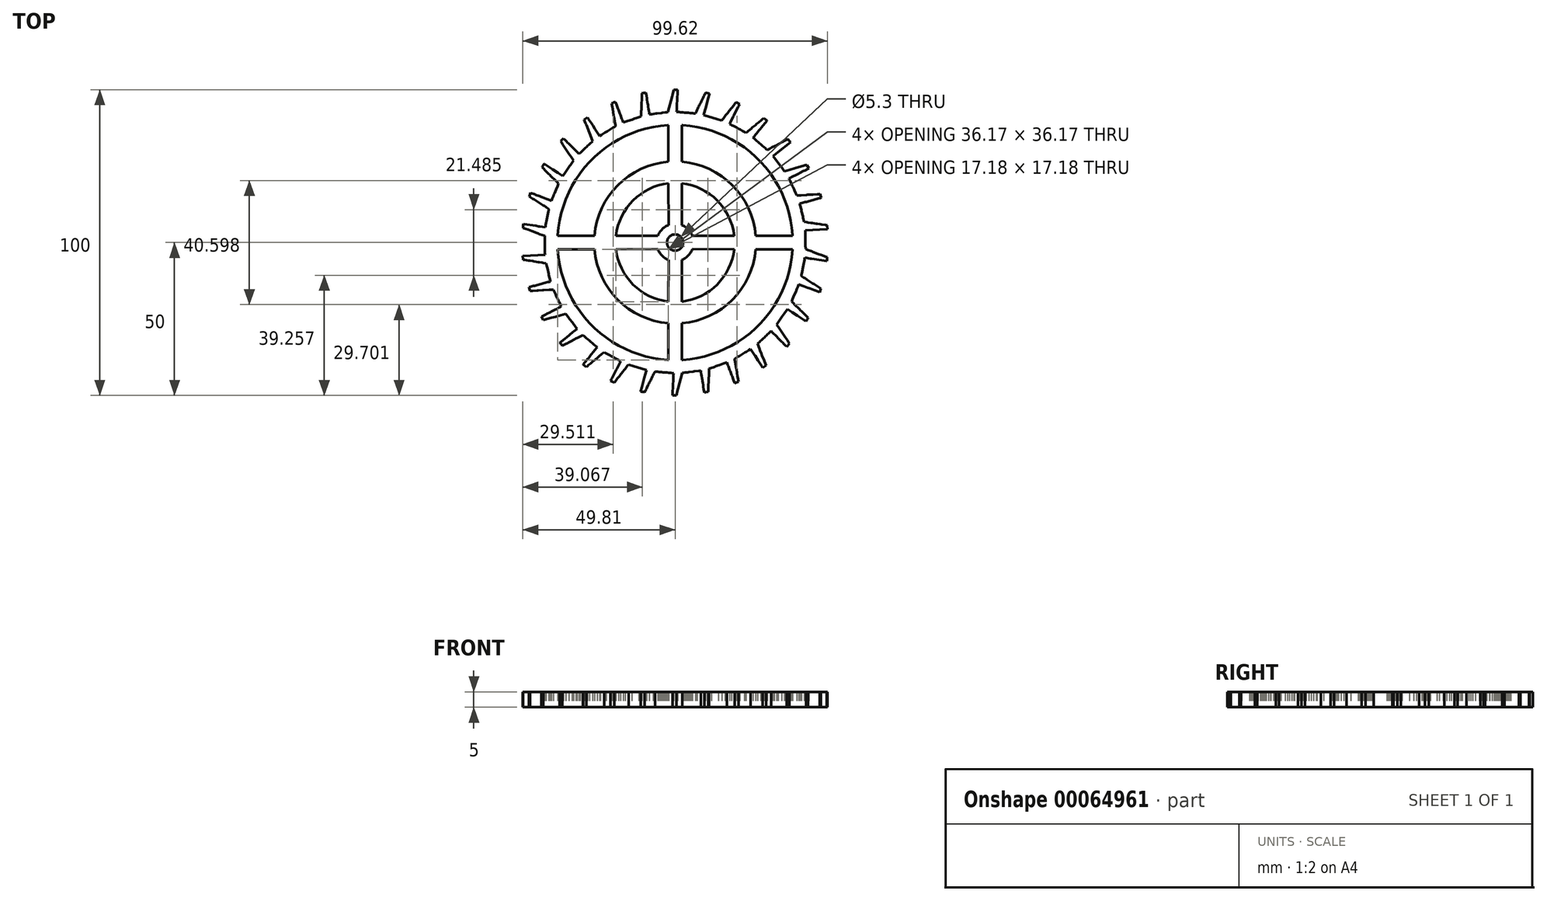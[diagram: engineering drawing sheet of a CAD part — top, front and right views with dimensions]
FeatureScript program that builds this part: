
annotation { "Feature Type Name" : "Feature", "Feature Type Description" : "" }
export const myFeature = defineFeature(function(context is Context, id is Id, definition is map)
    precondition{}
    {
        {
            var Q0;
            Q0=qCreatedBy(makeId("Top.planeOp"),FACE);
            var sketch = newSketch(context, id + "F0", { "sketchPlane" : qUnion([Q0])});
            skLineSegment(sketch, "E0", {"start": v(-36.57, 34.1) * mm, "end": v(-36.87, 33.77) * mm});
            skLineSegment(sketch, "E1", {"start": v(-36.87, 33.77) * mm, "end": v(-37.17, 33.44) * mm});
            skLineSegment(sketch, "E2", {"start": v(-37.17, 33.44) * mm, "end": v(-37.45, 33.13) * mm});
            skLineSegment(sketch, "E3", {"start": v(-37.45, 33.13) * mm, "end": v(-37.2, 32.76) * mm});
            skLineSegment(sketch, "E4", {"start": v(-37.2, 32.76) * mm, "end": v(-36.95, 32.39) * mm});
            skLineSegment(sketch, "E5", {"start": v(-36.95, 32.39) * mm, "end": v(-36.7, 32.02) * mm});
            skLineSegment(sketch, "E6", {"start": v(-36.7, 32.02) * mm, "end": v(-36.46, 31.65) * mm});
            skLineSegment(sketch, "E7", {"start": v(-36.46, 31.65) * mm, "end": v(-36.21, 31.28) * mm});
            skLineSegment(sketch, "E8", {"start": v(-36.21, 31.28) * mm, "end": v(-35.97, 30.9) * mm});
            skLineSegment(sketch, "E9", {"start": v(-35.97, 30.9) * mm, "end": v(-35.72, 30.53) * mm});
            skLineSegment(sketch, "E10", {"start": v(-35.72, 30.53) * mm, "end": v(-35.47, 30.16) * mm});
            skLineSegment(sketch, "E11", {"start": v(-35.47, 30.16) * mm, "end": v(-35.23, 29.8) * mm});
            skLineSegment(sketch, "E12", {"start": v(-35.23, 29.8) * mm, "end": v(-34.98, 29.42) * mm});
            skLineSegment(sketch, "E13", {"start": v(-34.98, 29.42) * mm, "end": v(-34.74, 29.05) * mm});
            skLineSegment(sketch, "E14", {"start": v(-34.74, 29.05) * mm, "end": v(-34.49, 28.68) * mm});
            skLineSegment(sketch, "E15", {"start": v(-34.49, 28.68) * mm, "end": v(-34.24, 28.3) * mm});
            skLineSegment(sketch, "E16", {"start": v(-34.24, 28.3) * mm, "end": v(-34, 27.93) * mm});
            skLineSegment(sketch, "E17", {"start": v(-34, 27.93) * mm, "end": v(-33.75, 27.56) * mm});
            skLineSegment(sketch, "E18", {"start": v(-33.75, 27.56) * mm, "end": v(-33.5, 27.2) * mm});
            skLineSegment(sketch, "E19", {"start": v(-33.5, 27.2) * mm, "end": v(-33.26, 26.83) * mm});
            skLineSegment(sketch, "E20", {"start": v(-33.26, 26.83) * mm, "end": v(-33.51, 26.46) * mm});
            skLineSegment(sketch, "E21", {"start": v(-33.51, 26.46) * mm, "end": v(-33.77, 26.1) * mm});
            skLineSegment(sketch, "E22", {"start": v(-33.77, 26.1) * mm, "end": v(-34.02, 25.73) * mm});
            skLineSegment(sketch, "E23", {"start": v(-34.02, 25.73) * mm, "end": v(-34.28, 25.37) * mm});
            skLineSegment(sketch, "E24", {"start": v(-34.28, 25.37) * mm, "end": v(-34.53, 25) * mm});
            skLineSegment(sketch, "E25", {"start": v(-34.53, 25) * mm, "end": v(-34.79, 24.63) * mm});
            skLineSegment(sketch, "E26", {"start": v(-34.79, 24.63) * mm, "end": v(-35.04, 24.27) * mm});
            skLineSegment(sketch, "E27", {"start": v(-35.04, 24.27) * mm, "end": v(-35.3, 23.9) * mm});
            skLineSegment(sketch, "E28", {"start": v(-35.3, 23.9) * mm, "end": v(-35.55, 23.53) * mm});
            skLineSegment(sketch, "E29", {"start": v(-35.55, 23.53) * mm, "end": v(-35.8, 23.17) * mm});
            skLineSegment(sketch, "E30", {"start": v(-35.8, 23.17) * mm, "end": v(-36.06, 22.8) * mm});
            skLineSegment(sketch, "E31", {"start": v(-36.06, 22.8) * mm, "end": v(-36.31, 22.44) * mm});
            skLineSegment(sketch, "E32", {"start": v(-36.31, 22.44) * mm, "end": v(-36.56, 22.07) * mm});
            skLineSegment(sketch, "E33", {"start": v(-36.56, 22.07) * mm, "end": v(-36.76, 21.8) * mm});
            skLineSegment(sketch, "E34", {"start": v(-36.76, 21.8) * mm, "end": v(-37.13, 22.03) * mm});
            skLineSegment(sketch, "E35", {"start": v(-37.13, 22.03) * mm, "end": v(-37.5, 22.28) * mm});
            skLineSegment(sketch, "E36", {"start": v(-37.5, 22.28) * mm, "end": v(-37.88, 22.52) * mm});
            skLineSegment(sketch, "E37", {"start": v(-37.88, 22.52) * mm, "end": v(-38.25, 22.76) * mm});
            skLineSegment(sketch, "E38", {"start": v(-38.25, 22.76) * mm, "end": v(-38.63, 23) * mm});
            skLineSegment(sketch, "E39", {"start": v(-38.63, 23) * mm, "end": v(-39, 23.25) * mm});
            skLineSegment(sketch, "E40", {"start": v(-39, 23.25) * mm, "end": v(-39.38, 23.49) * mm});
            skLineSegment(sketch, "E41", {"start": v(-39.38, 23.49) * mm, "end": v(-39.75, 23.73) * mm});
            skLineSegment(sketch, "E42", {"start": v(-39.75, 23.73) * mm, "end": v(-40.12, 23.98) * mm});
            skLineSegment(sketch, "E43", {"start": v(-40.12, 23.98) * mm, "end": v(-40.5, 24.22) * mm});
            skLineSegment(sketch, "E44", {"start": v(-40.5, 24.22) * mm, "end": v(-40.87, 24.46) * mm});
            skLineSegment(sketch, "E45", {"start": v(-40.87, 24.46) * mm, "end": v(-41.24, 24.7) * mm});
            skLineSegment(sketch, "E46", {"start": v(-41.24, 24.7) * mm, "end": v(-41.62, 24.95) * mm});
            skLineSegment(sketch, "E47", {"start": v(-41.62, 24.95) * mm, "end": v(-42, 25.19) * mm});
            skLineSegment(sketch, "E48", {"start": v(-42, 25.19) * mm, "end": v(-42.37, 25.43) * mm});
            skLineSegment(sketch, "E49", {"start": v(-42.37, 25.43) * mm, "end": v(-42.74, 25.67) * mm});
            skLineSegment(sketch, "E50", {"start": v(-42.74, 25.67) * mm, "end": v(-42.86, 25.75) * mm});
            skLineSegment(sketch, "E51", {"start": v(-42.86, 25.75) * mm, "end": v(-43.08, 25.37) * mm});
            skLineSegment(sketch, "E52", {"start": v(-43.08, 25.37) * mm, "end": v(-43.3, 24.98) * mm});
            skLineSegment(sketch, "E53", {"start": v(-43.3, 24.98) * mm, "end": v(-43.52, 24.62) * mm});
            skLineSegment(sketch, "E54", {"start": v(-43.52, 24.62) * mm, "end": v(-43.2, 24.3) * mm});
            skLineSegment(sketch, "E55", {"start": v(-43.2, 24.3) * mm, "end": v(-42.88, 24) * mm});
            skLineSegment(sketch, "E56", {"start": v(-42.88, 24) * mm, "end": v(-42.56, 23.69) * mm});
            skLineSegment(sketch, "E57", {"start": v(-42.56, 23.69) * mm, "end": v(-42.24, 23.37) * mm});
            skLineSegment(sketch, "E58", {"start": v(-42.24, 23.37) * mm, "end": v(-41.93, 23.06) * mm});
            skLineSegment(sketch, "E59", {"start": v(-41.93, 23.06) * mm, "end": v(-41.6, 22.75) * mm});
            skLineSegment(sketch, "E60", {"start": v(-41.6, 22.75) * mm, "end": v(-41.29, 22.44) * mm});
            skLineSegment(sketch, "E61", {"start": v(-41.29, 22.44) * mm, "end": v(-40.97, 22.13) * mm});
            skLineSegment(sketch, "E62", {"start": v(-40.97, 22.13) * mm, "end": v(-40.65, 21.82) * mm});
            skLineSegment(sketch, "E63", {"start": v(-40.65, 21.82) * mm, "end": v(-40.33, 21.5) * mm});
            skLineSegment(sketch, "E64", {"start": v(-40.33, 21.5) * mm, "end": v(-40.02, 21.2) * mm});
            skLineSegment(sketch, "E65", {"start": v(-40.02, 21.2) * mm, "end": v(-39.7, 20.88) * mm});
            skLineSegment(sketch, "E66", {"start": v(-39.7, 20.88) * mm, "end": v(-39.38, 20.57) * mm});
            skLineSegment(sketch, "E67", {"start": v(-39.38, 20.57) * mm, "end": v(-39.06, 20.26) * mm});
            skLineSegment(sketch, "E68", {"start": v(-39.06, 20.26) * mm, "end": v(-38.74, 19.94) * mm});
            skLineSegment(sketch, "E69", {"start": v(-38.74, 19.94) * mm, "end": v(-38.42, 19.63) * mm});
            skLineSegment(sketch, "E70", {"start": v(-38.42, 19.63) * mm, "end": v(-38.11, 19.33) * mm});
            skLineSegment(sketch, "E71", {"start": v(-38.11, 19.33) * mm, "end": v(-38.28, 18.92) * mm});
            skLineSegment(sketch, "E72", {"start": v(-38.28, 18.92) * mm, "end": v(-38.46, 18.5) * mm});
            skLineSegment(sketch, "E73", {"start": v(-38.46, 18.5) * mm, "end": v(-38.63, 18.1) * mm});
            skLineSegment(sketch, "E74", {"start": v(-38.63, 18.1) * mm, "end": v(-38.8, 17.68) * mm});
            skLineSegment(sketch, "E75", {"start": v(-38.8, 17.68) * mm, "end": v(-38.97, 17.27) * mm});
            skLineSegment(sketch, "E76", {"start": v(-38.97, 17.27) * mm, "end": v(-39.15, 16.86) * mm});
            skLineSegment(sketch, "E77", {"start": v(-39.15, 16.86) * mm, "end": v(-39.32, 16.45) * mm});
            skLineSegment(sketch, "E78", {"start": v(-39.32, 16.45) * mm, "end": v(-39.5, 16.04) * mm});
            skLineSegment(sketch, "E79", {"start": v(-39.5, 16.04) * mm, "end": v(-39.66, 15.63) * mm});
            skLineSegment(sketch, "E80", {"start": v(-39.66, 15.63) * mm, "end": v(-39.84, 15.22) * mm});
            skLineSegment(sketch, "E81", {"start": v(-39.84, 15.22) * mm, "end": v(-40, 14.8) * mm});
            skLineSegment(sketch, "E82", {"start": v(-40, 14.8) * mm, "end": v(-40.18, 14.4) * mm});
            skLineSegment(sketch, "E83", {"start": v(-40.18, 14.4) * mm, "end": v(-40.35, 13.99) * mm});
            skLineSegment(sketch, "E84", {"start": v(-40.35, 13.99) * mm, "end": v(-40.49, 13.67) * mm});
            skLineSegment(sketch, "E85", {"start": v(-40.49, 13.67) * mm, "end": v(-40.9, 13.83) * mm});
            skLineSegment(sketch, "E86", {"start": v(-40.9, 13.83) * mm, "end": v(-41.32, 14) * mm});
            skLineSegment(sketch, "E87", {"start": v(-41.32, 14) * mm, "end": v(-41.73, 14.15) * mm});
            skLineSegment(sketch, "E88", {"start": v(-41.73, 14.15) * mm, "end": v(-42.15, 14.31) * mm});
            skLineSegment(sketch, "E89", {"start": v(-42.15, 14.31) * mm, "end": v(-42.57, 14.47) * mm});
            skLineSegment(sketch, "E90", {"start": v(-42.57, 14.47) * mm, "end": v(-42.98, 14.63) * mm});
            skLineSegment(sketch, "E91", {"start": v(-42.98, 14.63) * mm, "end": v(-43.4, 14.8) * mm});
            skLineSegment(sketch, "E92", {"start": v(-43.4, 14.8) * mm, "end": v(-43.81, 14.95) * mm});
            skLineSegment(sketch, "E93", {"start": v(-43.81, 14.95) * mm, "end": v(-44.23, 15.1) * mm});
            skLineSegment(sketch, "E94", {"start": v(-44.23, 15.1) * mm, "end": v(-44.65, 15.27) * mm});
            skLineSegment(sketch, "E95", {"start": v(-44.65, 15.27) * mm, "end": v(-45.06, 15.43) * mm});
            skLineSegment(sketch, "E96", {"start": v(-45.06, 15.43) * mm, "end": v(-45.48, 15.59) * mm});
            skLineSegment(sketch, "E97", {"start": v(-45.48, 15.59) * mm, "end": v(-45.9, 15.75) * mm});
            skLineSegment(sketch, "E98", {"start": v(-45.9, 15.75) * mm, "end": v(-46.31, 15.9) * mm});
            skLineSegment(sketch, "E99", {"start": v(-46.31, 15.9) * mm, "end": v(-46.73, 16.07) * mm});
            skLineSegment(sketch, "E100", {"start": v(-46.73, 16.07) * mm, "end": v(-47.14, 16.23) * mm});
            skLineSegment(sketch, "E101", {"start": v(-47.14, 16.23) * mm, "end": v(-47.28, 16.28) * mm});
            skLineSegment(sketch, "E102", {"start": v(-47.28, 16.28) * mm, "end": v(-47.42, 15.86) * mm});
            skLineSegment(sketch, "E103", {"start": v(-47.42, 15.86) * mm, "end": v(-47.56, 15.43) * mm});
            skLineSegment(sketch, "E104", {"start": v(-47.56, 15.43) * mm, "end": v(-47.69, 15.04) * mm});
            skLineSegment(sketch, "E105", {"start": v(-47.69, 15.04) * mm, "end": v(-47.3, 14.8) * mm});
            skLineSegment(sketch, "E106", {"start": v(-47.3, 14.8) * mm, "end": v(-46.93, 14.56) * mm});
            skLineSegment(sketch, "E107", {"start": v(-46.93, 14.56) * mm, "end": v(-46.56, 14.32) * mm});
            skLineSegment(sketch, "E108", {"start": v(-46.56, 14.32) * mm, "end": v(-46.18, 14.08) * mm});
            skLineSegment(sketch, "E109", {"start": v(-46.18, 14.08) * mm, "end": v(-45.8, 13.84) * mm});
            skLineSegment(sketch, "E110", {"start": v(-45.8, 13.84) * mm, "end": v(-45.43, 13.6) * mm});
            skLineSegment(sketch, "E111", {"start": v(-45.43, 13.6) * mm, "end": v(-45.05, 13.36) * mm});
            skLineSegment(sketch, "E112", {"start": v(-45.05, 13.36) * mm, "end": v(-44.68, 13.13) * mm});
            skLineSegment(sketch, "E113", {"start": v(-44.68, 13.13) * mm, "end": v(-44.3, 12.89) * mm});
            skLineSegment(sketch, "E114", {"start": v(-44.3, 12.89) * mm, "end": v(-43.92, 12.65) * mm});
            skLineSegment(sketch, "E115", {"start": v(-43.92, 12.65) * mm, "end": v(-43.55, 12.4) * mm});
            skLineSegment(sketch, "E116", {"start": v(-43.55, 12.4) * mm, "end": v(-43.17, 12.17) * mm});
            skLineSegment(sketch, "E117", {"start": v(-43.17, 12.17) * mm, "end": v(-42.8, 11.93) * mm});
            skLineSegment(sketch, "E118", {"start": v(-42.8, 11.93) * mm, "end": v(-42.42, 11.7) * mm});
            skLineSegment(sketch, "E119", {"start": v(-42.42, 11.7) * mm, "end": v(-42.04, 11.45) * mm});
            skLineSegment(sketch, "E120", {"start": v(-42.04, 11.45) * mm, "end": v(-41.67, 11.22) * mm});
            skLineSegment(sketch, "E121", {"start": v(-41.67, 11.22) * mm, "end": v(-41.3, 10.98) * mm});
            skLineSegment(sketch, "E122", {"start": v(-41.3, 10.98) * mm, "end": v(-41.38, 10.54) * mm});
            skLineSegment(sketch, "E123", {"start": v(-41.38, 10.54) * mm, "end": v(-41.46, 10.1) * mm});
            skLineSegment(sketch, "E124", {"start": v(-41.46, 10.1) * mm, "end": v(-41.55, 9.67) * mm});
            skLineSegment(sketch, "E125", {"start": v(-41.55, 9.67) * mm, "end": v(-41.63, 9.23) * mm});
            skLineSegment(sketch, "E126", {"start": v(-41.63, 9.23) * mm, "end": v(-41.71, 8.8) * mm});
            skLineSegment(sketch, "E127", {"start": v(-41.71, 8.8) * mm, "end": v(-41.8, 8.35) * mm});
            skLineSegment(sketch, "E128", {"start": v(-41.8, 8.35) * mm, "end": v(-41.88, 7.92) * mm});
            skLineSegment(sketch, "E129", {"start": v(-41.88, 7.92) * mm, "end": v(-41.96, 7.48) * mm});
            skLineSegment(sketch, "E130", {"start": v(-41.96, 7.48) * mm, "end": v(-42.05, 7.04) * mm});
            skLineSegment(sketch, "E131", {"start": v(-42.05, 7.04) * mm, "end": v(-42.13, 6.6) * mm});
            skLineSegment(sketch, "E132", {"start": v(-42.13, 6.6) * mm, "end": v(-42.21, 6.17) * mm});
            skLineSegment(sketch, "E133", {"start": v(-42.21, 6.17) * mm, "end": v(-42.3, 5.73) * mm});
            skLineSegment(sketch, "E134", {"start": v(-42.3, 5.73) * mm, "end": v(-42.38, 5.3) * mm});
            skLineSegment(sketch, "E135", {"start": v(-42.38, 5.3) * mm, "end": v(-42.44, 4.96) * mm});
            skLineSegment(sketch, "E136", {"start": v(-42.44, 4.96) * mm, "end": v(-42.88, 5.03) * mm});
            skLineSegment(sketch, "E137", {"start": v(-42.88, 5.03) * mm, "end": v(-43.32, 5.1) * mm});
            skLineSegment(sketch, "E138", {"start": v(-43.32, 5.1) * mm, "end": v(-43.76, 5.16) * mm});
            skLineSegment(sketch, "E139", {"start": v(-43.76, 5.16) * mm, "end": v(-44.2, 5.23) * mm});
            skLineSegment(sketch, "E140", {"start": v(-44.2, 5.23) * mm, "end": v(-44.65, 5.3) * mm});
            skLineSegment(sketch, "E141", {"start": v(-44.65, 5.3) * mm, "end": v(-45.09, 5.37) * mm});
            skLineSegment(sketch, "E142", {"start": v(-45.09, 5.37) * mm, "end": v(-45.53, 5.44) * mm});
            skLineSegment(sketch, "E143", {"start": v(-45.53, 5.44) * mm, "end": v(-45.97, 5.51) * mm});
            skLineSegment(sketch, "E144", {"start": v(-45.97, 5.51) * mm, "end": v(-46.4, 5.58) * mm});
            skLineSegment(sketch, "E145", {"start": v(-46.4, 5.58) * mm, "end": v(-46.85, 5.65) * mm});
            skLineSegment(sketch, "E146", {"start": v(-46.85, 5.65) * mm, "end": v(-47.29, 5.72) * mm});
            skLineSegment(sketch, "E147", {"start": v(-47.29, 5.72) * mm, "end": v(-47.73, 5.8) * mm});
            skLineSegment(sketch, "E148", {"start": v(-47.73, 5.8) * mm, "end": v(-48.17, 5.86) * mm});
            skLineSegment(sketch, "E149", {"start": v(-48.17, 5.86) * mm, "end": v(-48.6, 5.93) * mm});
            skLineSegment(sketch, "E150", {"start": v(-48.6, 5.93) * mm, "end": v(-49.05, 6) * mm});
            skLineSegment(sketch, "E151", {"start": v(-49.05, 6) * mm, "end": v(-49.49, 6.07) * mm});
            skLineSegment(sketch, "E152", {"start": v(-49.49, 6.07) * mm, "end": v(-49.63, 6.1) * mm});
            skLineSegment(sketch, "E153", {"start": v(-49.63, 6.1) * mm, "end": v(-49.68, 5.65) * mm});
            skLineSegment(sketch, "E154", {"start": v(-49.68, 5.65) * mm, "end": v(-49.72, 5.2) * mm});
            skLineSegment(sketch, "E155", {"start": v(-49.72, 5.2) * mm, "end": v(-49.77, 4.8) * mm});
            skLineSegment(sketch, "E156", {"start": v(-49.77, 4.8) * mm, "end": v(-49.35, 4.64) * mm});
            skLineSegment(sketch, "E157", {"start": v(-49.35, 4.64) * mm, "end": v(-48.93, 4.48) * mm});
            skLineSegment(sketch, "E158", {"start": v(-48.93, 4.48) * mm, "end": v(-48.52, 4.33) * mm});
            skLineSegment(sketch, "E159", {"start": v(-48.52, 4.33) * mm, "end": v(-48.1, 4.17) * mm});
            skLineSegment(sketch, "E160", {"start": v(-48.1, 4.17) * mm, "end": v(-47.68, 4.02) * mm});
            skLineSegment(sketch, "E161", {"start": v(-47.68, 4.02) * mm, "end": v(-47.26, 3.86) * mm});
            skLineSegment(sketch, "E162", {"start": v(-47.26, 3.86) * mm, "end": v(-46.85, 3.7) * mm});
            skLineSegment(sketch, "E163", {"start": v(-46.85, 3.7) * mm, "end": v(-46.43, 3.55) * mm});
            skLineSegment(sketch, "E164", {"start": v(-46.43, 3.55) * mm, "end": v(-46.01, 3.4) * mm});
            skLineSegment(sketch, "E165", {"start": v(-46.01, 3.4) * mm, "end": v(-45.6, 3.24) * mm});
            skLineSegment(sketch, "E166", {"start": v(-45.6, 3.24) * mm, "end": v(-45.18, 3.08) * mm});
            skLineSegment(sketch, "E167", {"start": v(-45.18, 3.08) * mm, "end": v(-44.76, 2.93) * mm});
            skLineSegment(sketch, "E168", {"start": v(-44.76, 2.93) * mm, "end": v(-44.34, 2.77) * mm});
            skLineSegment(sketch, "E169", {"start": v(-44.34, 2.77) * mm, "end": v(-43.92, 2.62) * mm});
            skLineSegment(sketch, "E170", {"start": v(-43.92, 2.62) * mm, "end": v(-43.5, 2.46) * mm});
            skLineSegment(sketch, "E171", {"start": v(-43.5, 2.46) * mm, "end": v(-43.09, 2.3) * mm});
            skLineSegment(sketch, "E172", {"start": v(-43.09, 2.3) * mm, "end": v(-42.68, 2.16) * mm});
            skLineSegment(sketch, "E173", {"start": v(-42.68, 2.16) * mm, "end": v(-42.67, 1.7) * mm});
            skLineSegment(sketch, "E174", {"start": v(-42.67, 1.7) * mm, "end": v(-42.66, 1.26) * mm});
            skLineSegment(sketch, "E175", {"start": v(-42.66, 1.26) * mm, "end": v(-42.65, 0.82) * mm});
            skLineSegment(sketch, "E176", {"start": v(-42.65, 0.82) * mm, "end": v(-42.64, 0.37) * mm});
            skLineSegment(sketch, "E177", {"start": v(-42.64, 0.37) * mm, "end": v(-42.63, -0.07) * mm});
            skLineSegment(sketch, "E178", {"start": v(-42.63, -0.07) * mm, "end": v(-42.62, -0.52) * mm});
            skLineSegment(sketch, "E179", {"start": v(-42.62, -0.52) * mm, "end": v(-42.61, -0.96) * mm});
            skLineSegment(sketch, "E180", {"start": v(-42.61, -0.96) * mm, "end": v(-42.6, -1.4) * mm});
            skLineSegment(sketch, "E181", {"start": v(-42.6, -1.4) * mm, "end": v(-42.6, -1.85) * mm});
            skLineSegment(sketch, "E182", {"start": v(-42.6, -1.85) * mm, "end": v(-42.58, -2.3) * mm});
            skLineSegment(sketch, "E183", {"start": v(-42.58, -2.3) * mm, "end": v(-42.57, -2.75) * mm});
            skLineSegment(sketch, "E184", {"start": v(-42.57, -2.75) * mm, "end": v(-42.56, -3.2) * mm});
            skLineSegment(sketch, "E185", {"start": v(-42.56, -3.2) * mm, "end": v(-42.55, -3.64) * mm});
            skLineSegment(sketch, "E186", {"start": v(-42.55, -3.64) * mm, "end": v(-42.55, -3.98) * mm});
            skLineSegment(sketch, "E187", {"start": v(-42.55, -3.98) * mm, "end": v(-43, -4) * mm});
            skLineSegment(sketch, "E188", {"start": v(-43, -4) * mm, "end": v(-43.44, -4.02) * mm});
            skLineSegment(sketch, "E189", {"start": v(-43.44, -4.02) * mm, "end": v(-43.88, -4.05) * mm});
            skLineSegment(sketch, "E190", {"start": v(-43.88, -4.05) * mm, "end": v(-44.33, -4.07) * mm});
            skLineSegment(sketch, "E191", {"start": v(-44.33, -4.07) * mm, "end": v(-44.77, -4.1) * mm});
            skLineSegment(sketch, "E192", {"start": v(-44.77, -4.1) * mm, "end": v(-45.22, -4.12) * mm});
            skLineSegment(sketch, "E193", {"start": v(-45.22, -4.12) * mm, "end": v(-45.66, -4.14) * mm});
            skLineSegment(sketch, "E194", {"start": v(-45.66, -4.14) * mm, "end": v(-46.1, -4.16) * mm});
            skLineSegment(sketch, "E195", {"start": v(-46.1, -4.16) * mm, "end": v(-46.55, -4.19) * mm});
            skLineSegment(sketch, "E196", {"start": v(-46.55, -4.19) * mm, "end": v(-47, -4.21) * mm});
            skLineSegment(sketch, "E197", {"start": v(-47, -4.21) * mm, "end": v(-47.44, -4.23) * mm});
            skLineSegment(sketch, "E198", {"start": v(-47.44, -4.23) * mm, "end": v(-47.89, -4.26) * mm});
            skLineSegment(sketch, "E199", {"start": v(-47.89, -4.26) * mm, "end": v(-48.33, -4.28) * mm});
            skLineSegment(sketch, "E200", {"start": v(-48.33, -4.28) * mm, "end": v(-48.78, -4.3) * mm});
            skLineSegment(sketch, "E201", {"start": v(-48.78, -4.3) * mm, "end": v(-49.22, -4.33) * mm});
            skLineSegment(sketch, "E202", {"start": v(-49.22, -4.33) * mm, "end": v(-49.67, -4.35) * mm});
            skLineSegment(sketch, "E203", {"start": v(-49.67, -4.35) * mm, "end": v(-49.8, -4.36) * mm});
            skLineSegment(sketch, "E204", {"start": v(-49.8, -4.36) * mm, "end": v(-49.77, -4.8) * mm});
            skLineSegment(sketch, "E205", {"start": v(-49.77, -4.8) * mm, "end": v(-49.72, -5.24) * mm});
            skLineSegment(sketch, "E206", {"start": v(-49.72, -5.24) * mm, "end": v(-49.68, -5.66) * mm});
            skLineSegment(sketch, "E207", {"start": v(-49.68, -5.66) * mm, "end": v(-49.24, -5.73) * mm});
            skLineSegment(sketch, "E208", {"start": v(-49.24, -5.73) * mm, "end": v(-48.8, -5.8) * mm});
            skLineSegment(sketch, "E209", {"start": v(-48.8, -5.8) * mm, "end": v(-48.36, -5.86) * mm});
            skLineSegment(sketch, "E210", {"start": v(-48.36, -5.86) * mm, "end": v(-47.92, -5.92) * mm});
            skLineSegment(sketch, "E211", {"start": v(-47.92, -5.92) * mm, "end": v(-47.47, -5.99) * mm});
            skLineSegment(sketch, "E212", {"start": v(-47.47, -5.99) * mm, "end": v(-47.03, -6.05) * mm});
            skLineSegment(sketch, "E213", {"start": v(-47.03, -6.05) * mm, "end": v(-46.6, -6.12) * mm});
            skLineSegment(sketch, "E214", {"start": v(-46.6, -6.12) * mm, "end": v(-46.15, -6.18) * mm});
            skLineSegment(sketch, "E215", {"start": v(-46.15, -6.18) * mm, "end": v(-45.71, -6.25) * mm});
            skLineSegment(sketch, "E216", {"start": v(-45.71, -6.25) * mm, "end": v(-45.27, -6.31) * mm});
            skLineSegment(sketch, "E217", {"start": v(-45.27, -6.31) * mm, "end": v(-44.83, -6.38) * mm});
            skLineSegment(sketch, "E218", {"start": v(-44.83, -6.38) * mm, "end": v(-44.39, -6.44) * mm});
            skLineSegment(sketch, "E219", {"start": v(-44.39, -6.44) * mm, "end": v(-43.95, -6.5) * mm});
            skLineSegment(sketch, "E220", {"start": v(-43.95, -6.5) * mm, "end": v(-43.5, -6.57) * mm});
            skLineSegment(sketch, "E221", {"start": v(-43.5, -6.57) * mm, "end": v(-43.07, -6.64) * mm});
            skLineSegment(sketch, "E222", {"start": v(-43.07, -6.64) * mm, "end": v(-42.63, -6.7) * mm});
            skLineSegment(sketch, "E223", {"start": v(-42.63, -6.7) * mm, "end": v(-42.2, -6.77) * mm});
            skLineSegment(sketch, "E224", {"start": v(-42.2, -6.77) * mm, "end": v(-42.1, -7.2) * mm});
            skLineSegment(sketch, "E225", {"start": v(-42.1, -7.2) * mm, "end": v(-41.99, -7.63) * mm});
            skLineSegment(sketch, "E226", {"start": v(-41.99, -7.63) * mm, "end": v(-41.89, -8.07) * mm});
            skLineSegment(sketch, "E227", {"start": v(-41.89, -8.07) * mm, "end": v(-41.79, -8.5) * mm});
            skLineSegment(sketch, "E228", {"start": v(-41.79, -8.5) * mm, "end": v(-41.68, -8.93) * mm});
            skLineSegment(sketch, "E229", {"start": v(-41.68, -8.93) * mm, "end": v(-41.58, -9.37) * mm});
            skLineSegment(sketch, "E230", {"start": v(-41.58, -9.37) * mm, "end": v(-41.48, -9.8) * mm});
            skLineSegment(sketch, "E231", {"start": v(-41.48, -9.8) * mm, "end": v(-41.38, -10.24) * mm});
            skLineSegment(sketch, "E232", {"start": v(-41.38, -10.24) * mm, "end": v(-41.28, -10.67) * mm});
            skLineSegment(sketch, "E233", {"start": v(-41.28, -10.67) * mm, "end": v(-41.17, -11.1) * mm});
            skLineSegment(sketch, "E234", {"start": v(-41.17, -11.1) * mm, "end": v(-41.07, -11.54) * mm});
            skLineSegment(sketch, "E235", {"start": v(-41.07, -11.54) * mm, "end": v(-40.97, -11.97) * mm});
            skLineSegment(sketch, "E236", {"start": v(-40.97, -11.97) * mm, "end": v(-40.87, -12.4) * mm});
            skLineSegment(sketch, "E237", {"start": v(-40.87, -12.4) * mm, "end": v(-40.8, -12.74) * mm});
            skLineSegment(sketch, "E238", {"start": v(-40.8, -12.74) * mm, "end": v(-41.22, -12.85) * mm});
            skLineSegment(sketch, "E239", {"start": v(-41.22, -12.85) * mm, "end": v(-41.65, -12.97) * mm});
            skLineSegment(sketch, "E240", {"start": v(-41.65, -12.97) * mm, "end": v(-42.08, -13.08) * mm});
            skLineSegment(sketch, "E241", {"start": v(-42.08, -13.08) * mm, "end": v(-42.51, -13.2) * mm});
            skLineSegment(sketch, "E242", {"start": v(-42.51, -13.2) * mm, "end": v(-42.94, -13.31) * mm});
            skLineSegment(sketch, "E243", {"start": v(-42.94, -13.31) * mm, "end": v(-43.37, -13.43) * mm});
            skLineSegment(sketch, "E244", {"start": v(-43.37, -13.43) * mm, "end": v(-43.8, -13.54) * mm});
            skLineSegment(sketch, "E245", {"start": v(-43.8, -13.54) * mm, "end": v(-44.23, -13.66) * mm});
            skLineSegment(sketch, "E246", {"start": v(-44.23, -13.66) * mm, "end": v(-44.66, -13.77) * mm});
            skLineSegment(sketch, "E247", {"start": v(-44.66, -13.77) * mm, "end": v(-45.1, -13.89) * mm});
            skLineSegment(sketch, "E248", {"start": v(-45.1, -13.89) * mm, "end": v(-45.53, -14) * mm});
            skLineSegment(sketch, "E249", {"start": v(-45.53, -14) * mm, "end": v(-45.96, -14.12) * mm});
            skLineSegment(sketch, "E250", {"start": v(-45.96, -14.12) * mm, "end": v(-46.39, -14.24) * mm});
            skLineSegment(sketch, "E251", {"start": v(-46.39, -14.24) * mm, "end": v(-46.82, -14.35) * mm});
            skLineSegment(sketch, "E252", {"start": v(-46.82, -14.35) * mm, "end": v(-47.25, -14.47) * mm});
            skLineSegment(sketch, "E253", {"start": v(-47.25, -14.47) * mm, "end": v(-47.68, -14.58) * mm});
            skLineSegment(sketch, "E254", {"start": v(-47.68, -14.58) * mm, "end": v(-47.82, -14.62) * mm});
            skLineSegment(sketch, "E255", {"start": v(-47.82, -14.62) * mm, "end": v(-47.68, -15.04) * mm});
            skLineSegment(sketch, "E256", {"start": v(-47.68, -15.04) * mm, "end": v(-47.54, -15.47) * mm});
            skLineSegment(sketch, "E257", {"start": v(-47.54, -15.47) * mm, "end": v(-47.42, -15.87) * mm});
            skLineSegment(sketch, "E258", {"start": v(-47.42, -15.87) * mm, "end": v(-46.97, -15.84) * mm});
            skLineSegment(sketch, "E259", {"start": v(-46.97, -15.84) * mm, "end": v(-46.53, -15.8) * mm});
            skLineSegment(sketch, "E260", {"start": v(-46.53, -15.8) * mm, "end": v(-46.08, -15.78) * mm});
            skLineSegment(sketch, "E261", {"start": v(-46.08, -15.78) * mm, "end": v(-45.64, -15.75) * mm});
            skLineSegment(sketch, "E262", {"start": v(-45.64, -15.75) * mm, "end": v(-45.2, -15.73) * mm});
            skLineSegment(sketch, "E263", {"start": v(-45.2, -15.73) * mm, "end": v(-44.75, -15.7) * mm});
            skLineSegment(sketch, "E264", {"start": v(-44.75, -15.7) * mm, "end": v(-44.3, -15.67) * mm});
            skLineSegment(sketch, "E265", {"start": v(-44.3, -15.67) * mm, "end": v(-43.86, -15.64) * mm});
            skLineSegment(sketch, "E266", {"start": v(-43.86, -15.64) * mm, "end": v(-43.41, -15.61) * mm});
            skLineSegment(sketch, "E267", {"start": v(-43.41, -15.61) * mm, "end": v(-42.97, -15.59) * mm});
            skLineSegment(sketch, "E268", {"start": v(-42.97, -15.59) * mm, "end": v(-42.52, -15.56) * mm});
            skLineSegment(sketch, "E269", {"start": v(-42.52, -15.56) * mm, "end": v(-42.08, -15.53) * mm});
            skLineSegment(sketch, "E270", {"start": v(-42.08, -15.53) * mm, "end": v(-41.63, -15.5) * mm});
            skLineSegment(sketch, "E271", {"start": v(-41.63, -15.5) * mm, "end": v(-41.19, -15.47) * mm});
            skLineSegment(sketch, "E272", {"start": v(-41.19, -15.47) * mm, "end": v(-40.75, -15.45) * mm});
            skLineSegment(sketch, "E273", {"start": v(-40.75, -15.45) * mm, "end": v(-40.3, -15.42) * mm});
            skLineSegment(sketch, "E274", {"start": v(-40.3, -15.42) * mm, "end": v(-39.87, -15.39) * mm});
            skLineSegment(sketch, "E275", {"start": v(-39.87, -15.39) * mm, "end": v(-39.68, -15.8) * mm});
            skLineSegment(sketch, "E276", {"start": v(-39.68, -15.8) * mm, "end": v(-39.49, -16.2) * mm});
            skLineSegment(sketch, "E277", {"start": v(-39.49, -16.2) * mm, "end": v(-39.3, -16.6) * mm});
            skLineSegment(sketch, "E278", {"start": v(-39.3, -16.6) * mm, "end": v(-39.1, -17) * mm});
            skLineSegment(sketch, "E279", {"start": v(-39.1, -17) * mm, "end": v(-38.92, -17.4) * mm});
            skLineSegment(sketch, "E280", {"start": v(-38.92, -17.4) * mm, "end": v(-38.73, -17.8) * mm});
            skLineSegment(sketch, "E281", {"start": v(-38.73, -17.8) * mm, "end": v(-38.54, -18.21) * mm});
            skLineSegment(sketch, "E282", {"start": v(-38.54, -18.21) * mm, "end": v(-38.35, -18.61) * mm});
            skLineSegment(sketch, "E283", {"start": v(-38.35, -18.61) * mm, "end": v(-38.16, -19.02) * mm});
            skLineSegment(sketch, "E284", {"start": v(-38.16, -19.02) * mm, "end": v(-37.97, -19.42) * mm});
            skLineSegment(sketch, "E285", {"start": v(-37.97, -19.42) * mm, "end": v(-37.78, -19.82) * mm});
            skLineSegment(sketch, "E286", {"start": v(-37.78, -19.82) * mm, "end": v(-37.59, -20.23) * mm});
            skLineSegment(sketch, "E287", {"start": v(-37.59, -20.23) * mm, "end": v(-37.4, -20.63) * mm});
            skLineSegment(sketch, "E288", {"start": v(-37.4, -20.63) * mm, "end": v(-37.25, -20.94) * mm});
            skLineSegment(sketch, "E289", {"start": v(-37.25, -20.94) * mm, "end": v(-37.65, -21.14) * mm});
            skLineSegment(sketch, "E290", {"start": v(-37.65, -21.14) * mm, "end": v(-38.05, -21.34) * mm});
            skLineSegment(sketch, "E291", {"start": v(-38.05, -21.34) * mm, "end": v(-38.44, -21.55) * mm});
            skLineSegment(sketch, "E292", {"start": v(-38.44, -21.55) * mm, "end": v(-38.84, -21.75) * mm});
            skLineSegment(sketch, "E293", {"start": v(-38.84, -21.75) * mm, "end": v(-39.24, -21.95) * mm});
            skLineSegment(sketch, "E294", {"start": v(-39.24, -21.95) * mm, "end": v(-39.63, -22.15) * mm});
            skLineSegment(sketch, "E295", {"start": v(-39.63, -22.15) * mm, "end": v(-40.03, -22.35) * mm});
            skLineSegment(sketch, "E296", {"start": v(-40.03, -22.35) * mm, "end": v(-40.43, -22.56) * mm});
            skLineSegment(sketch, "E297", {"start": v(-40.43, -22.56) * mm, "end": v(-40.82, -22.76) * mm});
            skLineSegment(sketch, "E298", {"start": v(-40.82, -22.76) * mm, "end": v(-41.22, -22.96) * mm});
            skLineSegment(sketch, "E299", {"start": v(-41.22, -22.96) * mm, "end": v(-41.62, -23.16) * mm});
            skLineSegment(sketch, "E300", {"start": v(-41.62, -23.16) * mm, "end": v(-42.02, -23.37) * mm});
            skLineSegment(sketch, "E301", {"start": v(-42.02, -23.37) * mm, "end": v(-42.41, -23.57) * mm});
            skLineSegment(sketch, "E302", {"start": v(-42.41, -23.57) * mm, "end": v(-42.8, -23.77) * mm});
            skLineSegment(sketch, "E303", {"start": v(-42.8, -23.77) * mm, "end": v(-43.2, -23.97) * mm});
            skLineSegment(sketch, "E304", {"start": v(-43.2, -23.97) * mm, "end": v(-43.6, -24.18) * mm});
            skLineSegment(sketch, "E305", {"start": v(-43.6, -24.18) * mm, "end": v(-43.73, -24.24) * mm});
            skLineSegment(sketch, "E306", {"start": v(-43.73, -24.24) * mm, "end": v(-43.5, -24.63) * mm});
            skLineSegment(sketch, "E307", {"start": v(-43.5, -24.63) * mm, "end": v(-43.29, -25.01) * mm});
            skLineSegment(sketch, "E308", {"start": v(-43.29, -25.01) * mm, "end": v(-43.08, -25.38) * mm});
            skLineSegment(sketch, "E309", {"start": v(-43.08, -25.38) * mm, "end": v(-42.65, -25.26) * mm});
            skLineSegment(sketch, "E310", {"start": v(-42.65, -25.26) * mm, "end": v(-42.22, -25.14) * mm});
            skLineSegment(sketch, "E311", {"start": v(-42.22, -25.14) * mm, "end": v(-41.8, -25.02) * mm});
            skLineSegment(sketch, "E312", {"start": v(-41.8, -25.02) * mm, "end": v(-41.36, -24.9) * mm});
            skLineSegment(sketch, "E313", {"start": v(-41.36, -24.9) * mm, "end": v(-40.94, -24.78) * mm});
            skLineSegment(sketch, "E314", {"start": v(-40.94, -24.78) * mm, "end": v(-40.5, -24.66) * mm});
            skLineSegment(sketch, "E315", {"start": v(-40.5, -24.66) * mm, "end": v(-40.08, -24.54) * mm});
            skLineSegment(sketch, "E316", {"start": v(-40.08, -24.54) * mm, "end": v(-39.65, -24.42) * mm});
            skLineSegment(sketch, "E317", {"start": v(-39.65, -24.42) * mm, "end": v(-39.22, -24.3) * mm});
            skLineSegment(sketch, "E318", {"start": v(-39.22, -24.3) * mm, "end": v(-38.79, -24.18) * mm});
            skLineSegment(sketch, "E319", {"start": v(-38.79, -24.18) * mm, "end": v(-38.36, -24.06) * mm});
            skLineSegment(sketch, "E320", {"start": v(-38.36, -24.06) * mm, "end": v(-37.93, -23.94) * mm});
            skLineSegment(sketch, "E321", {"start": v(-37.93, -23.94) * mm, "end": v(-37.5, -23.82) * mm});
            skLineSegment(sketch, "E322", {"start": v(-37.5, -23.82) * mm, "end": v(-37.07, -23.7) * mm});
            skLineSegment(sketch, "E323", {"start": v(-37.07, -23.7) * mm, "end": v(-36.64, -23.58) * mm});
            skLineSegment(sketch, "E324", {"start": v(-36.64, -23.58) * mm, "end": v(-36.21, -23.46) * mm});
            skLineSegment(sketch, "E325", {"start": v(-36.21, -23.46) * mm, "end": v(-35.8, -23.34) * mm});
            skLineSegment(sketch, "E326", {"start": v(-35.8, -23.34) * mm, "end": v(-35.52, -23.7) * mm});
            skLineSegment(sketch, "E327", {"start": v(-35.52, -23.7) * mm, "end": v(-35.26, -24.05) * mm});
            skLineSegment(sketch, "E328", {"start": v(-35.26, -24.05) * mm, "end": v(-34.99, -24.4) * mm});
            skLineSegment(sketch, "E329", {"start": v(-34.99, -24.4) * mm, "end": v(-34.72, -24.76) * mm});
            skLineSegment(sketch, "E330", {"start": v(-34.72, -24.76) * mm, "end": v(-34.45, -25.12) * mm});
            skLineSegment(sketch, "E331", {"start": v(-34.45, -25.12) * mm, "end": v(-34.18, -25.47) * mm});
            skLineSegment(sketch, "E332", {"start": v(-34.18, -25.47) * mm, "end": v(-33.9, -25.83) * mm});
            skLineSegment(sketch, "E333", {"start": v(-33.9, -25.83) * mm, "end": v(-33.64, -26.18) * mm});
            skLineSegment(sketch, "E334", {"start": v(-33.64, -26.18) * mm, "end": v(-33.37, -26.54) * mm});
            skLineSegment(sketch, "E335", {"start": v(-33.37, -26.54) * mm, "end": v(-33.1, -26.9) * mm});
            skLineSegment(sketch, "E336", {"start": v(-33.1, -26.9) * mm, "end": v(-32.83, -27.25) * mm});
            skLineSegment(sketch, "E337", {"start": v(-32.83, -27.25) * mm, "end": v(-32.56, -27.6) * mm});
            skLineSegment(sketch, "E338", {"start": v(-32.56, -27.6) * mm, "end": v(-32.29, -27.95) * mm});
            skLineSegment(sketch, "E339", {"start": v(-32.29, -27.95) * mm, "end": v(-32.08, -28.23) * mm});
            skLineSegment(sketch, "E340", {"start": v(-32.08, -28.23) * mm, "end": v(-32.43, -28.5) * mm});
            skLineSegment(sketch, "E341", {"start": v(-32.43, -28.5) * mm, "end": v(-32.78, -28.79) * mm});
            skLineSegment(sketch, "E342", {"start": v(-32.78, -28.79) * mm, "end": v(-33.12, -29.07) * mm});
            skLineSegment(sketch, "E343", {"start": v(-33.12, -29.07) * mm, "end": v(-33.47, -29.35) * mm});
            skLineSegment(sketch, "E344", {"start": v(-33.47, -29.35) * mm, "end": v(-33.82, -29.63) * mm});
            skLineSegment(sketch, "E345", {"start": v(-33.82, -29.63) * mm, "end": v(-34.16, -29.9) * mm});
            skLineSegment(sketch, "E346", {"start": v(-34.16, -29.9) * mm, "end": v(-34.5, -30.19) * mm});
            skLineSegment(sketch, "E347", {"start": v(-34.5, -30.19) * mm, "end": v(-34.85, -30.47) * mm});
            skLineSegment(sketch, "E348", {"start": v(-34.85, -30.47) * mm, "end": v(-35.2, -30.75) * mm});
            skLineSegment(sketch, "E349", {"start": v(-35.2, -30.75) * mm, "end": v(-35.55, -31.03) * mm});
            skLineSegment(sketch, "E350", {"start": v(-35.55, -31.03) * mm, "end": v(-35.9, -31.31) * mm});
            skLineSegment(sketch, "E351", {"start": v(-35.9, -31.31) * mm, "end": v(-36.24, -31.6) * mm});
            skLineSegment(sketch, "E352", {"start": v(-36.24, -31.6) * mm, "end": v(-36.59, -31.87) * mm});
            skLineSegment(sketch, "E353", {"start": v(-36.59, -31.87) * mm, "end": v(-36.93, -32.15) * mm});
            skLineSegment(sketch, "E354", {"start": v(-36.93, -32.15) * mm, "end": v(-37.28, -32.43) * mm});
            skLineSegment(sketch, "E355", {"start": v(-37.28, -32.43) * mm, "end": v(-37.62, -32.71) * mm});
            skLineSegment(sketch, "E356", {"start": v(-37.62, -32.71) * mm, "end": v(-37.74, -32.8) * mm});
            skLineSegment(sketch, "E357", {"start": v(-37.74, -32.8) * mm, "end": v(-37.44, -33.14) * mm});
            skLineSegment(sketch, "E358", {"start": v(-37.44, -33.14) * mm, "end": v(-37.14, -33.47) * mm});
            skLineSegment(sketch, "E359", {"start": v(-37.14, -33.47) * mm, "end": v(-36.86, -33.78) * mm});
            skLineSegment(sketch, "E360", {"start": v(-36.86, -33.78) * mm, "end": v(-36.47, -33.57) * mm});
            skLineSegment(sketch, "E361", {"start": v(-36.47, -33.57) * mm, "end": v(-36.07, -33.37) * mm});
            skLineSegment(sketch, "E362", {"start": v(-36.07, -33.37) * mm, "end": v(-35.68, -33.16) * mm});
            skLineSegment(sketch, "E363", {"start": v(-35.68, -33.16) * mm, "end": v(-35.28, -32.95) * mm});
            skLineSegment(sketch, "E364", {"start": v(-35.28, -32.95) * mm, "end": v(-34.89, -32.75) * mm});
            skLineSegment(sketch, "E365", {"start": v(-34.89, -32.75) * mm, "end": v(-34.5, -32.54) * mm});
            skLineSegment(sketch, "E366", {"start": v(-34.5, -32.54) * mm, "end": v(-34.1, -32.33) * mm});
            skLineSegment(sketch, "E367", {"start": v(-34.1, -32.33) * mm, "end": v(-33.7, -32.13) * mm});
            skLineSegment(sketch, "E368", {"start": v(-33.7, -32.13) * mm, "end": v(-33.3, -31.92) * mm});
            skLineSegment(sketch, "E369", {"start": v(-33.3, -31.92) * mm, "end": v(-32.91, -31.71) * mm});
            skLineSegment(sketch, "E370", {"start": v(-32.91, -31.71) * mm, "end": v(-32.52, -31.5) * mm});
            skLineSegment(sketch, "E371", {"start": v(-32.52, -31.5) * mm, "end": v(-32.12, -31.3) * mm});
            skLineSegment(sketch, "E372", {"start": v(-32.12, -31.3) * mm, "end": v(-31.73, -31.1) * mm});
            skLineSegment(sketch, "E373", {"start": v(-31.73, -31.1) * mm, "end": v(-31.34, -30.89) * mm});
            skLineSegment(sketch, "E374", {"start": v(-31.34, -30.89) * mm, "end": v(-30.94, -30.68) * mm});
            skLineSegment(sketch, "E375", {"start": v(-30.94, -30.68) * mm, "end": v(-30.55, -30.48) * mm});
            skLineSegment(sketch, "E376", {"start": v(-30.55, -30.48) * mm, "end": v(-30.16, -30.27) * mm});
            skLineSegment(sketch, "E377", {"start": v(-30.16, -30.27) * mm, "end": v(-29.82, -30.57) * mm});
            skLineSegment(sketch, "E378", {"start": v(-29.82, -30.57) * mm, "end": v(-29.48, -30.86) * mm});
            skLineSegment(sketch, "E379", {"start": v(-29.48, -30.86) * mm, "end": v(-29.15, -31.15) * mm});
            skLineSegment(sketch, "E380", {"start": v(-29.15, -31.15) * mm, "end": v(-28.8, -31.44) * mm});
            skLineSegment(sketch, "E381", {"start": v(-28.8, -31.44) * mm, "end": v(-28.47, -31.73) * mm});
            skLineSegment(sketch, "E382", {"start": v(-28.47, -31.73) * mm, "end": v(-28.13, -32.02) * mm});
            skLineSegment(sketch, "E383", {"start": v(-28.13, -32.02) * mm, "end": v(-27.8, -32.31) * mm});
            skLineSegment(sketch, "E384", {"start": v(-27.8, -32.31) * mm, "end": v(-27.46, -32.6) * mm});
            skLineSegment(sketch, "E385", {"start": v(-27.46, -32.6) * mm, "end": v(-27.12, -32.9) * mm});
            skLineSegment(sketch, "E386", {"start": v(-27.12, -32.9) * mm, "end": v(-26.78, -33.18) * mm});
            skLineSegment(sketch, "E387", {"start": v(-26.78, -33.18) * mm, "end": v(-26.45, -33.48) * mm});
            skLineSegment(sketch, "E388", {"start": v(-26.45, -33.48) * mm, "end": v(-26.1, -33.77) * mm});
            skLineSegment(sketch, "E389", {"start": v(-26.1, -33.77) * mm, "end": v(-25.77, -34.06) * mm});
            skLineSegment(sketch, "E390", {"start": v(-25.77, -34.06) * mm, "end": v(-25.51, -34.28) * mm});
            skLineSegment(sketch, "E391", {"start": v(-25.51, -34.28) * mm, "end": v(-25.8, -34.63) * mm});
            skLineSegment(sketch, "E392", {"start": v(-25.8, -34.63) * mm, "end": v(-26.07, -34.97) * mm});
            skLineSegment(sketch, "E393", {"start": v(-26.07, -34.97) * mm, "end": v(-26.36, -35.32) * mm});
            skLineSegment(sketch, "E394", {"start": v(-26.36, -35.32) * mm, "end": v(-26.64, -35.67) * mm});
            skLineSegment(sketch, "E395", {"start": v(-26.64, -35.67) * mm, "end": v(-26.92, -36.01) * mm});
            skLineSegment(sketch, "E396", {"start": v(-26.92, -36.01) * mm, "end": v(-27.2, -36.36) * mm});
            skLineSegment(sketch, "E397", {"start": v(-27.2, -36.36) * mm, "end": v(-27.48, -36.7) * mm});
            skLineSegment(sketch, "E398", {"start": v(-27.48, -36.7) * mm, "end": v(-27.76, -37.05) * mm});
            skLineSegment(sketch, "E399", {"start": v(-27.76, -37.05) * mm, "end": v(-28.04, -37.4) * mm});
            skLineSegment(sketch, "E400", {"start": v(-28.04, -37.4) * mm, "end": v(-28.32, -37.74) * mm});
            skLineSegment(sketch, "E401", {"start": v(-28.32, -37.74) * mm, "end": v(-28.6, -38.09) * mm});
            skLineSegment(sketch, "E402", {"start": v(-28.6, -38.09) * mm, "end": v(-28.88, -38.44) * mm});
            skLineSegment(sketch, "E403", {"start": v(-28.88, -38.44) * mm, "end": v(-29.16, -38.78) * mm});
            skLineSegment(sketch, "E404", {"start": v(-29.16, -38.78) * mm, "end": v(-29.44, -39.13) * mm});
            skLineSegment(sketch, "E405", {"start": v(-29.44, -39.13) * mm, "end": v(-29.72, -39.47) * mm});
            skLineSegment(sketch, "E406", {"start": v(-29.72, -39.47) * mm, "end": v(-30, -39.82) * mm});
            skLineSegment(sketch, "E407", {"start": v(-30, -39.82) * mm, "end": v(-30.1, -39.93) * mm});
            skLineSegment(sketch, "E408", {"start": v(-30.1, -39.93) * mm, "end": v(-29.73, -40.2) * mm});
            skLineSegment(sketch, "E409", {"start": v(-29.73, -40.2) * mm, "end": v(-29.37, -40.46) * mm});
            skLineSegment(sketch, "E410", {"start": v(-29.37, -40.46) * mm, "end": v(-29.04, -40.7) * mm});
            skLineSegment(sketch, "E411", {"start": v(-29.04, -40.7) * mm, "end": v(-28.7, -40.42) * mm});
            skLineSegment(sketch, "E412", {"start": v(-28.7, -40.42) * mm, "end": v(-28.35, -40.14) * mm});
            skLineSegment(sketch, "E413", {"start": v(-28.35, -40.14) * mm, "end": v(-28, -39.85) * mm});
            skLineSegment(sketch, "E414", {"start": v(-28, -39.85) * mm, "end": v(-27.66, -39.57) * mm});
            skLineSegment(sketch, "E415", {"start": v(-27.66, -39.57) * mm, "end": v(-27.32, -39.29) * mm});
            skLineSegment(sketch, "E416", {"start": v(-27.32, -39.29) * mm, "end": v(-26.98, -39) * mm});
            skLineSegment(sketch, "E417", {"start": v(-26.98, -39) * mm, "end": v(-26.63, -38.72) * mm});
            skLineSegment(sketch, "E418", {"start": v(-26.63, -38.72) * mm, "end": v(-26.29, -38.43) * mm});
            skLineSegment(sketch, "E419", {"start": v(-26.29, -38.43) * mm, "end": v(-25.94, -38.15) * mm});
            skLineSegment(sketch, "E420", {"start": v(-25.94, -38.15) * mm, "end": v(-25.6, -37.87) * mm});
            skLineSegment(sketch, "E421", {"start": v(-25.6, -37.87) * mm, "end": v(-25.26, -37.58) * mm});
            skLineSegment(sketch, "E422", {"start": v(-25.26, -37.58) * mm, "end": v(-24.91, -37.3) * mm});
            skLineSegment(sketch, "E423", {"start": v(-24.91, -37.3) * mm, "end": v(-24.57, -37.01) * mm});
            skLineSegment(sketch, "E424", {"start": v(-24.57, -37.01) * mm, "end": v(-24.23, -36.73) * mm});
            skLineSegment(sketch, "E425", {"start": v(-24.23, -36.73) * mm, "end": v(-23.88, -36.44) * mm});
            skLineSegment(sketch, "E426", {"start": v(-23.88, -36.44) * mm, "end": v(-23.54, -36.16) * mm});
            skLineSegment(sketch, "E427", {"start": v(-23.54, -36.16) * mm, "end": v(-23.2, -35.88) * mm});
            skLineSegment(sketch, "E428", {"start": v(-23.2, -35.88) * mm, "end": v(-22.82, -36.1) * mm});
            skLineSegment(sketch, "E429", {"start": v(-22.82, -36.1) * mm, "end": v(-22.42, -36.31) * mm});
            skLineSegment(sketch, "E430", {"start": v(-22.42, -36.31) * mm, "end": v(-22.03, -36.53) * mm});
            skLineSegment(sketch, "E431", {"start": v(-22.03, -36.53) * mm, "end": v(-21.64, -36.74) * mm});
            skLineSegment(sketch, "E432", {"start": v(-21.64, -36.74) * mm, "end": v(-21.25, -36.96) * mm});
            skLineSegment(sketch, "E433", {"start": v(-21.25, -36.96) * mm, "end": v(-20.86, -37.17) * mm});
            skLineSegment(sketch, "E434", {"start": v(-20.86, -37.17) * mm, "end": v(-20.47, -37.38) * mm});
            skLineSegment(sketch, "E435", {"start": v(-20.47, -37.38) * mm, "end": v(-20.08, -37.6) * mm});
            skLineSegment(sketch, "E436", {"start": v(-20.08, -37.6) * mm, "end": v(-19.7, -37.81) * mm});
            skLineSegment(sketch, "E437", {"start": v(-19.7, -37.81) * mm, "end": v(-19.3, -38.03) * mm});
            skLineSegment(sketch, "E438", {"start": v(-19.3, -38.03) * mm, "end": v(-18.9, -38.24) * mm});
            skLineSegment(sketch, "E439", {"start": v(-18.9, -38.24) * mm, "end": v(-18.52, -38.46) * mm});
            skLineSegment(sketch, "E440", {"start": v(-18.52, -38.46) * mm, "end": v(-18.13, -38.67) * mm});
            skLineSegment(sketch, "E441", {"start": v(-18.13, -38.67) * mm, "end": v(-17.83, -38.84) * mm});
            skLineSegment(sketch, "E442", {"start": v(-17.83, -38.84) * mm, "end": v(-18.03, -39.23) * mm});
            skLineSegment(sketch, "E443", {"start": v(-18.03, -39.23) * mm, "end": v(-18.23, -39.63) * mm});
            skLineSegment(sketch, "E444", {"start": v(-18.23, -39.63) * mm, "end": v(-18.44, -40.03) * mm});
            skLineSegment(sketch, "E445", {"start": v(-18.44, -40.03) * mm, "end": v(-18.64, -40.42) * mm});
            skLineSegment(sketch, "E446", {"start": v(-18.64, -40.42) * mm, "end": v(-18.84, -40.82) * mm});
            skLineSegment(sketch, "E447", {"start": v(-18.84, -40.82) * mm, "end": v(-19.04, -41.22) * mm});
            skLineSegment(sketch, "E448", {"start": v(-19.04, -41.22) * mm, "end": v(-19.25, -41.61) * mm});
            skLineSegment(sketch, "E449", {"start": v(-19.25, -41.61) * mm, "end": v(-19.45, -42.01) * mm});
            skLineSegment(sketch, "E450", {"start": v(-19.45, -42.01) * mm, "end": v(-19.65, -42.4) * mm});
            skLineSegment(sketch, "E451", {"start": v(-19.65, -42.4) * mm, "end": v(-19.85, -42.8) * mm});
            skLineSegment(sketch, "E452", {"start": v(-19.85, -42.8) * mm, "end": v(-20.05, -43.2) * mm});
            skLineSegment(sketch, "E453", {"start": v(-20.05, -43.2) * mm, "end": v(-20.26, -43.6) * mm});
            skLineSegment(sketch, "E454", {"start": v(-20.26, -43.6) * mm, "end": v(-20.46, -44) * mm});
            skLineSegment(sketch, "E455", {"start": v(-20.46, -44) * mm, "end": v(-20.66, -44.4) * mm});
            skLineSegment(sketch, "E456", {"start": v(-20.66, -44.4) * mm, "end": v(-20.86, -44.8) * mm});
            skLineSegment(sketch, "E457", {"start": v(-20.86, -44.8) * mm, "end": v(-21.07, -45.19) * mm});
            skLineSegment(sketch, "E458", {"start": v(-21.07, -45.19) * mm, "end": v(-21.13, -45.32) * mm});
            skLineSegment(sketch, "E459", {"start": v(-21.13, -45.32) * mm, "end": v(-20.72, -45.5) * mm});
            skLineSegment(sketch, "E460", {"start": v(-20.72, -45.5) * mm, "end": v(-20.32, -45.68) * mm});
            skLineSegment(sketch, "E461", {"start": v(-20.32, -45.68) * mm, "end": v(-19.94, -45.85) * mm});
            skLineSegment(sketch, "E462", {"start": v(-19.94, -45.85) * mm, "end": v(-19.66, -45.5) * mm});
            skLineSegment(sketch, "E463", {"start": v(-19.66, -45.5) * mm, "end": v(-19.38, -45.15) * mm});
            skLineSegment(sketch, "E464", {"start": v(-19.38, -45.15) * mm, "end": v(-19.1, -44.8) * mm});
            skLineSegment(sketch, "E465", {"start": v(-19.1, -44.8) * mm, "end": v(-18.83, -44.46) * mm});
            skLineSegment(sketch, "E466", {"start": v(-18.83, -44.46) * mm, "end": v(-18.55, -44.1) * mm});
            skLineSegment(sketch, "E467", {"start": v(-18.55, -44.1) * mm, "end": v(-18.28, -43.76) * mm});
            skLineSegment(sketch, "E468", {"start": v(-18.28, -43.76) * mm, "end": v(-18, -43.4) * mm});
            skLineSegment(sketch, "E469", {"start": v(-18, -43.4) * mm, "end": v(-17.72, -43.06) * mm});
            skLineSegment(sketch, "E470", {"start": v(-17.72, -43.06) * mm, "end": v(-17.45, -42.7) * mm});
            skLineSegment(sketch, "E471", {"start": v(-17.45, -42.7) * mm, "end": v(-17.17, -42.36) * mm});
            skLineSegment(sketch, "E472", {"start": v(-17.17, -42.36) * mm, "end": v(-16.9, -42.01) * mm});
            skLineSegment(sketch, "E473", {"start": v(-16.9, -42.01) * mm, "end": v(-16.62, -41.66) * mm});
            skLineSegment(sketch, "E474", {"start": v(-16.62, -41.66) * mm, "end": v(-16.34, -41.31) * mm});
            skLineSegment(sketch, "E475", {"start": v(-16.34, -41.31) * mm, "end": v(-16.06, -40.96) * mm});
            skLineSegment(sketch, "E476", {"start": v(-16.06, -40.96) * mm, "end": v(-15.79, -40.61) * mm});
            skLineSegment(sketch, "E477", {"start": v(-15.79, -40.61) * mm, "end": v(-15.5, -40.27) * mm});
            skLineSegment(sketch, "E478", {"start": v(-15.5, -40.27) * mm, "end": v(-15.24, -39.92) * mm});
            skLineSegment(sketch, "E479", {"start": v(-15.24, -39.92) * mm, "end": v(-14.81, -40.05) * mm});
            skLineSegment(sketch, "E480", {"start": v(-14.81, -40.05) * mm, "end": v(-14.38, -40.18) * mm});
            skLineSegment(sketch, "E481", {"start": v(-14.38, -40.18) * mm, "end": v(-13.96, -40.3) * mm});
            skLineSegment(sketch, "E482", {"start": v(-13.96, -40.3) * mm, "end": v(-13.53, -40.44) * mm});
            skLineSegment(sketch, "E483", {"start": v(-13.53, -40.44) * mm, "end": v(-13.1, -40.57) * mm});
            skLineSegment(sketch, "E484", {"start": v(-13.1, -40.57) * mm, "end": v(-12.68, -40.7) * mm});
            skLineSegment(sketch, "E485", {"start": v(-12.68, -40.7) * mm, "end": v(-12.25, -40.82) * mm});
            skLineSegment(sketch, "E486", {"start": v(-12.25, -40.82) * mm, "end": v(-11.82, -40.95) * mm});
            skLineSegment(sketch, "E487", {"start": v(-11.82, -40.95) * mm, "end": v(-11.4, -41.08) * mm});
            skLineSegment(sketch, "E488", {"start": v(-11.4, -41.08) * mm, "end": v(-10.97, -41.2) * mm});
            skLineSegment(sketch, "E489", {"start": v(-10.97, -41.2) * mm, "end": v(-10.54, -41.34) * mm});
            skLineSegment(sketch, "E490", {"start": v(-10.54, -41.34) * mm, "end": v(-10.12, -41.47) * mm});
            skLineSegment(sketch, "E491", {"start": v(-10.12, -41.47) * mm, "end": v(-9.7, -41.6) * mm});
            skLineSegment(sketch, "E492", {"start": v(-9.7, -41.6) * mm, "end": v(-9.37, -41.7) * mm});
            skLineSegment(sketch, "E493", {"start": v(-9.37, -41.7) * mm, "end": v(-9.48, -42.12) * mm});
            skLineSegment(sketch, "E494", {"start": v(-9.48, -42.12) * mm, "end": v(-9.6, -42.55) * mm});
            skLineSegment(sketch, "E495", {"start": v(-9.6, -42.55) * mm, "end": v(-9.71, -42.99) * mm});
            skLineSegment(sketch, "E496", {"start": v(-9.71, -42.99) * mm, "end": v(-9.83, -43.42) * mm});
            skLineSegment(sketch, "E497", {"start": v(-9.83, -43.42) * mm, "end": v(-9.94, -43.85) * mm});
            skLineSegment(sketch, "E498", {"start": v(-9.94, -43.85) * mm, "end": v(-10.06, -44.28) * mm});
            skLineSegment(sketch, "E499", {"start": v(-10.06, -44.28) * mm, "end": v(-10.17, -44.7) * mm});
            skLineSegment(sketch, "E500", {"start": v(-10.17, -44.7) * mm, "end": v(-10.29, -45.14) * mm});
            skLineSegment(sketch, "E501", {"start": v(-10.29, -45.14) * mm, "end": v(-10.4, -45.57) * mm});
            skLineSegment(sketch, "E502", {"start": v(-10.4, -45.57) * mm, "end": v(-10.52, -46) * mm});
            skLineSegment(sketch, "E503", {"start": v(-10.52, -46) * mm, "end": v(-10.63, -46.43) * mm});
            skLineSegment(sketch, "E504", {"start": v(-10.63, -46.43) * mm, "end": v(-10.75, -46.86) * mm});
            skLineSegment(sketch, "E505", {"start": v(-10.75, -46.86) * mm, "end": v(-10.86, -47.29) * mm});
            skLineSegment(sketch, "E506", {"start": v(-10.86, -47.29) * mm, "end": v(-10.98, -47.72) * mm});
            skLineSegment(sketch, "E507", {"start": v(-10.98, -47.72) * mm, "end": v(-11.1, -48.15) * mm});
            skLineSegment(sketch, "E508", {"start": v(-11.1, -48.15) * mm, "end": v(-11.21, -48.58) * mm});
            skLineSegment(sketch, "E509", {"start": v(-11.21, -48.58) * mm, "end": v(-11.25, -48.72) * mm});
            skLineSegment(sketch, "E510", {"start": v(-11.25, -48.72) * mm, "end": v(-10.81, -48.81) * mm});
            skLineSegment(sketch, "E511", {"start": v(-10.81, -48.81) * mm, "end": v(-10.38, -48.9) * mm});
            skLineSegment(sketch, "E512", {"start": v(-10.38, -48.9) * mm, "end": v(-9.97, -49) * mm});
            skLineSegment(sketch, "E513", {"start": v(-9.97, -49) * mm, "end": v(-9.77, -48.6) * mm});
            skLineSegment(sketch, "E514", {"start": v(-9.77, -48.6) * mm, "end": v(-9.57, -48.2) * mm});
            skLineSegment(sketch, "E515", {"start": v(-9.57, -48.2) * mm, "end": v(-9.37, -47.8) * mm});
            skLineSegment(sketch, "E516", {"start": v(-9.37, -47.8) * mm, "end": v(-9.18, -47.4) * mm});
            skLineSegment(sketch, "E517", {"start": v(-9.18, -47.4) * mm, "end": v(-8.98, -47) * mm});
            skLineSegment(sketch, "E518", {"start": v(-8.98, -47) * mm, "end": v(-8.78, -46.6) * mm});
            skLineSegment(sketch, "E519", {"start": v(-8.78, -46.6) * mm, "end": v(-8.58, -46.2) * mm});
            skLineSegment(sketch, "E520", {"start": v(-8.58, -46.2) * mm, "end": v(-8.38, -45.8) * mm});
            skLineSegment(sketch, "E521", {"start": v(-8.38, -45.8) * mm, "end": v(-8.19, -45.4) * mm});
            skLineSegment(sketch, "E522", {"start": v(-8.19, -45.4) * mm, "end": v(-7.99, -45) * mm});
            skLineSegment(sketch, "E523", {"start": v(-7.99, -45) * mm, "end": v(-7.79, -44.6) * mm});
            skLineSegment(sketch, "E524", {"start": v(-7.79, -44.6) * mm, "end": v(-7.6, -44.2) * mm});
            skLineSegment(sketch, "E525", {"start": v(-7.6, -44.2) * mm, "end": v(-7.4, -43.8) * mm});
            skLineSegment(sketch, "E526", {"start": v(-7.4, -43.8) * mm, "end": v(-7.2, -43.4) * mm});
            skLineSegment(sketch, "E527", {"start": v(-7.2, -43.4) * mm, "end": v(-7, -43) * mm});
            skLineSegment(sketch, "E528", {"start": v(-7, -43) * mm, "end": v(-6.8, -42.6) * mm});
            skLineSegment(sketch, "E529", {"start": v(-6.8, -42.6) * mm, "end": v(-6.6, -42.22) * mm});
            skLineSegment(sketch, "E530", {"start": v(-6.6, -42.22) * mm, "end": v(-6.16, -42.26) * mm});
            skLineSegment(sketch, "E531", {"start": v(-6.16, -42.26) * mm, "end": v(-5.72, -42.3) * mm});
            skLineSegment(sketch, "E532", {"start": v(-5.72, -42.3) * mm, "end": v(-5.27, -42.33) * mm});
            skLineSegment(sketch, "E533", {"start": v(-5.27, -42.33) * mm, "end": v(-4.83, -42.37) * mm});
            skLineSegment(sketch, "E534", {"start": v(-4.83, -42.37) * mm, "end": v(-4.38, -42.4) * mm});
            skLineSegment(sketch, "E535", {"start": v(-4.38, -42.4) * mm, "end": v(-3.94, -42.44) * mm});
            skLineSegment(sketch, "E536", {"start": v(-3.94, -42.44) * mm, "end": v(-3.5, -42.48) * mm});
            skLineSegment(sketch, "E537", {"start": v(-3.5, -42.48) * mm, "end": v(-3.05, -42.52) * mm});
            skLineSegment(sketch, "E538", {"start": v(-3.05, -42.52) * mm, "end": v(-2.6, -42.55) * mm});
            skLineSegment(sketch, "E539", {"start": v(-2.6, -42.55) * mm, "end": v(-2.16, -42.6) * mm});
            skLineSegment(sketch, "E540", {"start": v(-2.16, -42.6) * mm, "end": v(-1.72, -42.63) * mm});
            skLineSegment(sketch, "E541", {"start": v(-1.72, -42.63) * mm, "end": v(-1.28, -42.66) * mm});
            skLineSegment(sketch, "E542", {"start": v(-1.28, -42.66) * mm, "end": v(-0.83, -42.7) * mm});
            skLineSegment(sketch, "E543", {"start": v(-0.83, -42.7) * mm, "end": v(-0.5, -42.73) * mm});
            skLineSegment(sketch, "E544", {"start": v(-0.5, -42.73) * mm, "end": v(-0.52, -43.17) * mm});
            skLineSegment(sketch, "E545", {"start": v(-0.52, -43.17) * mm, "end": v(-0.54, -43.62) * mm});
            skLineSegment(sketch, "E546", {"start": v(-0.54, -43.62) * mm, "end": v(-0.56, -44.06) * mm});
            skLineSegment(sketch, "E547", {"start": v(-0.56, -44.06) * mm, "end": v(-0.59, -44.5) * mm});
            skLineSegment(sketch, "E548", {"start": v(-0.59, -44.5) * mm, "end": v(-0.6, -44.95) * mm});
            skLineSegment(sketch, "E549", {"start": v(-0.6, -44.95) * mm, "end": v(-0.63, -45.4) * mm});
            skLineSegment(sketch, "E550", {"start": v(-0.63, -45.4) * mm, "end": v(-0.66, -45.84) * mm});
            skLineSegment(sketch, "E551", {"start": v(-0.66, -45.84) * mm, "end": v(-0.68, -46.29) * mm});
            skLineSegment(sketch, "E552", {"start": v(-0.68, -46.29) * mm, "end": v(-0.7, -46.73) * mm});
            skLineSegment(sketch, "E553", {"start": v(-0.7, -46.73) * mm, "end": v(-0.73, -47.18) * mm});
            skLineSegment(sketch, "E554", {"start": v(-0.73, -47.18) * mm, "end": v(-0.75, -47.62) * mm});
            skLineSegment(sketch, "E555", {"start": v(-0.75, -47.62) * mm, "end": v(-0.77, -48.07) * mm});
            skLineSegment(sketch, "E556", {"start": v(-0.77, -48.07) * mm, "end": v(-0.8, -48.52) * mm});
            skLineSegment(sketch, "E557", {"start": v(-0.8, -48.52) * mm, "end": v(-0.82, -48.96) * mm});
            skLineSegment(sketch, "E558", {"start": v(-0.82, -48.96) * mm, "end": v(-0.84, -49.4) * mm});
            skLineSegment(sketch, "E559", {"start": v(-0.84, -49.4) * mm, "end": v(-0.87, -49.85) * mm});
            skLineSegment(sketch, "E560", {"start": v(-0.87, -49.85) * mm, "end": v(-0.87, -50) * mm});
            skLineSegment(sketch, "E561", {"start": v(-0.87, -50) * mm, "end": v(-0.43, -50) * mm});
            skLineSegment(sketch, "E562", {"start": v(-0.43, -50) * mm, "end": v(0.02, -50) * mm});
            skLineSegment(sketch, "E563", {"start": v(0.02, -50) * mm, "end": v(0.44, -50) * mm});
            skLineSegment(sketch, "E564", {"start": v(0.44, -50) * mm, "end": v(0.55, -49.57) * mm});
            skLineSegment(sketch, "E565", {"start": v(0.55, -49.57) * mm, "end": v(0.66, -49.13) * mm});
            skLineSegment(sketch, "E566", {"start": v(0.66, -49.13) * mm, "end": v(0.77, -48.7) * mm});
            skLineSegment(sketch, "E567", {"start": v(0.77, -48.7) * mm, "end": v(0.88, -48.27) * mm});
            skLineSegment(sketch, "E568", {"start": v(0.88, -48.27) * mm, "end": v(1, -47.84) * mm});
            skLineSegment(sketch, "E569", {"start": v(1, -47.84) * mm, "end": v(1.1, -47.4) * mm});
            skLineSegment(sketch, "E570", {"start": v(1.1, -47.4) * mm, "end": v(1.21, -46.98) * mm});
            skLineSegment(sketch, "E571", {"start": v(1.21, -46.98) * mm, "end": v(1.32, -46.55) * mm});
            skLineSegment(sketch, "E572", {"start": v(1.32, -46.55) * mm, "end": v(1.43, -46.11) * mm});
            skLineSegment(sketch, "E573", {"start": v(1.43, -46.11) * mm, "end": v(1.54, -45.68) * mm});
            skLineSegment(sketch, "E574", {"start": v(1.54, -45.68) * mm, "end": v(1.66, -45.25) * mm});
            skLineSegment(sketch, "E575", {"start": v(1.66, -45.25) * mm, "end": v(1.77, -44.82) * mm});
            skLineSegment(sketch, "E576", {"start": v(1.77, -44.82) * mm, "end": v(1.88, -44.39) * mm});
            skLineSegment(sketch, "E577", {"start": v(1.88, -44.39) * mm, "end": v(1.99, -43.96) * mm});
            skLineSegment(sketch, "E578", {"start": v(1.99, -43.96) * mm, "end": v(2.1, -43.52) * mm});
            skLineSegment(sketch, "E579", {"start": v(2.1, -43.52) * mm, "end": v(2.2, -43.1) * mm});
            skLineSegment(sketch, "E580", {"start": v(2.2, -43.1) * mm, "end": v(2.32, -42.67) * mm});
            skLineSegment(sketch, "E581", {"start": v(2.32, -42.67) * mm, "end": v(2.76, -42.61) * mm});
            skLineSegment(sketch, "E582", {"start": v(2.76, -42.61) * mm, "end": v(3.2, -42.56) * mm});
            skLineSegment(sketch, "E583", {"start": v(3.2, -42.56) * mm, "end": v(3.64, -42.5) * mm});
            skLineSegment(sketch, "E584", {"start": v(3.64, -42.5) * mm, "end": v(4.09, -42.45) * mm});
            skLineSegment(sketch, "E585", {"start": v(4.09, -42.45) * mm, "end": v(4.53, -42.39) * mm});
            skLineSegment(sketch, "E586", {"start": v(4.53, -42.39) * mm, "end": v(4.97, -42.33) * mm});
            skLineSegment(sketch, "E587", {"start": v(4.97, -42.33) * mm, "end": v(5.41, -42.28) * mm});
            skLineSegment(sketch, "E588", {"start": v(5.41, -42.28) * mm, "end": v(5.85, -42.22) * mm});
            skLineSegment(sketch, "E589", {"start": v(5.85, -42.22) * mm, "end": v(6.3, -42.17) * mm});
            skLineSegment(sketch, "E590", {"start": v(6.3, -42.17) * mm, "end": v(6.74, -42.1) * mm});
            skLineSegment(sketch, "E591", {"start": v(6.74, -42.1) * mm, "end": v(7.18, -42.05) * mm});
            skLineSegment(sketch, "E592", {"start": v(7.18, -42.05) * mm, "end": v(7.62, -42) * mm});
            skLineSegment(sketch, "E593", {"start": v(7.62, -42) * mm, "end": v(8.06, -41.94) * mm});
            skLineSegment(sketch, "E594", {"start": v(8.06, -41.94) * mm, "end": v(8.4, -41.9) * mm});
            skLineSegment(sketch, "E595", {"start": v(8.4, -41.9) * mm, "end": v(8.47, -42.34) * mm});
            skLineSegment(sketch, "E596", {"start": v(8.47, -42.34) * mm, "end": v(8.54, -42.78) * mm});
            skLineSegment(sketch, "E597", {"start": v(8.54, -42.78) * mm, "end": v(8.61, -43.22) * mm});
            skLineSegment(sketch, "E598", {"start": v(8.61, -43.22) * mm, "end": v(8.68, -43.66) * mm});
            skLineSegment(sketch, "E599", {"start": v(8.68, -43.66) * mm, "end": v(8.75, -44.1) * mm});
            skLineSegment(sketch, "E600", {"start": v(8.75, -44.1) * mm, "end": v(8.82, -44.54) * mm});
            skLineSegment(sketch, "E601", {"start": v(8.82, -44.54) * mm, "end": v(8.9, -44.98) * mm});
            skLineSegment(sketch, "E602", {"start": v(8.9, -44.98) * mm, "end": v(8.96, -45.42) * mm});
            skLineSegment(sketch, "E603", {"start": v(8.96, -45.42) * mm, "end": v(9.03, -45.86) * mm});
            skLineSegment(sketch, "E604", {"start": v(9.03, -45.86) * mm, "end": v(9.1, -46.3) * mm});
            skLineSegment(sketch, "E605", {"start": v(9.1, -46.3) * mm, "end": v(9.17, -46.74) * mm});
            skLineSegment(sketch, "E606", {"start": v(9.17, -46.74) * mm, "end": v(9.24, -47.18) * mm});
            skLineSegment(sketch, "E607", {"start": v(9.24, -47.18) * mm, "end": v(9.3, -47.62) * mm});
            skLineSegment(sketch, "E608", {"start": v(9.3, -47.62) * mm, "end": v(9.38, -48.06) * mm});
            skLineSegment(sketch, "E609", {"start": v(9.38, -48.06) * mm, "end": v(9.45, -48.5) * mm});
            skLineSegment(sketch, "E610", {"start": v(9.45, -48.5) * mm, "end": v(9.52, -48.94) * mm});
            skLineSegment(sketch, "E611", {"start": v(9.52, -48.94) * mm, "end": v(9.54, -49.08) * mm});
            skLineSegment(sketch, "E612", {"start": v(9.54, -49.08) * mm, "end": v(9.98, -49) * mm});
            skLineSegment(sketch, "E613", {"start": v(9.98, -49) * mm, "end": v(10.41, -48.9) * mm});
            skLineSegment(sketch, "E614", {"start": v(10.41, -48.9) * mm, "end": v(10.82, -48.81) * mm});
            skLineSegment(sketch, "E615", {"start": v(10.82, -48.81) * mm, "end": v(10.84, -48.37) * mm});
            skLineSegment(sketch, "E616", {"start": v(10.84, -48.37) * mm, "end": v(10.86, -47.92) * mm});
            skLineSegment(sketch, "E617", {"start": v(10.86, -47.92) * mm, "end": v(10.88, -47.48) * mm});
            skLineSegment(sketch, "E618", {"start": v(10.88, -47.48) * mm, "end": v(10.9, -47.03) * mm});
            skLineSegment(sketch, "E619", {"start": v(10.9, -47.03) * mm, "end": v(10.92, -46.59) * mm});
            skLineSegment(sketch, "E620", {"start": v(10.92, -46.59) * mm, "end": v(10.93, -46.14) * mm});
            skLineSegment(sketch, "E621", {"start": v(10.93, -46.14) * mm, "end": v(10.95, -45.7) * mm});
            skLineSegment(sketch, "E622", {"start": v(10.95, -45.7) * mm, "end": v(10.97, -45.25) * mm});
            skLineSegment(sketch, "E623", {"start": v(10.97, -45.25) * mm, "end": v(10.99, -44.8) * mm});
            skLineSegment(sketch, "E624", {"start": v(10.99, -44.8) * mm, "end": v(11, -44.36) * mm});
            skLineSegment(sketch, "E625", {"start": v(11, -44.36) * mm, "end": v(11.03, -43.92) * mm});
            skLineSegment(sketch, "E626", {"start": v(11.03, -43.92) * mm, "end": v(11.05, -43.47) * mm});
            skLineSegment(sketch, "E627", {"start": v(11.05, -43.47) * mm, "end": v(11.06, -43.03) * mm});
            skLineSegment(sketch, "E628", {"start": v(11.06, -43.03) * mm, "end": v(11.08, -42.58) * mm});
            skLineSegment(sketch, "E629", {"start": v(11.08, -42.58) * mm, "end": v(11.1, -42.14) * mm});
            skLineSegment(sketch, "E630", {"start": v(11.1, -42.14) * mm, "end": v(11.12, -41.7) * mm});
            skLineSegment(sketch, "E631", {"start": v(11.12, -41.7) * mm, "end": v(11.14, -41.26) * mm});
            skLineSegment(sketch, "E632", {"start": v(11.14, -41.26) * mm, "end": v(11.56, -41.1) * mm});
            skLineSegment(sketch, "E633", {"start": v(11.56, -41.1) * mm, "end": v(11.98, -40.96) * mm});
            skLineSegment(sketch, "E634", {"start": v(11.98, -40.96) * mm, "end": v(12.4, -40.82) * mm});
            skLineSegment(sketch, "E635", {"start": v(12.4, -40.82) * mm, "end": v(12.82, -40.67) * mm});
            skLineSegment(sketch, "E636", {"start": v(12.82, -40.67) * mm, "end": v(13.24, -40.52) * mm});
            skLineSegment(sketch, "E637", {"start": v(13.24, -40.52) * mm, "end": v(13.66, -40.38) * mm});
            skLineSegment(sketch, "E638", {"start": v(13.66, -40.38) * mm, "end": v(14.08, -40.23) * mm});
            skLineSegment(sketch, "E639", {"start": v(14.08, -40.23) * mm, "end": v(14.5, -40.08) * mm});
            skLineSegment(sketch, "E640", {"start": v(14.5, -40.08) * mm, "end": v(14.93, -39.93) * mm});
            skLineSegment(sketch, "E641", {"start": v(14.93, -39.93) * mm, "end": v(15.35, -39.79) * mm});
            skLineSegment(sketch, "E642", {"start": v(15.35, -39.79) * mm, "end": v(15.77, -39.64) * mm});
            skLineSegment(sketch, "E643", {"start": v(15.77, -39.64) * mm, "end": v(16.19, -39.5) * mm});
            skLineSegment(sketch, "E644", {"start": v(16.19, -39.5) * mm, "end": v(16.6, -39.35) * mm});
            skLineSegment(sketch, "E645", {"start": v(16.6, -39.35) * mm, "end": v(16.93, -39.24) * mm});
            skLineSegment(sketch, "E646", {"start": v(16.93, -39.24) * mm, "end": v(17.09, -39.65) * mm});
            skLineSegment(sketch, "E647", {"start": v(17.09, -39.65) * mm, "end": v(17.25, -40.07) * mm});
            skLineSegment(sketch, "E648", {"start": v(17.25, -40.07) * mm, "end": v(17.4, -40.48) * mm});
            skLineSegment(sketch, "E649", {"start": v(17.4, -40.48) * mm, "end": v(17.57, -40.9) * mm});
            skLineSegment(sketch, "E650", {"start": v(17.57, -40.9) * mm, "end": v(17.73, -41.32) * mm});
            skLineSegment(sketch, "E651", {"start": v(17.73, -41.32) * mm, "end": v(17.89, -41.73) * mm});
            skLineSegment(sketch, "E652", {"start": v(17.89, -41.73) * mm, "end": v(18.05, -42.15) * mm});
            skLineSegment(sketch, "E653", {"start": v(18.05, -42.15) * mm, "end": v(18.2, -42.56) * mm});
            skLineSegment(sketch, "E654", {"start": v(18.2, -42.56) * mm, "end": v(18.37, -42.98) * mm});
            skLineSegment(sketch, "E655", {"start": v(18.37, -42.98) * mm, "end": v(18.53, -43.4) * mm});
            skLineSegment(sketch, "E656", {"start": v(18.53, -43.4) * mm, "end": v(18.69, -43.81) * mm});
            skLineSegment(sketch, "E657", {"start": v(18.69, -43.81) * mm, "end": v(18.85, -44.23) * mm});
            skLineSegment(sketch, "E658", {"start": v(18.85, -44.23) * mm, "end": v(19, -44.64) * mm});
            skLineSegment(sketch, "E659", {"start": v(19, -44.64) * mm, "end": v(19.17, -45.06) * mm});
            skLineSegment(sketch, "E660", {"start": v(19.17, -45.06) * mm, "end": v(19.33, -45.48) * mm});
            skLineSegment(sketch, "E661", {"start": v(19.33, -45.48) * mm, "end": v(19.49, -45.9) * mm});
            skLineSegment(sketch, "E662", {"start": v(19.49, -45.9) * mm, "end": v(19.54, -46.03) * mm});
            skLineSegment(sketch, "E663", {"start": v(19.54, -46.03) * mm, "end": v(19.94, -45.85) * mm});
            skLineSegment(sketch, "E664", {"start": v(19.94, -45.85) * mm, "end": v(20.35, -45.67) * mm});
            skLineSegment(sketch, "E665", {"start": v(20.35, -45.67) * mm, "end": v(20.73, -45.5) * mm});
            skLineSegment(sketch, "E666", {"start": v(20.73, -45.5) * mm, "end": v(20.66, -45.06) * mm});
            skLineSegment(sketch, "E667", {"start": v(20.66, -45.06) * mm, "end": v(20.59, -44.62) * mm});
            skLineSegment(sketch, "E668", {"start": v(20.59, -44.62) * mm, "end": v(20.51, -44.18) * mm});
            skLineSegment(sketch, "E669", {"start": v(20.51, -44.18) * mm, "end": v(20.44, -43.74) * mm});
            skLineSegment(sketch, "E670", {"start": v(20.44, -43.74) * mm, "end": v(20.36, -43.3) * mm});
            skLineSegment(sketch, "E671", {"start": v(20.36, -43.3) * mm, "end": v(20.29, -42.86) * mm});
            skLineSegment(sketch, "E672", {"start": v(20.29, -42.86) * mm, "end": v(20.21, -42.42) * mm});
            skLineSegment(sketch, "E673", {"start": v(20.21, -42.42) * mm, "end": v(20.14, -41.98) * mm});
            skLineSegment(sketch, "E674", {"start": v(20.14, -41.98) * mm, "end": v(20.07, -41.54) * mm});
            skLineSegment(sketch, "E675", {"start": v(20.07, -41.54) * mm, "end": v(20, -41.1) * mm});
            skLineSegment(sketch, "E676", {"start": v(20, -41.1) * mm, "end": v(19.92, -40.66) * mm});
            skLineSegment(sketch, "E677", {"start": v(19.92, -40.66) * mm, "end": v(19.84, -40.23) * mm});
            skLineSegment(sketch, "E678", {"start": v(19.84, -40.23) * mm, "end": v(19.77, -39.79) * mm});
            skLineSegment(sketch, "E679", {"start": v(19.77, -39.79) * mm, "end": v(19.7, -39.35) * mm});
            skLineSegment(sketch, "E680", {"start": v(19.7, -39.35) * mm, "end": v(19.62, -38.9) * mm});
            skLineSegment(sketch, "E681", {"start": v(19.62, -38.9) * mm, "end": v(19.55, -38.47) * mm});
            skLineSegment(sketch, "E682", {"start": v(19.55, -38.47) * mm, "end": v(19.47, -38.04) * mm});
            skLineSegment(sketch, "E683", {"start": v(19.47, -38.04) * mm, "end": v(19.85, -37.8) * mm});
            skLineSegment(sketch, "E684", {"start": v(19.85, -37.8) * mm, "end": v(20.23, -37.58) * mm});
            skLineSegment(sketch, "E685", {"start": v(20.23, -37.58) * mm, "end": v(20.62, -37.35) * mm});
            skLineSegment(sketch, "E686", {"start": v(20.62, -37.35) * mm, "end": v(21, -37.11) * mm});
            skLineSegment(sketch, "E687", {"start": v(21, -37.11) * mm, "end": v(21.38, -36.88) * mm});
            skLineSegment(sketch, "E688", {"start": v(21.38, -36.88) * mm, "end": v(21.76, -36.65) * mm});
            skLineSegment(sketch, "E689", {"start": v(21.76, -36.65) * mm, "end": v(22.14, -36.42) * mm});
            skLineSegment(sketch, "E690", {"start": v(22.14, -36.42) * mm, "end": v(22.52, -36.2) * mm});
            skLineSegment(sketch, "E691", {"start": v(22.52, -36.2) * mm, "end": v(22.9, -35.96) * mm});
            skLineSegment(sketch, "E692", {"start": v(22.9, -35.96) * mm, "end": v(23.28, -35.73) * mm});
            skLineSegment(sketch, "E693", {"start": v(23.28, -35.73) * mm, "end": v(23.66, -35.5) * mm});
            skLineSegment(sketch, "E694", {"start": v(23.66, -35.5) * mm, "end": v(24.05, -35.27) * mm});
            skLineSegment(sketch, "E695", {"start": v(24.05, -35.27) * mm, "end": v(24.43, -35.03) * mm});
            skLineSegment(sketch, "E696", {"start": v(24.43, -35.03) * mm, "end": v(24.72, -34.86) * mm});
            skLineSegment(sketch, "E697", {"start": v(24.72, -34.86) * mm, "end": v(24.96, -35.23) * mm});
            skLineSegment(sketch, "E698", {"start": v(24.96, -35.23) * mm, "end": v(25.2, -35.6) * mm});
            skLineSegment(sketch, "E699", {"start": v(25.2, -35.6) * mm, "end": v(25.45, -35.98) * mm});
            skLineSegment(sketch, "E700", {"start": v(25.45, -35.98) * mm, "end": v(25.69, -36.35) * mm});
            skLineSegment(sketch, "E701", {"start": v(25.69, -36.35) * mm, "end": v(25.93, -36.73) * mm});
            skLineSegment(sketch, "E702", {"start": v(25.93, -36.73) * mm, "end": v(26.17, -37.1) * mm});
            skLineSegment(sketch, "E703", {"start": v(26.17, -37.1) * mm, "end": v(26.42, -37.47) * mm});
            skLineSegment(sketch, "E704", {"start": v(26.42, -37.47) * mm, "end": v(26.66, -37.85) * mm});
            skLineSegment(sketch, "E705", {"start": v(26.66, -37.85) * mm, "end": v(26.9, -38.22) * mm});
            skLineSegment(sketch, "E706", {"start": v(26.9, -38.22) * mm, "end": v(27.14, -38.6) * mm});
            skLineSegment(sketch, "E707", {"start": v(27.14, -38.6) * mm, "end": v(27.39, -38.97) * mm});
            skLineSegment(sketch, "E708", {"start": v(27.39, -38.97) * mm, "end": v(27.63, -39.34) * mm});
            skLineSegment(sketch, "E709", {"start": v(27.63, -39.34) * mm, "end": v(27.87, -39.72) * mm});
            skLineSegment(sketch, "E710", {"start": v(27.87, -39.72) * mm, "end": v(28.12, -40.1) * mm});
            skLineSegment(sketch, "E711", {"start": v(28.12, -40.1) * mm, "end": v(28.36, -40.46) * mm});
            skLineSegment(sketch, "E712", {"start": v(28.36, -40.46) * mm, "end": v(28.6, -40.84) * mm});
            skLineSegment(sketch, "E713", {"start": v(28.6, -40.84) * mm, "end": v(28.68, -40.96) * mm});
            skLineSegment(sketch, "E714", {"start": v(28.68, -40.96) * mm, "end": v(29.04, -40.7) * mm});
            skLineSegment(sketch, "E715", {"start": v(29.04, -40.7) * mm, "end": v(29.4, -40.44) * mm});
            skLineSegment(sketch, "E716", {"start": v(29.4, -40.44) * mm, "end": v(29.74, -40.2) * mm});
            skLineSegment(sketch, "E717", {"start": v(29.74, -40.2) * mm, "end": v(29.58, -39.78) * mm});
            skLineSegment(sketch, "E718", {"start": v(29.58, -39.78) * mm, "end": v(29.41, -39.36) * mm});
            skLineSegment(sketch, "E719", {"start": v(29.41, -39.36) * mm, "end": v(29.25, -38.95) * mm});
            skLineSegment(sketch, "E720", {"start": v(29.25, -38.95) * mm, "end": v(29.08, -38.54) * mm});
            skLineSegment(sketch, "E721", {"start": v(29.08, -38.54) * mm, "end": v(28.92, -38.12) * mm});
            skLineSegment(sketch, "E722", {"start": v(28.92, -38.12) * mm, "end": v(28.76, -37.7) * mm});
            skLineSegment(sketch, "E723", {"start": v(28.76, -37.7) * mm, "end": v(28.6, -37.3) * mm});
            skLineSegment(sketch, "E724", {"start": v(28.6, -37.3) * mm, "end": v(28.43, -36.88) * mm});
            skLineSegment(sketch, "E725", {"start": v(28.43, -36.88) * mm, "end": v(28.26, -36.46) * mm});
            skLineSegment(sketch, "E726", {"start": v(28.26, -36.46) * mm, "end": v(28.1, -36.05) * mm});
            skLineSegment(sketch, "E727", {"start": v(28.1, -36.05) * mm, "end": v(27.94, -35.64) * mm});
            skLineSegment(sketch, "E728", {"start": v(27.94, -35.64) * mm, "end": v(27.77, -35.22) * mm});
            skLineSegment(sketch, "E729", {"start": v(27.77, -35.22) * mm, "end": v(27.6, -34.8) * mm});
            skLineSegment(sketch, "E730", {"start": v(27.6, -34.8) * mm, "end": v(27.44, -34.4) * mm});
            skLineSegment(sketch, "E731", {"start": v(27.44, -34.4) * mm, "end": v(27.28, -33.98) * mm});
            skLineSegment(sketch, "E732", {"start": v(27.28, -33.98) * mm, "end": v(27.12, -33.56) * mm});
            skLineSegment(sketch, "E733", {"start": v(27.12, -33.56) * mm, "end": v(26.96, -33.16) * mm});
            skLineSegment(sketch, "E734", {"start": v(26.96, -33.16) * mm, "end": v(27.28, -32.85) * mm});
            skLineSegment(sketch, "E735", {"start": v(27.28, -32.85) * mm, "end": v(27.6, -32.55) * mm});
            skLineSegment(sketch, "E736", {"start": v(27.6, -32.55) * mm, "end": v(27.93, -32.24) * mm});
            skLineSegment(sketch, "E737", {"start": v(27.93, -32.24) * mm, "end": v(28.25, -31.94) * mm});
            skLineSegment(sketch, "E738", {"start": v(28.25, -31.94) * mm, "end": v(28.58, -31.63) * mm});
            skLineSegment(sketch, "E739", {"start": v(28.58, -31.63) * mm, "end": v(28.9, -31.33) * mm});
            skLineSegment(sketch, "E740", {"start": v(28.9, -31.33) * mm, "end": v(29.23, -31.02) * mm});
            skLineSegment(sketch, "E741", {"start": v(29.23, -31.02) * mm, "end": v(29.55, -30.72) * mm});
            skLineSegment(sketch, "E742", {"start": v(29.55, -30.72) * mm, "end": v(29.88, -30.41) * mm});
            skLineSegment(sketch, "E743", {"start": v(29.88, -30.41) * mm, "end": v(30.2, -30.1) * mm});
            skLineSegment(sketch, "E744", {"start": v(30.2, -30.1) * mm, "end": v(30.53, -29.8) * mm});
            skLineSegment(sketch, "E745", {"start": v(30.53, -29.8) * mm, "end": v(30.85, -29.5) * mm});
            skLineSegment(sketch, "E746", {"start": v(30.85, -29.5) * mm, "end": v(31.18, -29.2) * mm});
            skLineSegment(sketch, "E747", {"start": v(31.18, -29.2) * mm, "end": v(31.43, -28.96) * mm});
            skLineSegment(sketch, "E748", {"start": v(31.43, -28.96) * mm, "end": v(31.74, -29.27) * mm});
            skLineSegment(sketch, "E749", {"start": v(31.74, -29.27) * mm, "end": v(32.06, -29.59) * mm});
            skLineSegment(sketch, "E750", {"start": v(32.06, -29.59) * mm, "end": v(32.37, -29.9) * mm});
            skLineSegment(sketch, "E751", {"start": v(32.37, -29.9) * mm, "end": v(32.69, -30.22) * mm});
            skLineSegment(sketch, "E752", {"start": v(32.69, -30.22) * mm, "end": v(33, -30.53) * mm});
            skLineSegment(sketch, "E753", {"start": v(33, -30.53) * mm, "end": v(33.32, -30.85) * mm});
            skLineSegment(sketch, "E754", {"start": v(33.32, -30.85) * mm, "end": v(33.63, -31.16) * mm});
            skLineSegment(sketch, "E755", {"start": v(33.63, -31.16) * mm, "end": v(33.95, -31.48) * mm});
            skLineSegment(sketch, "E756", {"start": v(33.95, -31.48) * mm, "end": v(34.26, -31.8) * mm});
            skLineSegment(sketch, "E757", {"start": v(34.26, -31.8) * mm, "end": v(34.58, -32.1) * mm});
            skLineSegment(sketch, "E758", {"start": v(34.58, -32.1) * mm, "end": v(34.9, -32.42) * mm});
            skLineSegment(sketch, "E759", {"start": v(34.9, -32.42) * mm, "end": v(35.2, -32.74) * mm});
            skLineSegment(sketch, "E760", {"start": v(35.2, -32.74) * mm, "end": v(35.52, -33.05) * mm});
            skLineSegment(sketch, "E761", {"start": v(35.52, -33.05) * mm, "end": v(35.84, -33.37) * mm});
            skLineSegment(sketch, "E762", {"start": v(35.84, -33.37) * mm, "end": v(36.15, -33.68) * mm});
            skLineSegment(sketch, "E763", {"start": v(36.15, -33.68) * mm, "end": v(36.47, -34) * mm});
            skLineSegment(sketch, "E764", {"start": v(36.47, -34) * mm, "end": v(36.57, -34.1) * mm});
            skLineSegment(sketch, "E765", {"start": v(36.57, -34.1) * mm, "end": v(36.87, -33.77) * mm});
            skLineSegment(sketch, "E766", {"start": v(36.87, -33.77) * mm, "end": v(37.17, -33.44) * mm});
            skLineSegment(sketch, "E767", {"start": v(37.17, -33.44) * mm, "end": v(37.45, -33.13) * mm});
            skLineSegment(sketch, "E768", {"start": v(37.45, -33.13) * mm, "end": v(37.2, -32.76) * mm});
            skLineSegment(sketch, "E769", {"start": v(37.2, -32.76) * mm, "end": v(36.95, -32.39) * mm});
            skLineSegment(sketch, "E770", {"start": v(36.95, -32.39) * mm, "end": v(36.7, -32.02) * mm});
            skLineSegment(sketch, "E771", {"start": v(36.7, -32.02) * mm, "end": v(36.46, -31.65) * mm});
            skLineSegment(sketch, "E772", {"start": v(36.46, -31.65) * mm, "end": v(36.21, -31.28) * mm});
            skLineSegment(sketch, "E773", {"start": v(36.21, -31.28) * mm, "end": v(35.97, -30.9) * mm});
            skLineSegment(sketch, "E774", {"start": v(35.97, -30.9) * mm, "end": v(35.72, -30.53) * mm});
            skLineSegment(sketch, "E775", {"start": v(35.72, -30.53) * mm, "end": v(35.47, -30.16) * mm});
            skLineSegment(sketch, "E776", {"start": v(35.47, -30.16) * mm, "end": v(35.23, -29.8) * mm});
            skLineSegment(sketch, "E777", {"start": v(35.23, -29.8) * mm, "end": v(34.98, -29.42) * mm});
            skLineSegment(sketch, "E778", {"start": v(34.98, -29.42) * mm, "end": v(34.74, -29.05) * mm});
            skLineSegment(sketch, "E779", {"start": v(34.74, -29.05) * mm, "end": v(34.49, -28.68) * mm});
            skLineSegment(sketch, "E780", {"start": v(34.49, -28.68) * mm, "end": v(34.24, -28.3) * mm});
            skLineSegment(sketch, "E781", {"start": v(34.24, -28.3) * mm, "end": v(34, -27.93) * mm});
            skLineSegment(sketch, "E782", {"start": v(34, -27.93) * mm, "end": v(33.75, -27.56) * mm});
            skLineSegment(sketch, "E783", {"start": v(33.75, -27.56) * mm, "end": v(33.5, -27.2) * mm});
            skLineSegment(sketch, "E784", {"start": v(33.5, -27.2) * mm, "end": v(33.26, -26.83) * mm});
            skLineSegment(sketch, "E785", {"start": v(33.26, -26.83) * mm, "end": v(33.51, -26.46) * mm});
            skLineSegment(sketch, "E786", {"start": v(33.51, -26.46) * mm, "end": v(33.77, -26.1) * mm});
            skLineSegment(sketch, "E787", {"start": v(33.77, -26.1) * mm, "end": v(34.02, -25.73) * mm});
            skLineSegment(sketch, "E788", {"start": v(34.02, -25.73) * mm, "end": v(34.28, -25.37) * mm});
            skLineSegment(sketch, "E789", {"start": v(34.28, -25.37) * mm, "end": v(34.53, -25) * mm});
            skLineSegment(sketch, "E790", {"start": v(34.53, -25) * mm, "end": v(34.79, -24.63) * mm});
            skLineSegment(sketch, "E791", {"start": v(34.79, -24.63) * mm, "end": v(35.04, -24.27) * mm});
            skLineSegment(sketch, "E792", {"start": v(35.04, -24.27) * mm, "end": v(35.3, -23.9) * mm});
            skLineSegment(sketch, "E793", {"start": v(35.3, -23.9) * mm, "end": v(35.55, -23.53) * mm});
            skLineSegment(sketch, "E794", {"start": v(35.55, -23.53) * mm, "end": v(35.8, -23.17) * mm});
            skLineSegment(sketch, "E795", {"start": v(35.8, -23.17) * mm, "end": v(36.06, -22.8) * mm});
            skLineSegment(sketch, "E796", {"start": v(36.06, -22.8) * mm, "end": v(36.31, -22.44) * mm});
            skLineSegment(sketch, "E797", {"start": v(36.31, -22.44) * mm, "end": v(36.56, -22.07) * mm});
            skLineSegment(sketch, "E798", {"start": v(36.56, -22.07) * mm, "end": v(36.76, -21.8) * mm});
            skLineSegment(sketch, "E799", {"start": v(36.76, -21.8) * mm, "end": v(37.13, -22.03) * mm});
            skLineSegment(sketch, "E800", {"start": v(37.13, -22.03) * mm, "end": v(37.5, -22.28) * mm});
            skLineSegment(sketch, "E801", {"start": v(37.5, -22.28) * mm, "end": v(37.88, -22.52) * mm});
            skLineSegment(sketch, "E802", {"start": v(37.88, -22.52) * mm, "end": v(38.25, -22.76) * mm});
            skLineSegment(sketch, "E803", {"start": v(38.25, -22.76) * mm, "end": v(38.63, -23) * mm});
            skLineSegment(sketch, "E804", {"start": v(38.63, -23) * mm, "end": v(39, -23.25) * mm});
            skLineSegment(sketch, "E805", {"start": v(39, -23.25) * mm, "end": v(39.38, -23.49) * mm});
            skLineSegment(sketch, "E806", {"start": v(39.38, -23.49) * mm, "end": v(39.75, -23.73) * mm});
            skLineSegment(sketch, "E807", {"start": v(39.75, -23.73) * mm, "end": v(40.12, -23.98) * mm});
            skLineSegment(sketch, "E808", {"start": v(40.12, -23.98) * mm, "end": v(40.5, -24.22) * mm});
            skLineSegment(sketch, "E809", {"start": v(40.5, -24.22) * mm, "end": v(40.87, -24.46) * mm});
            skLineSegment(sketch, "E810", {"start": v(40.87, -24.46) * mm, "end": v(41.24, -24.7) * mm});
            skLineSegment(sketch, "E811", {"start": v(41.24, -24.7) * mm, "end": v(41.62, -24.95) * mm});
            skLineSegment(sketch, "E812", {"start": v(41.62, -24.95) * mm, "end": v(42, -25.19) * mm});
            skLineSegment(sketch, "E813", {"start": v(42, -25.19) * mm, "end": v(42.37, -25.43) * mm});
            skLineSegment(sketch, "E814", {"start": v(42.37, -25.43) * mm, "end": v(42.74, -25.67) * mm});
            skLineSegment(sketch, "E815", {"start": v(42.74, -25.67) * mm, "end": v(42.86, -25.75) * mm});
            skLineSegment(sketch, "E816", {"start": v(42.86, -25.75) * mm, "end": v(43.08, -25.37) * mm});
            skLineSegment(sketch, "E817", {"start": v(43.08, -25.37) * mm, "end": v(43.3, -24.98) * mm});
            skLineSegment(sketch, "E818", {"start": v(43.3, -24.98) * mm, "end": v(43.52, -24.62) * mm});
            skLineSegment(sketch, "E819", {"start": v(43.52, -24.62) * mm, "end": v(43.2, -24.3) * mm});
            skLineSegment(sketch, "E820", {"start": v(43.2, -24.3) * mm, "end": v(42.88, -24) * mm});
            skLineSegment(sketch, "E821", {"start": v(42.88, -24) * mm, "end": v(42.56, -23.69) * mm});
            skLineSegment(sketch, "E822", {"start": v(42.56, -23.69) * mm, "end": v(42.24, -23.37) * mm});
            skLineSegment(sketch, "E823", {"start": v(42.24, -23.37) * mm, "end": v(41.93, -23.06) * mm});
            skLineSegment(sketch, "E824", {"start": v(41.93, -23.06) * mm, "end": v(41.6, -22.75) * mm});
            skLineSegment(sketch, "E825", {"start": v(41.6, -22.75) * mm, "end": v(41.29, -22.44) * mm});
            skLineSegment(sketch, "E826", {"start": v(41.29, -22.44) * mm, "end": v(40.97, -22.13) * mm});
            skLineSegment(sketch, "E827", {"start": v(40.97, -22.13) * mm, "end": v(40.65, -21.82) * mm});
            skLineSegment(sketch, "E828", {"start": v(40.65, -21.82) * mm, "end": v(40.33, -21.5) * mm});
            skLineSegment(sketch, "E829", {"start": v(40.33, -21.5) * mm, "end": v(40.02, -21.2) * mm});
            skLineSegment(sketch, "E830", {"start": v(40.02, -21.2) * mm, "end": v(39.7, -20.88) * mm});
            skLineSegment(sketch, "E831", {"start": v(39.7, -20.88) * mm, "end": v(39.38, -20.57) * mm});
            skLineSegment(sketch, "E832", {"start": v(39.38, -20.57) * mm, "end": v(39.06, -20.26) * mm});
            skLineSegment(sketch, "E833", {"start": v(39.06, -20.26) * mm, "end": v(38.74, -19.94) * mm});
            skLineSegment(sketch, "E834", {"start": v(38.74, -19.94) * mm, "end": v(38.42, -19.63) * mm});
            skLineSegment(sketch, "E835", {"start": v(38.42, -19.63) * mm, "end": v(38.11, -19.33) * mm});
            skLineSegment(sketch, "E836", {"start": v(38.11, -19.33) * mm, "end": v(38.28, -18.92) * mm});
            skLineSegment(sketch, "E837", {"start": v(38.28, -18.92) * mm, "end": v(38.46, -18.5) * mm});
            skLineSegment(sketch, "E838", {"start": v(38.46, -18.5) * mm, "end": v(38.63, -18.1) * mm});
            skLineSegment(sketch, "E839", {"start": v(38.63, -18.1) * mm, "end": v(38.8, -17.68) * mm});
            skLineSegment(sketch, "E840", {"start": v(38.8, -17.68) * mm, "end": v(38.97, -17.27) * mm});
            skLineSegment(sketch, "E841", {"start": v(38.97, -17.27) * mm, "end": v(39.15, -16.86) * mm});
            skLineSegment(sketch, "E842", {"start": v(39.15, -16.86) * mm, "end": v(39.32, -16.45) * mm});
            skLineSegment(sketch, "E843", {"start": v(39.32, -16.45) * mm, "end": v(39.5, -16.04) * mm});
            skLineSegment(sketch, "E844", {"start": v(39.5, -16.04) * mm, "end": v(39.66, -15.63) * mm});
            skLineSegment(sketch, "E845", {"start": v(39.66, -15.63) * mm, "end": v(39.84, -15.22) * mm});
            skLineSegment(sketch, "E846", {"start": v(39.84, -15.22) * mm, "end": v(40, -14.8) * mm});
            skLineSegment(sketch, "E847", {"start": v(40, -14.8) * mm, "end": v(40.18, -14.4) * mm});
            skLineSegment(sketch, "E848", {"start": v(40.18, -14.4) * mm, "end": v(40.35, -13.99) * mm});
            skLineSegment(sketch, "E849", {"start": v(40.35, -13.99) * mm, "end": v(40.49, -13.67) * mm});
            skLineSegment(sketch, "E850", {"start": v(40.49, -13.67) * mm, "end": v(40.9, -13.83) * mm});
            skLineSegment(sketch, "E851", {"start": v(40.9, -13.83) * mm, "end": v(41.32, -14) * mm});
            skLineSegment(sketch, "E852", {"start": v(41.32, -14) * mm, "end": v(41.73, -14.15) * mm});
            skLineSegment(sketch, "E853", {"start": v(41.73, -14.15) * mm, "end": v(42.15, -14.31) * mm});
            skLineSegment(sketch, "E854", {"start": v(42.15, -14.31) * mm, "end": v(42.57, -14.47) * mm});
            skLineSegment(sketch, "E855", {"start": v(42.57, -14.47) * mm, "end": v(42.98, -14.63) * mm});
            skLineSegment(sketch, "E856", {"start": v(42.98, -14.63) * mm, "end": v(43.4, -14.8) * mm});
            skLineSegment(sketch, "E857", {"start": v(43.4, -14.8) * mm, "end": v(43.81, -14.95) * mm});
            skLineSegment(sketch, "E858", {"start": v(43.81, -14.95) * mm, "end": v(44.23, -15.1) * mm});
            skLineSegment(sketch, "E859", {"start": v(44.23, -15.1) * mm, "end": v(44.65, -15.27) * mm});
            skLineSegment(sketch, "E860", {"start": v(44.65, -15.27) * mm, "end": v(45.06, -15.43) * mm});
            skLineSegment(sketch, "E861", {"start": v(45.06, -15.43) * mm, "end": v(45.48, -15.59) * mm});
            skLineSegment(sketch, "E862", {"start": v(45.48, -15.59) * mm, "end": v(45.9, -15.75) * mm});
            skLineSegment(sketch, "E863", {"start": v(45.9, -15.75) * mm, "end": v(46.31, -15.9) * mm});
            skLineSegment(sketch, "E864", {"start": v(46.31, -15.9) * mm, "end": v(46.73, -16.07) * mm});
            skLineSegment(sketch, "E865", {"start": v(46.73, -16.07) * mm, "end": v(47.14, -16.23) * mm});
            skLineSegment(sketch, "E866", {"start": v(47.14, -16.23) * mm, "end": v(47.28, -16.28) * mm});
            skLineSegment(sketch, "E867", {"start": v(47.28, -16.28) * mm, "end": v(47.42, -15.86) * mm});
            skLineSegment(sketch, "E868", {"start": v(47.42, -15.86) * mm, "end": v(47.56, -15.43) * mm});
            skLineSegment(sketch, "E869", {"start": v(47.56, -15.43) * mm, "end": v(47.69, -15.04) * mm});
            skLineSegment(sketch, "E870", {"start": v(47.69, -15.04) * mm, "end": v(47.3, -14.8) * mm});
            skLineSegment(sketch, "E871", {"start": v(47.3, -14.8) * mm, "end": v(46.93, -14.56) * mm});
            skLineSegment(sketch, "E872", {"start": v(46.93, -14.56) * mm, "end": v(46.56, -14.32) * mm});
            skLineSegment(sketch, "E873", {"start": v(46.56, -14.32) * mm, "end": v(46.18, -14.08) * mm});
            skLineSegment(sketch, "E874", {"start": v(46.18, -14.08) * mm, "end": v(45.8, -13.84) * mm});
            skLineSegment(sketch, "E875", {"start": v(45.8, -13.84) * mm, "end": v(45.43, -13.6) * mm});
            skLineSegment(sketch, "E876", {"start": v(45.43, -13.6) * mm, "end": v(45.05, -13.36) * mm});
            skLineSegment(sketch, "E877", {"start": v(45.05, -13.36) * mm, "end": v(44.68, -13.13) * mm});
            skLineSegment(sketch, "E878", {"start": v(44.68, -13.13) * mm, "end": v(44.3, -12.89) * mm});
            skLineSegment(sketch, "E879", {"start": v(44.3, -12.89) * mm, "end": v(43.92, -12.65) * mm});
            skLineSegment(sketch, "E880", {"start": v(43.92, -12.65) * mm, "end": v(43.55, -12.4) * mm});
            skLineSegment(sketch, "E881", {"start": v(43.55, -12.4) * mm, "end": v(43.17, -12.17) * mm});
            skLineSegment(sketch, "E882", {"start": v(43.17, -12.17) * mm, "end": v(42.8, -11.93) * mm});
            skLineSegment(sketch, "E883", {"start": v(42.8, -11.93) * mm, "end": v(42.42, -11.7) * mm});
            skLineSegment(sketch, "E884", {"start": v(42.42, -11.7) * mm, "end": v(42.04, -11.45) * mm});
            skLineSegment(sketch, "E885", {"start": v(42.04, -11.45) * mm, "end": v(41.67, -11.22) * mm});
            skLineSegment(sketch, "E886", {"start": v(41.67, -11.22) * mm, "end": v(41.3, -10.98) * mm});
            skLineSegment(sketch, "E887", {"start": v(41.3, -10.98) * mm, "end": v(41.38, -10.54) * mm});
            skLineSegment(sketch, "E888", {"start": v(41.38, -10.54) * mm, "end": v(41.46, -10.1) * mm});
            skLineSegment(sketch, "E889", {"start": v(41.46, -10.1) * mm, "end": v(41.55, -9.67) * mm});
            skLineSegment(sketch, "E890", {"start": v(41.55, -9.67) * mm, "end": v(41.63, -9.23) * mm});
            skLineSegment(sketch, "E891", {"start": v(41.63, -9.23) * mm, "end": v(41.71, -8.8) * mm});
            skLineSegment(sketch, "E892", {"start": v(41.71, -8.8) * mm, "end": v(41.8, -8.35) * mm});
            skLineSegment(sketch, "E893", {"start": v(41.8, -8.35) * mm, "end": v(41.88, -7.92) * mm});
            skLineSegment(sketch, "E894", {"start": v(41.88, -7.92) * mm, "end": v(41.96, -7.48) * mm});
            skLineSegment(sketch, "E895", {"start": v(41.96, -7.48) * mm, "end": v(42.05, -7.04) * mm});
            skLineSegment(sketch, "E896", {"start": v(42.05, -7.04) * mm, "end": v(42.13, -6.6) * mm});
            skLineSegment(sketch, "E897", {"start": v(42.13, -6.6) * mm, "end": v(42.21, -6.17) * mm});
            skLineSegment(sketch, "E898", {"start": v(42.21, -6.17) * mm, "end": v(42.3, -5.73) * mm});
            skLineSegment(sketch, "E899", {"start": v(42.3, -5.73) * mm, "end": v(42.38, -5.3) * mm});
            skLineSegment(sketch, "E900", {"start": v(42.38, -5.3) * mm, "end": v(42.44, -4.96) * mm});
            skLineSegment(sketch, "E901", {"start": v(42.44, -4.96) * mm, "end": v(42.88, -5.03) * mm});
            skLineSegment(sketch, "E902", {"start": v(42.88, -5.03) * mm, "end": v(43.32, -5.1) * mm});
            skLineSegment(sketch, "E903", {"start": v(43.32, -5.1) * mm, "end": v(43.76, -5.16) * mm});
            skLineSegment(sketch, "E904", {"start": v(43.76, -5.16) * mm, "end": v(44.2, -5.23) * mm});
            skLineSegment(sketch, "E905", {"start": v(44.2, -5.23) * mm, "end": v(44.65, -5.3) * mm});
            skLineSegment(sketch, "E906", {"start": v(44.65, -5.3) * mm, "end": v(45.09, -5.37) * mm});
            skLineSegment(sketch, "E907", {"start": v(45.09, -5.37) * mm, "end": v(45.53, -5.44) * mm});
            skLineSegment(sketch, "E908", {"start": v(45.53, -5.44) * mm, "end": v(45.97, -5.51) * mm});
            skLineSegment(sketch, "E909", {"start": v(45.97, -5.51) * mm, "end": v(46.4, -5.58) * mm});
            skLineSegment(sketch, "E910", {"start": v(46.4, -5.58) * mm, "end": v(46.85, -5.65) * mm});
            skLineSegment(sketch, "E911", {"start": v(46.85, -5.65) * mm, "end": v(47.29, -5.72) * mm});
            skLineSegment(sketch, "E912", {"start": v(47.29, -5.72) * mm, "end": v(47.73, -5.8) * mm});
            skLineSegment(sketch, "E913", {"start": v(47.73, -5.8) * mm, "end": v(48.17, -5.86) * mm});
            skLineSegment(sketch, "E914", {"start": v(48.17, -5.86) * mm, "end": v(48.6, -5.93) * mm});
            skLineSegment(sketch, "E915", {"start": v(48.6, -5.93) * mm, "end": v(49.05, -6) * mm});
            skLineSegment(sketch, "E916", {"start": v(49.05, -6) * mm, "end": v(49.49, -6.07) * mm});
            skLineSegment(sketch, "E917", {"start": v(49.49, -6.07) * mm, "end": v(49.63, -6.1) * mm});
            skLineSegment(sketch, "E918", {"start": v(49.63, -6.1) * mm, "end": v(49.68, -5.65) * mm});
            skLineSegment(sketch, "E919", {"start": v(49.68, -5.65) * mm, "end": v(49.72, -5.2) * mm});
            skLineSegment(sketch, "E920", {"start": v(49.72, -5.2) * mm, "end": v(49.77, -4.8) * mm});
            skLineSegment(sketch, "E921", {"start": v(49.77, -4.8) * mm, "end": v(49.35, -4.64) * mm});
            skLineSegment(sketch, "E922", {"start": v(49.35, -4.64) * mm, "end": v(48.93, -4.48) * mm});
            skLineSegment(sketch, "E923", {"start": v(48.93, -4.48) * mm, "end": v(48.52, -4.33) * mm});
            skLineSegment(sketch, "E924", {"start": v(48.52, -4.33) * mm, "end": v(48.1, -4.17) * mm});
            skLineSegment(sketch, "E925", {"start": v(48.1, -4.17) * mm, "end": v(47.68, -4.02) * mm});
            skLineSegment(sketch, "E926", {"start": v(47.68, -4.02) * mm, "end": v(47.26, -3.86) * mm});
            skLineSegment(sketch, "E927", {"start": v(47.26, -3.86) * mm, "end": v(46.85, -3.7) * mm});
            skLineSegment(sketch, "E928", {"start": v(46.85, -3.7) * mm, "end": v(46.43, -3.55) * mm});
            skLineSegment(sketch, "E929", {"start": v(46.43, -3.55) * mm, "end": v(46.01, -3.4) * mm});
            skLineSegment(sketch, "E930", {"start": v(46.01, -3.4) * mm, "end": v(45.6, -3.24) * mm});
            skLineSegment(sketch, "E931", {"start": v(45.6, -3.24) * mm, "end": v(45.18, -3.08) * mm});
            skLineSegment(sketch, "E932", {"start": v(45.18, -3.08) * mm, "end": v(44.76, -2.93) * mm});
            skLineSegment(sketch, "E933", {"start": v(44.76, -2.93) * mm, "end": v(44.34, -2.77) * mm});
            skLineSegment(sketch, "E934", {"start": v(44.34, -2.77) * mm, "end": v(43.92, -2.62) * mm});
            skLineSegment(sketch, "E935", {"start": v(43.92, -2.62) * mm, "end": v(43.5, -2.46) * mm});
            skLineSegment(sketch, "E936", {"start": v(43.5, -2.46) * mm, "end": v(43.09, -2.3) * mm});
            skLineSegment(sketch, "E937", {"start": v(43.09, -2.3) * mm, "end": v(42.68, -2.16) * mm});
            skLineSegment(sketch, "E938", {"start": v(42.68, -2.16) * mm, "end": v(42.67, -1.7) * mm});
            skLineSegment(sketch, "E939", {"start": v(42.67, -1.7) * mm, "end": v(42.66, -1.26) * mm});
            skLineSegment(sketch, "E940", {"start": v(42.66, -1.26) * mm, "end": v(42.65, -0.82) * mm});
            skLineSegment(sketch, "E941", {"start": v(42.65, -0.82) * mm, "end": v(42.64, -0.37) * mm});
            skLineSegment(sketch, "E942", {"start": v(42.64, -0.37) * mm, "end": v(42.63, 0.07) * mm});
            skLineSegment(sketch, "E943", {"start": v(42.63, 0.07) * mm, "end": v(42.62, 0.52) * mm});
            skLineSegment(sketch, "E944", {"start": v(42.62, 0.52) * mm, "end": v(42.61, 0.96) * mm});
            skLineSegment(sketch, "E945", {"start": v(42.61, 0.96) * mm, "end": v(42.6, 1.4) * mm});
            skLineSegment(sketch, "E946", {"start": v(42.6, 1.4) * mm, "end": v(42.6, 1.85) * mm});
            skLineSegment(sketch, "E947", {"start": v(42.6, 1.85) * mm, "end": v(42.58, 2.3) * mm});
            skLineSegment(sketch, "E948", {"start": v(42.58, 2.3) * mm, "end": v(42.57, 2.75) * mm});
            skLineSegment(sketch, "E949", {"start": v(42.57, 2.75) * mm, "end": v(42.56, 3.2) * mm});
            skLineSegment(sketch, "E950", {"start": v(42.56, 3.2) * mm, "end": v(42.55, 3.64) * mm});
            skLineSegment(sketch, "E951", {"start": v(42.55, 3.64) * mm, "end": v(42.55, 3.98) * mm});
            skLineSegment(sketch, "E952", {"start": v(42.55, 3.98) * mm, "end": v(43, 4) * mm});
            skLineSegment(sketch, "E953", {"start": v(43, 4) * mm, "end": v(43.44, 4.02) * mm});
            skLineSegment(sketch, "E954", {"start": v(43.44, 4.02) * mm, "end": v(43.88, 4.05) * mm});
            skLineSegment(sketch, "E955", {"start": v(43.88, 4.05) * mm, "end": v(44.33, 4.07) * mm});
            skLineSegment(sketch, "E956", {"start": v(44.33, 4.07) * mm, "end": v(44.77, 4.1) * mm});
            skLineSegment(sketch, "E957", {"start": v(44.77, 4.1) * mm, "end": v(45.22, 4.12) * mm});
            skLineSegment(sketch, "E958", {"start": v(45.22, 4.12) * mm, "end": v(45.66, 4.14) * mm});
            skLineSegment(sketch, "E959", {"start": v(45.66, 4.14) * mm, "end": v(46.1, 4.16) * mm});
            skLineSegment(sketch, "E960", {"start": v(46.1, 4.16) * mm, "end": v(46.55, 4.19) * mm});
            skLineSegment(sketch, "E961", {"start": v(46.55, 4.19) * mm, "end": v(47, 4.21) * mm});
            skLineSegment(sketch, "E962", {"start": v(47, 4.21) * mm, "end": v(47.44, 4.23) * mm});
            skLineSegment(sketch, "E963", {"start": v(47.44, 4.23) * mm, "end": v(47.89, 4.26) * mm});
            skLineSegment(sketch, "E964", {"start": v(47.89, 4.26) * mm, "end": v(48.33, 4.28) * mm});
            skLineSegment(sketch, "E965", {"start": v(48.33, 4.28) * mm, "end": v(48.78, 4.3) * mm});
            skLineSegment(sketch, "E966", {"start": v(48.78, 4.3) * mm, "end": v(49.22, 4.33) * mm});
            skLineSegment(sketch, "E967", {"start": v(49.22, 4.33) * mm, "end": v(49.67, 4.35) * mm});
            skLineSegment(sketch, "E968", {"start": v(49.67, 4.35) * mm, "end": v(49.8, 4.36) * mm});
            skLineSegment(sketch, "E969", {"start": v(49.8, 4.36) * mm, "end": v(49.77, 4.8) * mm});
            skLineSegment(sketch, "E970", {"start": v(49.77, 4.8) * mm, "end": v(49.72, 5.24) * mm});
            skLineSegment(sketch, "E971", {"start": v(49.72, 5.24) * mm, "end": v(49.68, 5.66) * mm});
            skLineSegment(sketch, "E972", {"start": v(49.68, 5.66) * mm, "end": v(49.24, 5.73) * mm});
            skLineSegment(sketch, "E973", {"start": v(49.24, 5.73) * mm, "end": v(48.8, 5.8) * mm});
            skLineSegment(sketch, "E974", {"start": v(48.8, 5.8) * mm, "end": v(48.36, 5.86) * mm});
            skLineSegment(sketch, "E975", {"start": v(48.36, 5.86) * mm, "end": v(47.92, 5.92) * mm});
            skLineSegment(sketch, "E976", {"start": v(47.92, 5.92) * mm, "end": v(47.47, 5.99) * mm});
            skLineSegment(sketch, "E977", {"start": v(47.47, 5.99) * mm, "end": v(47.03, 6.05) * mm});
            skLineSegment(sketch, "E978", {"start": v(47.03, 6.05) * mm, "end": v(46.6, 6.12) * mm});
            skLineSegment(sketch, "E979", {"start": v(46.6, 6.12) * mm, "end": v(46.15, 6.18) * mm});
            skLineSegment(sketch, "E980", {"start": v(46.15, 6.18) * mm, "end": v(45.71, 6.25) * mm});
            skLineSegment(sketch, "E981", {"start": v(45.71, 6.25) * mm, "end": v(45.27, 6.31) * mm});
            skLineSegment(sketch, "E982", {"start": v(45.27, 6.31) * mm, "end": v(44.83, 6.38) * mm});
            skLineSegment(sketch, "E983", {"start": v(44.83, 6.38) * mm, "end": v(44.39, 6.44) * mm});
            skLineSegment(sketch, "E984", {"start": v(44.39, 6.44) * mm, "end": v(43.95, 6.5) * mm});
            skLineSegment(sketch, "E985", {"start": v(43.95, 6.5) * mm, "end": v(43.5, 6.57) * mm});
            skLineSegment(sketch, "E986", {"start": v(43.5, 6.57) * mm, "end": v(43.07, 6.64) * mm});
            skLineSegment(sketch, "E987", {"start": v(43.07, 6.64) * mm, "end": v(42.63, 6.7) * mm});
            skLineSegment(sketch, "E988", {"start": v(42.63, 6.7) * mm, "end": v(42.2, 6.77) * mm});
            skLineSegment(sketch, "E989", {"start": v(42.2, 6.77) * mm, "end": v(42.1, 7.2) * mm});
            skLineSegment(sketch, "E990", {"start": v(42.1, 7.2) * mm, "end": v(41.99, 7.63) * mm});
            skLineSegment(sketch, "E991", {"start": v(41.99, 7.63) * mm, "end": v(41.89, 8.07) * mm});
            skLineSegment(sketch, "E992", {"start": v(41.89, 8.07) * mm, "end": v(41.79, 8.5) * mm});
            skLineSegment(sketch, "E993", {"start": v(41.79, 8.5) * mm, "end": v(41.68, 8.93) * mm});
            skLineSegment(sketch, "E994", {"start": v(41.68, 8.93) * mm, "end": v(41.58, 9.37) * mm});
            skLineSegment(sketch, "E995", {"start": v(41.58, 9.37) * mm, "end": v(41.48, 9.8) * mm});
            skLineSegment(sketch, "E996", {"start": v(41.48, 9.8) * mm, "end": v(41.38, 10.24) * mm});
            skLineSegment(sketch, "E997", {"start": v(41.38, 10.24) * mm, "end": v(41.28, 10.67) * mm});
            skLineSegment(sketch, "E998", {"start": v(41.28, 10.67) * mm, "end": v(41.17, 11.1) * mm});
            skLineSegment(sketch, "E999", {"start": v(41.17, 11.1) * mm, "end": v(41.07, 11.54) * mm});
            skLineSegment(sketch, "E1000", {"start": v(41.07, 11.54) * mm, "end": v(40.97, 11.97) * mm});
            skLineSegment(sketch, "E1001", {"start": v(40.97, 11.97) * mm, "end": v(40.87, 12.4) * mm});
            skLineSegment(sketch, "E1002", {"start": v(40.87, 12.4) * mm, "end": v(40.8, 12.74) * mm});
            skLineSegment(sketch, "E1003", {"start": v(40.8, 12.74) * mm, "end": v(41.22, 12.85) * mm});
            skLineSegment(sketch, "E1004", {"start": v(41.22, 12.85) * mm, "end": v(41.65, 12.97) * mm});
            skLineSegment(sketch, "E1005", {"start": v(41.65, 12.97) * mm, "end": v(42.08, 13.08) * mm});
            skLineSegment(sketch, "E1006", {"start": v(42.08, 13.08) * mm, "end": v(42.51, 13.2) * mm});
            skLineSegment(sketch, "E1007", {"start": v(42.51, 13.2) * mm, "end": v(42.94, 13.31) * mm});
            skLineSegment(sketch, "E1008", {"start": v(42.94, 13.31) * mm, "end": v(43.37, 13.43) * mm});
            skLineSegment(sketch, "E1009", {"start": v(43.37, 13.43) * mm, "end": v(43.8, 13.54) * mm});
            skLineSegment(sketch, "E1010", {"start": v(43.8, 13.54) * mm, "end": v(44.23, 13.66) * mm});
            skLineSegment(sketch, "E1011", {"start": v(44.23, 13.66) * mm, "end": v(44.66, 13.77) * mm});
            skLineSegment(sketch, "E1012", {"start": v(44.66, 13.77) * mm, "end": v(45.1, 13.89) * mm});
            skLineSegment(sketch, "E1013", {"start": v(45.1, 13.89) * mm, "end": v(45.53, 14) * mm});
            skLineSegment(sketch, "E1014", {"start": v(45.53, 14) * mm, "end": v(45.96, 14.12) * mm});
            skLineSegment(sketch, "E1015", {"start": v(45.96, 14.12) * mm, "end": v(46.39, 14.24) * mm});
            skLineSegment(sketch, "E1016", {"start": v(46.39, 14.24) * mm, "end": v(46.82, 14.35) * mm});
            skLineSegment(sketch, "E1017", {"start": v(46.82, 14.35) * mm, "end": v(47.25, 14.47) * mm});
            skLineSegment(sketch, "E1018", {"start": v(47.25, 14.47) * mm, "end": v(47.68, 14.58) * mm});
            skLineSegment(sketch, "E1019", {"start": v(47.68, 14.58) * mm, "end": v(47.82, 14.62) * mm});
            skLineSegment(sketch, "E1020", {"start": v(47.82, 14.62) * mm, "end": v(47.68, 15.04) * mm});
            skLineSegment(sketch, "E1021", {"start": v(47.68, 15.04) * mm, "end": v(47.54, 15.47) * mm});
            skLineSegment(sketch, "E1022", {"start": v(47.54, 15.47) * mm, "end": v(47.42, 15.87) * mm});
            skLineSegment(sketch, "E1023", {"start": v(47.42, 15.87) * mm, "end": v(46.97, 15.84) * mm});
            skLineSegment(sketch, "E1024", {"start": v(46.97, 15.84) * mm, "end": v(46.53, 15.8) * mm});
            skLineSegment(sketch, "E1025", {"start": v(46.53, 15.8) * mm, "end": v(46.08, 15.78) * mm});
            skLineSegment(sketch, "E1026", {"start": v(46.08, 15.78) * mm, "end": v(45.64, 15.75) * mm});
            skLineSegment(sketch, "E1027", {"start": v(45.64, 15.75) * mm, "end": v(45.2, 15.73) * mm});
            skLineSegment(sketch, "E1028", {"start": v(45.2, 15.73) * mm, "end": v(44.75, 15.7) * mm});
            skLineSegment(sketch, "E1029", {"start": v(44.75, 15.7) * mm, "end": v(44.3, 15.67) * mm});
            skLineSegment(sketch, "E1030", {"start": v(44.3, 15.67) * mm, "end": v(43.86, 15.64) * mm});
            skLineSegment(sketch, "E1031", {"start": v(43.86, 15.64) * mm, "end": v(43.41, 15.61) * mm});
            skLineSegment(sketch, "E1032", {"start": v(43.41, 15.61) * mm, "end": v(42.97, 15.59) * mm});
            skLineSegment(sketch, "E1033", {"start": v(42.97, 15.59) * mm, "end": v(42.52, 15.56) * mm});
            skLineSegment(sketch, "E1034", {"start": v(42.52, 15.56) * mm, "end": v(42.08, 15.53) * mm});
            skLineSegment(sketch, "E1035", {"start": v(42.08, 15.53) * mm, "end": v(41.63, 15.5) * mm});
            skLineSegment(sketch, "E1036", {"start": v(41.63, 15.5) * mm, "end": v(41.19, 15.47) * mm});
            skLineSegment(sketch, "E1037", {"start": v(41.19, 15.47) * mm, "end": v(40.75, 15.45) * mm});
            skLineSegment(sketch, "E1038", {"start": v(40.75, 15.45) * mm, "end": v(40.3, 15.42) * mm});
            skLineSegment(sketch, "E1039", {"start": v(40.3, 15.42) * mm, "end": v(39.87, 15.39) * mm});
            skLineSegment(sketch, "E1040", {"start": v(39.87, 15.39) * mm, "end": v(39.68, 15.8) * mm});
            skLineSegment(sketch, "E1041", {"start": v(39.68, 15.8) * mm, "end": v(39.49, 16.2) * mm});
            skLineSegment(sketch, "E1042", {"start": v(39.49, 16.2) * mm, "end": v(39.3, 16.6) * mm});
            skLineSegment(sketch, "E1043", {"start": v(39.3, 16.6) * mm, "end": v(39.1, 17) * mm});
            skLineSegment(sketch, "E1044", {"start": v(39.1, 17) * mm, "end": v(38.92, 17.4) * mm});
            skLineSegment(sketch, "E1045", {"start": v(38.92, 17.4) * mm, "end": v(38.73, 17.8) * mm});
            skLineSegment(sketch, "E1046", {"start": v(38.73, 17.8) * mm, "end": v(38.54, 18.21) * mm});
            skLineSegment(sketch, "E1047", {"start": v(38.54, 18.21) * mm, "end": v(38.35, 18.61) * mm});
            skLineSegment(sketch, "E1048", {"start": v(38.35, 18.61) * mm, "end": v(38.16, 19.02) * mm});
            skLineSegment(sketch, "E1049", {"start": v(38.16, 19.02) * mm, "end": v(37.97, 19.42) * mm});
            skLineSegment(sketch, "E1050", {"start": v(37.97, 19.42) * mm, "end": v(37.78, 19.82) * mm});
            skLineSegment(sketch, "E1051", {"start": v(37.78, 19.82) * mm, "end": v(37.59, 20.23) * mm});
            skLineSegment(sketch, "E1052", {"start": v(37.59, 20.23) * mm, "end": v(37.4, 20.63) * mm});
            skLineSegment(sketch, "E1053", {"start": v(37.4, 20.63) * mm, "end": v(37.25, 20.94) * mm});
            skLineSegment(sketch, "E1054", {"start": v(37.25, 20.94) * mm, "end": v(37.65, 21.14) * mm});
            skLineSegment(sketch, "E1055", {"start": v(37.65, 21.14) * mm, "end": v(38.05, 21.34) * mm});
            skLineSegment(sketch, "E1056", {"start": v(38.05, 21.34) * mm, "end": v(38.44, 21.55) * mm});
            skLineSegment(sketch, "E1057", {"start": v(38.44, 21.55) * mm, "end": v(38.84, 21.75) * mm});
            skLineSegment(sketch, "E1058", {"start": v(38.84, 21.75) * mm, "end": v(39.24, 21.95) * mm});
            skLineSegment(sketch, "E1059", {"start": v(39.24, 21.95) * mm, "end": v(39.63, 22.15) * mm});
            skLineSegment(sketch, "E1060", {"start": v(39.63, 22.15) * mm, "end": v(40.03, 22.35) * mm});
            skLineSegment(sketch, "E1061", {"start": v(40.03, 22.35) * mm, "end": v(40.43, 22.56) * mm});
            skLineSegment(sketch, "E1062", {"start": v(40.43, 22.56) * mm, "end": v(40.82, 22.76) * mm});
            skLineSegment(sketch, "E1063", {"start": v(40.82, 22.76) * mm, "end": v(41.22, 22.96) * mm});
            skLineSegment(sketch, "E1064", {"start": v(41.22, 22.96) * mm, "end": v(41.62, 23.16) * mm});
            skLineSegment(sketch, "E1065", {"start": v(41.62, 23.16) * mm, "end": v(42.02, 23.37) * mm});
            skLineSegment(sketch, "E1066", {"start": v(42.02, 23.37) * mm, "end": v(42.41, 23.57) * mm});
            skLineSegment(sketch, "E1067", {"start": v(42.41, 23.57) * mm, "end": v(42.8, 23.77) * mm});
            skLineSegment(sketch, "E1068", {"start": v(42.8, 23.77) * mm, "end": v(43.2, 23.97) * mm});
            skLineSegment(sketch, "E1069", {"start": v(43.2, 23.97) * mm, "end": v(43.6, 24.18) * mm});
            skLineSegment(sketch, "E1070", {"start": v(43.6, 24.18) * mm, "end": v(43.73, 24.24) * mm});
            skLineSegment(sketch, "E1071", {"start": v(43.73, 24.24) * mm, "end": v(43.5, 24.63) * mm});
            skLineSegment(sketch, "E1072", {"start": v(43.5, 24.63) * mm, "end": v(43.29, 25.01) * mm});
            skLineSegment(sketch, "E1073", {"start": v(43.29, 25.01) * mm, "end": v(43.08, 25.38) * mm});
            skLineSegment(sketch, "E1074", {"start": v(43.08, 25.38) * mm, "end": v(42.65, 25.26) * mm});
            skLineSegment(sketch, "E1075", {"start": v(42.65, 25.26) * mm, "end": v(42.22, 25.14) * mm});
            skLineSegment(sketch, "E1076", {"start": v(42.22, 25.14) * mm, "end": v(41.8, 25.02) * mm});
            skLineSegment(sketch, "E1077", {"start": v(41.8, 25.02) * mm, "end": v(41.36, 24.9) * mm});
            skLineSegment(sketch, "E1078", {"start": v(41.36, 24.9) * mm, "end": v(40.94, 24.78) * mm});
            skLineSegment(sketch, "E1079", {"start": v(40.94, 24.78) * mm, "end": v(40.5, 24.66) * mm});
            skLineSegment(sketch, "E1080", {"start": v(40.5, 24.66) * mm, "end": v(40.08, 24.54) * mm});
            skLineSegment(sketch, "E1081", {"start": v(40.08, 24.54) * mm, "end": v(39.65, 24.42) * mm});
            skLineSegment(sketch, "E1082", {"start": v(39.65, 24.42) * mm, "end": v(39.22, 24.3) * mm});
            skLineSegment(sketch, "E1083", {"start": v(39.22, 24.3) * mm, "end": v(38.79, 24.18) * mm});
            skLineSegment(sketch, "E1084", {"start": v(38.79, 24.18) * mm, "end": v(38.36, 24.06) * mm});
            skLineSegment(sketch, "E1085", {"start": v(38.36, 24.06) * mm, "end": v(37.93, 23.94) * mm});
            skLineSegment(sketch, "E1086", {"start": v(37.93, 23.94) * mm, "end": v(37.5, 23.82) * mm});
            skLineSegment(sketch, "E1087", {"start": v(37.5, 23.82) * mm, "end": v(37.07, 23.7) * mm});
            skLineSegment(sketch, "E1088", {"start": v(37.07, 23.7) * mm, "end": v(36.64, 23.58) * mm});
            skLineSegment(sketch, "E1089", {"start": v(36.64, 23.58) * mm, "end": v(36.21, 23.46) * mm});
            skLineSegment(sketch, "E1090", {"start": v(36.21, 23.46) * mm, "end": v(35.8, 23.34) * mm});
            skLineSegment(sketch, "E1091", {"start": v(35.8, 23.34) * mm, "end": v(35.52, 23.7) * mm});
            skLineSegment(sketch, "E1092", {"start": v(35.52, 23.7) * mm, "end": v(35.26, 24.05) * mm});
            skLineSegment(sketch, "E1093", {"start": v(35.26, 24.05) * mm, "end": v(34.99, 24.4) * mm});
            skLineSegment(sketch, "E1094", {"start": v(34.99, 24.4) * mm, "end": v(34.72, 24.76) * mm});
            skLineSegment(sketch, "E1095", {"start": v(34.72, 24.76) * mm, "end": v(34.45, 25.12) * mm});
            skLineSegment(sketch, "E1096", {"start": v(34.45, 25.12) * mm, "end": v(34.18, 25.47) * mm});
            skLineSegment(sketch, "E1097", {"start": v(34.18, 25.47) * mm, "end": v(33.9, 25.83) * mm});
            skLineSegment(sketch, "E1098", {"start": v(33.9, 25.83) * mm, "end": v(33.64, 26.18) * mm});
            skLineSegment(sketch, "E1099", {"start": v(33.64, 26.18) * mm, "end": v(33.37, 26.54) * mm});
            skLineSegment(sketch, "E1100", {"start": v(33.37, 26.54) * mm, "end": v(33.1, 26.9) * mm});
            skLineSegment(sketch, "E1101", {"start": v(33.1, 26.9) * mm, "end": v(32.83, 27.25) * mm});
            skLineSegment(sketch, "E1102", {"start": v(32.83, 27.25) * mm, "end": v(32.56, 27.6) * mm});
            skLineSegment(sketch, "E1103", {"start": v(32.56, 27.6) * mm, "end": v(32.29, 27.95) * mm});
            skLineSegment(sketch, "E1104", {"start": v(32.29, 27.95) * mm, "end": v(32.08, 28.23) * mm});
            skLineSegment(sketch, "E1105", {"start": v(32.08, 28.23) * mm, "end": v(32.43, 28.5) * mm});
            skLineSegment(sketch, "E1106", {"start": v(32.43, 28.5) * mm, "end": v(32.78, 28.79) * mm});
            skLineSegment(sketch, "E1107", {"start": v(32.78, 28.79) * mm, "end": v(33.12, 29.07) * mm});
            skLineSegment(sketch, "E1108", {"start": v(33.12, 29.07) * mm, "end": v(33.47, 29.35) * mm});
            skLineSegment(sketch, "E1109", {"start": v(33.47, 29.35) * mm, "end": v(33.82, 29.63) * mm});
            skLineSegment(sketch, "E1110", {"start": v(33.82, 29.63) * mm, "end": v(34.16, 29.9) * mm});
            skLineSegment(sketch, "E1111", {"start": v(34.16, 29.9) * mm, "end": v(34.5, 30.19) * mm});
            skLineSegment(sketch, "E1112", {"start": v(34.5, 30.19) * mm, "end": v(34.85, 30.47) * mm});
            skLineSegment(sketch, "E1113", {"start": v(34.85, 30.47) * mm, "end": v(35.2, 30.75) * mm});
            skLineSegment(sketch, "E1114", {"start": v(35.2, 30.75) * mm, "end": v(35.55, 31.03) * mm});
            skLineSegment(sketch, "E1115", {"start": v(35.55, 31.03) * mm, "end": v(35.9, 31.31) * mm});
            skLineSegment(sketch, "E1116", {"start": v(35.9, 31.31) * mm, "end": v(36.24, 31.6) * mm});
            skLineSegment(sketch, "E1117", {"start": v(36.24, 31.6) * mm, "end": v(36.59, 31.87) * mm});
            skLineSegment(sketch, "E1118", {"start": v(36.59, 31.87) * mm, "end": v(36.93, 32.15) * mm});
            skLineSegment(sketch, "E1119", {"start": v(36.93, 32.15) * mm, "end": v(37.28, 32.43) * mm});
            skLineSegment(sketch, "E1120", {"start": v(37.28, 32.43) * mm, "end": v(37.62, 32.71) * mm});
            skLineSegment(sketch, "E1121", {"start": v(37.62, 32.71) * mm, "end": v(37.74, 32.8) * mm});
            skLineSegment(sketch, "E1122", {"start": v(37.74, 32.8) * mm, "end": v(37.44, 33.14) * mm});
            skLineSegment(sketch, "E1123", {"start": v(37.44, 33.14) * mm, "end": v(37.14, 33.47) * mm});
            skLineSegment(sketch, "E1124", {"start": v(37.14, 33.47) * mm, "end": v(36.86, 33.78) * mm});
            skLineSegment(sketch, "E1125", {"start": v(36.86, 33.78) * mm, "end": v(36.47, 33.57) * mm});
            skLineSegment(sketch, "E1126", {"start": v(36.47, 33.57) * mm, "end": v(36.07, 33.37) * mm});
            skLineSegment(sketch, "E1127", {"start": v(36.07, 33.37) * mm, "end": v(35.68, 33.16) * mm});
            skLineSegment(sketch, "E1128", {"start": v(35.68, 33.16) * mm, "end": v(35.28, 32.95) * mm});
            skLineSegment(sketch, "E1129", {"start": v(35.28, 32.95) * mm, "end": v(34.89, 32.75) * mm});
            skLineSegment(sketch, "E1130", {"start": v(34.89, 32.75) * mm, "end": v(34.5, 32.54) * mm});
            skLineSegment(sketch, "E1131", {"start": v(34.5, 32.54) * mm, "end": v(34.1, 32.33) * mm});
            skLineSegment(sketch, "E1132", {"start": v(34.1, 32.33) * mm, "end": v(33.7, 32.13) * mm});
            skLineSegment(sketch, "E1133", {"start": v(33.7, 32.13) * mm, "end": v(33.3, 31.92) * mm});
            skLineSegment(sketch, "E1134", {"start": v(33.3, 31.92) * mm, "end": v(32.91, 31.71) * mm});
            skLineSegment(sketch, "E1135", {"start": v(32.91, 31.71) * mm, "end": v(32.52, 31.5) * mm});
            skLineSegment(sketch, "E1136", {"start": v(32.52, 31.5) * mm, "end": v(32.12, 31.3) * mm});
            skLineSegment(sketch, "E1137", {"start": v(32.12, 31.3) * mm, "end": v(31.73, 31.1) * mm});
            skLineSegment(sketch, "E1138", {"start": v(31.73, 31.1) * mm, "end": v(31.34, 30.89) * mm});
            skLineSegment(sketch, "E1139", {"start": v(31.34, 30.89) * mm, "end": v(30.94, 30.68) * mm});
            skLineSegment(sketch, "E1140", {"start": v(30.94, 30.68) * mm, "end": v(30.55, 30.48) * mm});
            skLineSegment(sketch, "E1141", {"start": v(30.55, 30.48) * mm, "end": v(30.16, 30.27) * mm});
            skLineSegment(sketch, "E1142", {"start": v(30.16, 30.27) * mm, "end": v(29.82, 30.57) * mm});
            skLineSegment(sketch, "E1143", {"start": v(29.82, 30.57) * mm, "end": v(29.48, 30.86) * mm});
            skLineSegment(sketch, "E1144", {"start": v(29.48, 30.86) * mm, "end": v(29.15, 31.15) * mm});
            skLineSegment(sketch, "E1145", {"start": v(29.15, 31.15) * mm, "end": v(28.8, 31.44) * mm});
            skLineSegment(sketch, "E1146", {"start": v(28.8, 31.44) * mm, "end": v(28.47, 31.73) * mm});
            skLineSegment(sketch, "E1147", {"start": v(28.47, 31.73) * mm, "end": v(28.13, 32.02) * mm});
            skLineSegment(sketch, "E1148", {"start": v(28.13, 32.02) * mm, "end": v(27.8, 32.31) * mm});
            skLineSegment(sketch, "E1149", {"start": v(27.8, 32.31) * mm, "end": v(27.46, 32.6) * mm});
            skLineSegment(sketch, "E1150", {"start": v(27.46, 32.6) * mm, "end": v(27.12, 32.9) * mm});
            skLineSegment(sketch, "E1151", {"start": v(27.12, 32.9) * mm, "end": v(26.78, 33.18) * mm});
            skLineSegment(sketch, "E1152", {"start": v(26.78, 33.18) * mm, "end": v(26.45, 33.48) * mm});
            skLineSegment(sketch, "E1153", {"start": v(26.45, 33.48) * mm, "end": v(26.1, 33.77) * mm});
            skLineSegment(sketch, "E1154", {"start": v(26.1, 33.77) * mm, "end": v(25.77, 34.06) * mm});
            skLineSegment(sketch, "E1155", {"start": v(25.77, 34.06) * mm, "end": v(25.51, 34.28) * mm});
            skLineSegment(sketch, "E1156", {"start": v(25.51, 34.28) * mm, "end": v(25.8, 34.63) * mm});
            skLineSegment(sketch, "E1157", {"start": v(25.8, 34.63) * mm, "end": v(26.07, 34.97) * mm});
            skLineSegment(sketch, "E1158", {"start": v(26.07, 34.97) * mm, "end": v(26.36, 35.32) * mm});
            skLineSegment(sketch, "E1159", {"start": v(26.36, 35.32) * mm, "end": v(26.64, 35.67) * mm});
            skLineSegment(sketch, "E1160", {"start": v(26.64, 35.67) * mm, "end": v(26.92, 36.01) * mm});
            skLineSegment(sketch, "E1161", {"start": v(26.92, 36.01) * mm, "end": v(27.2, 36.36) * mm});
            skLineSegment(sketch, "E1162", {"start": v(27.2, 36.36) * mm, "end": v(27.48, 36.7) * mm});
            skLineSegment(sketch, "E1163", {"start": v(27.48, 36.7) * mm, "end": v(27.76, 37.05) * mm});
            skLineSegment(sketch, "E1164", {"start": v(27.76, 37.05) * mm, "end": v(28.04, 37.4) * mm});
            skLineSegment(sketch, "E1165", {"start": v(28.04, 37.4) * mm, "end": v(28.32, 37.74) * mm});
            skLineSegment(sketch, "E1166", {"start": v(28.32, 37.74) * mm, "end": v(28.6, 38.09) * mm});
            skLineSegment(sketch, "E1167", {"start": v(28.6, 38.09) * mm, "end": v(28.88, 38.44) * mm});
            skLineSegment(sketch, "E1168", {"start": v(28.88, 38.44) * mm, "end": v(29.16, 38.78) * mm});
            skLineSegment(sketch, "E1169", {"start": v(29.16, 38.78) * mm, "end": v(29.44, 39.13) * mm});
            skLineSegment(sketch, "E1170", {"start": v(29.44, 39.13) * mm, "end": v(29.72, 39.47) * mm});
            skLineSegment(sketch, "E1171", {"start": v(29.72, 39.47) * mm, "end": v(30, 39.82) * mm});
            skLineSegment(sketch, "E1172", {"start": v(30, 39.82) * mm, "end": v(30.1, 39.93) * mm});
            skLineSegment(sketch, "E1173", {"start": v(30.1, 39.93) * mm, "end": v(29.73, 40.2) * mm});
            skLineSegment(sketch, "E1174", {"start": v(29.73, 40.2) * mm, "end": v(29.37, 40.46) * mm});
            skLineSegment(sketch, "E1175", {"start": v(29.37, 40.46) * mm, "end": v(29.04, 40.7) * mm});
            skLineSegment(sketch, "E1176", {"start": v(29.04, 40.7) * mm, "end": v(28.7, 40.42) * mm});
            skLineSegment(sketch, "E1177", {"start": v(28.7, 40.42) * mm, "end": v(28.35, 40.14) * mm});
            skLineSegment(sketch, "E1178", {"start": v(28.35, 40.14) * mm, "end": v(28, 39.85) * mm});
            skLineSegment(sketch, "E1179", {"start": v(28, 39.85) * mm, "end": v(27.66, 39.57) * mm});
            skLineSegment(sketch, "E1180", {"start": v(27.66, 39.57) * mm, "end": v(27.32, 39.29) * mm});
            skLineSegment(sketch, "E1181", {"start": v(27.32, 39.29) * mm, "end": v(26.98, 39) * mm});
            skLineSegment(sketch, "E1182", {"start": v(26.98, 39) * mm, "end": v(26.63, 38.72) * mm});
            skLineSegment(sketch, "E1183", {"start": v(26.63, 38.72) * mm, "end": v(26.29, 38.43) * mm});
            skLineSegment(sketch, "E1184", {"start": v(26.29, 38.43) * mm, "end": v(25.94, 38.15) * mm});
            skLineSegment(sketch, "E1185", {"start": v(25.94, 38.15) * mm, "end": v(25.6, 37.87) * mm});
            skLineSegment(sketch, "E1186", {"start": v(25.6, 37.87) * mm, "end": v(25.26, 37.58) * mm});
            skLineSegment(sketch, "E1187", {"start": v(25.26, 37.58) * mm, "end": v(24.91, 37.3) * mm});
            skLineSegment(sketch, "E1188", {"start": v(24.91, 37.3) * mm, "end": v(24.57, 37.01) * mm});
            skLineSegment(sketch, "E1189", {"start": v(24.57, 37.01) * mm, "end": v(24.23, 36.73) * mm});
            skLineSegment(sketch, "E1190", {"start": v(24.23, 36.73) * mm, "end": v(23.88, 36.44) * mm});
            skLineSegment(sketch, "E1191", {"start": v(23.88, 36.44) * mm, "end": v(23.54, 36.16) * mm});
            skLineSegment(sketch, "E1192", {"start": v(23.54, 36.16) * mm, "end": v(23.2, 35.88) * mm});
            skLineSegment(sketch, "E1193", {"start": v(23.2, 35.88) * mm, "end": v(22.82, 36.1) * mm});
            skLineSegment(sketch, "E1194", {"start": v(22.82, 36.1) * mm, "end": v(22.42, 36.31) * mm});
            skLineSegment(sketch, "E1195", {"start": v(22.42, 36.31) * mm, "end": v(22.03, 36.53) * mm});
            skLineSegment(sketch, "E1196", {"start": v(22.03, 36.53) * mm, "end": v(21.64, 36.74) * mm});
            skLineSegment(sketch, "E1197", {"start": v(21.64, 36.74) * mm, "end": v(21.25, 36.96) * mm});
            skLineSegment(sketch, "E1198", {"start": v(21.25, 36.96) * mm, "end": v(20.86, 37.17) * mm});
            skLineSegment(sketch, "E1199", {"start": v(20.86, 37.17) * mm, "end": v(20.47, 37.38) * mm});
            skLineSegment(sketch, "E1200", {"start": v(20.47, 37.38) * mm, "end": v(20.08, 37.6) * mm});
            skLineSegment(sketch, "E1201", {"start": v(20.08, 37.6) * mm, "end": v(19.7, 37.81) * mm});
            skLineSegment(sketch, "E1202", {"start": v(19.7, 37.81) * mm, "end": v(19.3, 38.03) * mm});
            skLineSegment(sketch, "E1203", {"start": v(19.3, 38.03) * mm, "end": v(18.9, 38.24) * mm});
            skLineSegment(sketch, "E1204", {"start": v(18.9, 38.24) * mm, "end": v(18.52, 38.46) * mm});
            skLineSegment(sketch, "E1205", {"start": v(18.52, 38.46) * mm, "end": v(18.13, 38.67) * mm});
            skLineSegment(sketch, "E1206", {"start": v(18.13, 38.67) * mm, "end": v(17.83, 38.84) * mm});
            skLineSegment(sketch, "E1207", {"start": v(17.83, 38.84) * mm, "end": v(18.03, 39.23) * mm});
            skLineSegment(sketch, "E1208", {"start": v(18.03, 39.23) * mm, "end": v(18.23, 39.63) * mm});
            skLineSegment(sketch, "E1209", {"start": v(18.23, 39.63) * mm, "end": v(18.44, 40.03) * mm});
            skLineSegment(sketch, "E1210", {"start": v(18.44, 40.03) * mm, "end": v(18.64, 40.42) * mm});
            skLineSegment(sketch, "E1211", {"start": v(18.64, 40.42) * mm, "end": v(18.84, 40.82) * mm});
            skLineSegment(sketch, "E1212", {"start": v(18.84, 40.82) * mm, "end": v(19.04, 41.22) * mm});
            skLineSegment(sketch, "E1213", {"start": v(19.04, 41.22) * mm, "end": v(19.25, 41.61) * mm});
            skLineSegment(sketch, "E1214", {"start": v(19.25, 41.61) * mm, "end": v(19.45, 42.01) * mm});
            skLineSegment(sketch, "E1215", {"start": v(19.45, 42.01) * mm, "end": v(19.65, 42.4) * mm});
            skLineSegment(sketch, "E1216", {"start": v(19.65, 42.4) * mm, "end": v(19.85, 42.8) * mm});
            skLineSegment(sketch, "E1217", {"start": v(19.85, 42.8) * mm, "end": v(20.05, 43.2) * mm});
            skLineSegment(sketch, "E1218", {"start": v(20.05, 43.2) * mm, "end": v(20.26, 43.6) * mm});
            skLineSegment(sketch, "E1219", {"start": v(20.26, 43.6) * mm, "end": v(20.46, 44) * mm});
            skLineSegment(sketch, "E1220", {"start": v(20.46, 44) * mm, "end": v(20.66, 44.4) * mm});
            skLineSegment(sketch, "E1221", {"start": v(20.66, 44.4) * mm, "end": v(20.86, 44.8) * mm});
            skLineSegment(sketch, "E1222", {"start": v(20.86, 44.8) * mm, "end": v(21.07, 45.19) * mm});
            skLineSegment(sketch, "E1223", {"start": v(21.07, 45.19) * mm, "end": v(21.13, 45.32) * mm});
            skLineSegment(sketch, "E1224", {"start": v(21.13, 45.32) * mm, "end": v(20.72, 45.5) * mm});
            skLineSegment(sketch, "E1225", {"start": v(20.72, 45.5) * mm, "end": v(20.32, 45.68) * mm});
            skLineSegment(sketch, "E1226", {"start": v(20.32, 45.68) * mm, "end": v(19.94, 45.85) * mm});
            skLineSegment(sketch, "E1227", {"start": v(19.94, 45.85) * mm, "end": v(19.66, 45.5) * mm});
            skLineSegment(sketch, "E1228", {"start": v(19.66, 45.5) * mm, "end": v(19.38, 45.15) * mm});
            skLineSegment(sketch, "E1229", {"start": v(19.38, 45.15) * mm, "end": v(19.1, 44.8) * mm});
            skLineSegment(sketch, "E1230", {"start": v(19.1, 44.8) * mm, "end": v(18.83, 44.46) * mm});
            skLineSegment(sketch, "E1231", {"start": v(18.83, 44.46) * mm, "end": v(18.55, 44.1) * mm});
            skLineSegment(sketch, "E1232", {"start": v(18.55, 44.1) * mm, "end": v(18.28, 43.76) * mm});
            skLineSegment(sketch, "E1233", {"start": v(18.28, 43.76) * mm, "end": v(18, 43.4) * mm});
            skLineSegment(sketch, "E1234", {"start": v(18, 43.4) * mm, "end": v(17.72, 43.06) * mm});
            skLineSegment(sketch, "E1235", {"start": v(17.72, 43.06) * mm, "end": v(17.45, 42.7) * mm});
            skLineSegment(sketch, "E1236", {"start": v(17.45, 42.7) * mm, "end": v(17.17, 42.36) * mm});
            skLineSegment(sketch, "E1237", {"start": v(17.17, 42.36) * mm, "end": v(16.9, 42.01) * mm});
            skLineSegment(sketch, "E1238", {"start": v(16.9, 42.01) * mm, "end": v(16.62, 41.66) * mm});
            skLineSegment(sketch, "E1239", {"start": v(16.62, 41.66) * mm, "end": v(16.34, 41.31) * mm});
            skLineSegment(sketch, "E1240", {"start": v(16.34, 41.31) * mm, "end": v(16.06, 40.96) * mm});
            skLineSegment(sketch, "E1241", {"start": v(16.06, 40.96) * mm, "end": v(15.79, 40.61) * mm});
            skLineSegment(sketch, "E1242", {"start": v(15.79, 40.61) * mm, "end": v(15.5, 40.27) * mm});
            skLineSegment(sketch, "E1243", {"start": v(15.5, 40.27) * mm, "end": v(15.24, 39.92) * mm});
            skLineSegment(sketch, "E1244", {"start": v(15.24, 39.92) * mm, "end": v(14.81, 40.05) * mm});
            skLineSegment(sketch, "E1245", {"start": v(14.81, 40.05) * mm, "end": v(14.38, 40.18) * mm});
            skLineSegment(sketch, "E1246", {"start": v(14.38, 40.18) * mm, "end": v(13.96, 40.3) * mm});
            skLineSegment(sketch, "E1247", {"start": v(13.96, 40.3) * mm, "end": v(13.53, 40.44) * mm});
            skLineSegment(sketch, "E1248", {"start": v(13.53, 40.44) * mm, "end": v(13.1, 40.57) * mm});
            skLineSegment(sketch, "E1249", {"start": v(13.1, 40.57) * mm, "end": v(12.68, 40.7) * mm});
            skLineSegment(sketch, "E1250", {"start": v(12.68, 40.7) * mm, "end": v(12.25, 40.82) * mm});
            skLineSegment(sketch, "E1251", {"start": v(12.25, 40.82) * mm, "end": v(11.82, 40.95) * mm});
            skLineSegment(sketch, "E1252", {"start": v(11.82, 40.95) * mm, "end": v(11.4, 41.08) * mm});
            skLineSegment(sketch, "E1253", {"start": v(11.4, 41.08) * mm, "end": v(10.97, 41.2) * mm});
            skLineSegment(sketch, "E1254", {"start": v(10.97, 41.2) * mm, "end": v(10.54, 41.34) * mm});
            skLineSegment(sketch, "E1255", {"start": v(10.54, 41.34) * mm, "end": v(10.12, 41.47) * mm});
            skLineSegment(sketch, "E1256", {"start": v(10.12, 41.47) * mm, "end": v(9.7, 41.6) * mm});
            skLineSegment(sketch, "E1257", {"start": v(9.7, 41.6) * mm, "end": v(9.37, 41.7) * mm});
            skLineSegment(sketch, "E1258", {"start": v(9.37, 41.7) * mm, "end": v(9.48, 42.12) * mm});
            skLineSegment(sketch, "E1259", {"start": v(9.48, 42.12) * mm, "end": v(9.6, 42.55) * mm});
            skLineSegment(sketch, "E1260", {"start": v(9.6, 42.55) * mm, "end": v(9.71, 42.99) * mm});
            skLineSegment(sketch, "E1261", {"start": v(9.71, 42.99) * mm, "end": v(9.83, 43.42) * mm});
            skLineSegment(sketch, "E1262", {"start": v(9.83, 43.42) * mm, "end": v(9.94, 43.85) * mm});
            skLineSegment(sketch, "E1263", {"start": v(9.94, 43.85) * mm, "end": v(10.06, 44.28) * mm});
            skLineSegment(sketch, "E1264", {"start": v(10.06, 44.28) * mm, "end": v(10.17, 44.7) * mm});
            skLineSegment(sketch, "E1265", {"start": v(10.17, 44.7) * mm, "end": v(10.29, 45.14) * mm});
            skLineSegment(sketch, "E1266", {"start": v(10.29, 45.14) * mm, "end": v(10.4, 45.57) * mm});
            skLineSegment(sketch, "E1267", {"start": v(10.4, 45.57) * mm, "end": v(10.52, 46) * mm});
            skLineSegment(sketch, "E1268", {"start": v(10.52, 46) * mm, "end": v(10.63, 46.43) * mm});
            skLineSegment(sketch, "E1269", {"start": v(10.63, 46.43) * mm, "end": v(10.75, 46.86) * mm});
            skLineSegment(sketch, "E1270", {"start": v(10.75, 46.86) * mm, "end": v(10.86, 47.29) * mm});
            skLineSegment(sketch, "E1271", {"start": v(10.86, 47.29) * mm, "end": v(10.98, 47.72) * mm});
            skLineSegment(sketch, "E1272", {"start": v(10.98, 47.72) * mm, "end": v(11.1, 48.15) * mm});
            skLineSegment(sketch, "E1273", {"start": v(11.1, 48.15) * mm, "end": v(11.21, 48.58) * mm});
            skLineSegment(sketch, "E1274", {"start": v(11.21, 48.58) * mm, "end": v(11.25, 48.72) * mm});
            skLineSegment(sketch, "E1275", {"start": v(11.25, 48.72) * mm, "end": v(10.81, 48.81) * mm});
            skLineSegment(sketch, "E1276", {"start": v(10.81, 48.81) * mm, "end": v(10.38, 48.9) * mm});
            skLineSegment(sketch, "E1277", {"start": v(10.38, 48.9) * mm, "end": v(9.97, 49) * mm});
            skLineSegment(sketch, "E1278", {"start": v(9.97, 49) * mm, "end": v(9.77, 48.6) * mm});
            skLineSegment(sketch, "E1279", {"start": v(9.77, 48.6) * mm, "end": v(9.57, 48.2) * mm});
            skLineSegment(sketch, "E1280", {"start": v(9.57, 48.2) * mm, "end": v(9.37, 47.8) * mm});
            skLineSegment(sketch, "E1281", {"start": v(9.37, 47.8) * mm, "end": v(9.18, 47.4) * mm});
            skLineSegment(sketch, "E1282", {"start": v(9.18, 47.4) * mm, "end": v(8.98, 47) * mm});
            skLineSegment(sketch, "E1283", {"start": v(8.98, 47) * mm, "end": v(8.78, 46.6) * mm});
            skLineSegment(sketch, "E1284", {"start": v(8.78, 46.6) * mm, "end": v(8.58, 46.2) * mm});
            skLineSegment(sketch, "E1285", {"start": v(8.58, 46.2) * mm, "end": v(8.38, 45.8) * mm});
            skLineSegment(sketch, "E1286", {"start": v(8.38, 45.8) * mm, "end": v(8.19, 45.4) * mm});
            skLineSegment(sketch, "E1287", {"start": v(8.19, 45.4) * mm, "end": v(7.99, 45) * mm});
            skLineSegment(sketch, "E1288", {"start": v(7.99, 45) * mm, "end": v(7.79, 44.6) * mm});
            skLineSegment(sketch, "E1289", {"start": v(7.79, 44.6) * mm, "end": v(7.6, 44.2) * mm});
            skLineSegment(sketch, "E1290", {"start": v(7.6, 44.2) * mm, "end": v(7.4, 43.8) * mm});
            skLineSegment(sketch, "E1291", {"start": v(7.4, 43.8) * mm, "end": v(7.2, 43.4) * mm});
            skLineSegment(sketch, "E1292", {"start": v(7.2, 43.4) * mm, "end": v(7, 43) * mm});
            skLineSegment(sketch, "E1293", {"start": v(7, 43) * mm, "end": v(6.8, 42.6) * mm});
            skLineSegment(sketch, "E1294", {"start": v(6.8, 42.6) * mm, "end": v(6.6, 42.22) * mm});
            skLineSegment(sketch, "E1295", {"start": v(6.6, 42.22) * mm, "end": v(6.16, 42.26) * mm});
            skLineSegment(sketch, "E1296", {"start": v(6.16, 42.26) * mm, "end": v(5.72, 42.3) * mm});
            skLineSegment(sketch, "E1297", {"start": v(5.72, 42.3) * mm, "end": v(5.27, 42.33) * mm});
            skLineSegment(sketch, "E1298", {"start": v(5.27, 42.33) * mm, "end": v(4.83, 42.37) * mm});
            skLineSegment(sketch, "E1299", {"start": v(4.83, 42.37) * mm, "end": v(4.38, 42.4) * mm});
            skLineSegment(sketch, "E1300", {"start": v(4.38, 42.4) * mm, "end": v(3.94, 42.44) * mm});
            skLineSegment(sketch, "E1301", {"start": v(3.94, 42.44) * mm, "end": v(3.5, 42.48) * mm});
            skLineSegment(sketch, "E1302", {"start": v(3.5, 42.48) * mm, "end": v(3.05, 42.52) * mm});
            skLineSegment(sketch, "E1303", {"start": v(3.05, 42.52) * mm, "end": v(2.6, 42.55) * mm});
            skLineSegment(sketch, "E1304", {"start": v(2.6, 42.55) * mm, "end": v(2.16, 42.6) * mm});
            skLineSegment(sketch, "E1305", {"start": v(2.16, 42.6) * mm, "end": v(1.72, 42.63) * mm});
            skLineSegment(sketch, "E1306", {"start": v(1.72, 42.63) * mm, "end": v(1.28, 42.66) * mm});
            skLineSegment(sketch, "E1307", {"start": v(1.28, 42.66) * mm, "end": v(0.83, 42.7) * mm});
            skLineSegment(sketch, "E1308", {"start": v(0.83, 42.7) * mm, "end": v(0.5, 42.73) * mm});
            skLineSegment(sketch, "E1309", {"start": v(0.5, 42.73) * mm, "end": v(0.52, 43.17) * mm});
            skLineSegment(sketch, "E1310", {"start": v(0.52, 43.17) * mm, "end": v(0.54, 43.62) * mm});
            skLineSegment(sketch, "E1311", {"start": v(0.54, 43.62) * mm, "end": v(0.56, 44.06) * mm});
            skLineSegment(sketch, "E1312", {"start": v(0.56, 44.06) * mm, "end": v(0.59, 44.5) * mm});
            skLineSegment(sketch, "E1313", {"start": v(0.59, 44.5) * mm, "end": v(0.6, 44.95) * mm});
            skLineSegment(sketch, "E1314", {"start": v(0.6, 44.95) * mm, "end": v(0.63, 45.4) * mm});
            skLineSegment(sketch, "E1315", {"start": v(0.63, 45.4) * mm, "end": v(0.66, 45.84) * mm});
            skLineSegment(sketch, "E1316", {"start": v(0.66, 45.84) * mm, "end": v(0.68, 46.29) * mm});
            skLineSegment(sketch, "E1317", {"start": v(0.68, 46.29) * mm, "end": v(0.7, 46.73) * mm});
            skLineSegment(sketch, "E1318", {"start": v(0.7, 46.73) * mm, "end": v(0.73, 47.18) * mm});
            skLineSegment(sketch, "E1319", {"start": v(0.73, 47.18) * mm, "end": v(0.75, 47.62) * mm});
            skLineSegment(sketch, "E1320", {"start": v(0.75, 47.62) * mm, "end": v(0.77, 48.07) * mm});
            skLineSegment(sketch, "E1321", {"start": v(0.77, 48.07) * mm, "end": v(0.8, 48.52) * mm});
            skLineSegment(sketch, "E1322", {"start": v(0.8, 48.52) * mm, "end": v(0.82, 48.96) * mm});
            skLineSegment(sketch, "E1323", {"start": v(0.82, 48.96) * mm, "end": v(0.84, 49.4) * mm});
            skLineSegment(sketch, "E1324", {"start": v(0.84, 49.4) * mm, "end": v(0.87, 49.85) * mm});
            skLineSegment(sketch, "E1325", {"start": v(0.87, 49.85) * mm, "end": v(0.87, 50) * mm});
            skLineSegment(sketch, "E1326", {"start": v(0.87, 50) * mm, "end": v(0.43, 50) * mm});
            skLineSegment(sketch, "E1327", {"start": v(0.43, 50) * mm, "end": v(-0.02, 50) * mm});
            skLineSegment(sketch, "E1328", {"start": v(-0.02, 50) * mm, "end": v(-0.44, 50) * mm});
            skLineSegment(sketch, "E1329", {"start": v(-0.44, 50) * mm, "end": v(-0.55, 49.57) * mm});
            skLineSegment(sketch, "E1330", {"start": v(-0.55, 49.57) * mm, "end": v(-0.66, 49.13) * mm});
            skLineSegment(sketch, "E1331", {"start": v(-0.66, 49.13) * mm, "end": v(-0.77, 48.7) * mm});
            skLineSegment(sketch, "E1332", {"start": v(-0.77, 48.7) * mm, "end": v(-0.88, 48.27) * mm});
            skLineSegment(sketch, "E1333", {"start": v(-0.88, 48.27) * mm, "end": v(-1, 47.84) * mm});
            skLineSegment(sketch, "E1334", {"start": v(-1, 47.84) * mm, "end": v(-1.1, 47.4) * mm});
            skLineSegment(sketch, "E1335", {"start": v(-1.1, 47.4) * mm, "end": v(-1.21, 46.98) * mm});
            skLineSegment(sketch, "E1336", {"start": v(-1.21, 46.98) * mm, "end": v(-1.32, 46.55) * mm});
            skLineSegment(sketch, "E1337", {"start": v(-1.32, 46.55) * mm, "end": v(-1.43, 46.11) * mm});
            skLineSegment(sketch, "E1338", {"start": v(-1.43, 46.11) * mm, "end": v(-1.54, 45.68) * mm});
            skLineSegment(sketch, "E1339", {"start": v(-1.54, 45.68) * mm, "end": v(-1.66, 45.25) * mm});
            skLineSegment(sketch, "E1340", {"start": v(-1.66, 45.25) * mm, "end": v(-1.77, 44.82) * mm});
            skLineSegment(sketch, "E1341", {"start": v(-1.77, 44.82) * mm, "end": v(-1.88, 44.39) * mm});
            skLineSegment(sketch, "E1342", {"start": v(-1.88, 44.39) * mm, "end": v(-1.99, 43.96) * mm});
            skLineSegment(sketch, "E1343", {"start": v(-1.99, 43.96) * mm, "end": v(-2.1, 43.52) * mm});
            skLineSegment(sketch, "E1344", {"start": v(-2.1, 43.52) * mm, "end": v(-2.2, 43.1) * mm});
            skLineSegment(sketch, "E1345", {"start": v(-2.2, 43.1) * mm, "end": v(-2.32, 42.67) * mm});
            skLineSegment(sketch, "E1346", {"start": v(-2.32, 42.67) * mm, "end": v(-2.76, 42.61) * mm});
            skLineSegment(sketch, "E1347", {"start": v(-2.76, 42.61) * mm, "end": v(-3.2, 42.56) * mm});
            skLineSegment(sketch, "E1348", {"start": v(-3.2, 42.56) * mm, "end": v(-3.64, 42.5) * mm});
            skLineSegment(sketch, "E1349", {"start": v(-3.64, 42.5) * mm, "end": v(-4.09, 42.45) * mm});
            skLineSegment(sketch, "E1350", {"start": v(-4.09, 42.45) * mm, "end": v(-4.53, 42.39) * mm});
            skLineSegment(sketch, "E1351", {"start": v(-4.53, 42.39) * mm, "end": v(-4.97, 42.33) * mm});
            skLineSegment(sketch, "E1352", {"start": v(-4.97, 42.33) * mm, "end": v(-5.41, 42.28) * mm});
            skLineSegment(sketch, "E1353", {"start": v(-5.41, 42.28) * mm, "end": v(-5.85, 42.22) * mm});
            skLineSegment(sketch, "E1354", {"start": v(-5.85, 42.22) * mm, "end": v(-6.3, 42.17) * mm});
            skLineSegment(sketch, "E1355", {"start": v(-6.3, 42.17) * mm, "end": v(-6.74, 42.1) * mm});
            skLineSegment(sketch, "E1356", {"start": v(-6.74, 42.1) * mm, "end": v(-7.18, 42.05) * mm});
            skLineSegment(sketch, "E1357", {"start": v(-7.18, 42.05) * mm, "end": v(-7.62, 42) * mm});
            skLineSegment(sketch, "E1358", {"start": v(-7.62, 42) * mm, "end": v(-8.06, 41.94) * mm});
            skLineSegment(sketch, "E1359", {"start": v(-8.06, 41.94) * mm, "end": v(-8.4, 41.9) * mm});
            skLineSegment(sketch, "E1360", {"start": v(-8.4, 41.9) * mm, "end": v(-8.47, 42.34) * mm});
            skLineSegment(sketch, "E1361", {"start": v(-8.47, 42.34) * mm, "end": v(-8.54, 42.78) * mm});
            skLineSegment(sketch, "E1362", {"start": v(-8.54, 42.78) * mm, "end": v(-8.61, 43.22) * mm});
            skLineSegment(sketch, "E1363", {"start": v(-8.61, 43.22) * mm, "end": v(-8.68, 43.66) * mm});
            skLineSegment(sketch, "E1364", {"start": v(-8.68, 43.66) * mm, "end": v(-8.75, 44.1) * mm});
            skLineSegment(sketch, "E1365", {"start": v(-8.75, 44.1) * mm, "end": v(-8.82, 44.54) * mm});
            skLineSegment(sketch, "E1366", {"start": v(-8.82, 44.54) * mm, "end": v(-8.9, 44.98) * mm});
            skLineSegment(sketch, "E1367", {"start": v(-8.9, 44.98) * mm, "end": v(-8.96, 45.42) * mm});
            skLineSegment(sketch, "E1368", {"start": v(-8.96, 45.42) * mm, "end": v(-9.03, 45.86) * mm});
            skLineSegment(sketch, "E1369", {"start": v(-9.03, 45.86) * mm, "end": v(-9.1, 46.3) * mm});
            skLineSegment(sketch, "E1370", {"start": v(-9.1, 46.3) * mm, "end": v(-9.17, 46.74) * mm});
            skLineSegment(sketch, "E1371", {"start": v(-9.17, 46.74) * mm, "end": v(-9.24, 47.18) * mm});
            skLineSegment(sketch, "E1372", {"start": v(-9.24, 47.18) * mm, "end": v(-9.3, 47.62) * mm});
            skLineSegment(sketch, "E1373", {"start": v(-9.3, 47.62) * mm, "end": v(-9.38, 48.06) * mm});
            skLineSegment(sketch, "E1374", {"start": v(-9.38, 48.06) * mm, "end": v(-9.45, 48.5) * mm});
            skLineSegment(sketch, "E1375", {"start": v(-9.45, 48.5) * mm, "end": v(-9.52, 48.94) * mm});
            skLineSegment(sketch, "E1376", {"start": v(-9.52, 48.94) * mm, "end": v(-9.54, 49.08) * mm});
            skLineSegment(sketch, "E1377", {"start": v(-9.54, 49.08) * mm, "end": v(-9.98, 49) * mm});
            skLineSegment(sketch, "E1378", {"start": v(-9.98, 49) * mm, "end": v(-10.41, 48.9) * mm});
            skLineSegment(sketch, "E1379", {"start": v(-10.41, 48.9) * mm, "end": v(-10.82, 48.81) * mm});
            skLineSegment(sketch, "E1380", {"start": v(-10.82, 48.81) * mm, "end": v(-10.84, 48.37) * mm});
            skLineSegment(sketch, "E1381", {"start": v(-10.84, 48.37) * mm, "end": v(-10.86, 47.92) * mm});
            skLineSegment(sketch, "E1382", {"start": v(-10.86, 47.92) * mm, "end": v(-10.88, 47.48) * mm});
            skLineSegment(sketch, "E1383", {"start": v(-10.88, 47.48) * mm, "end": v(-10.9, 47.03) * mm});
            skLineSegment(sketch, "E1384", {"start": v(-10.9, 47.03) * mm, "end": v(-10.92, 46.59) * mm});
            skLineSegment(sketch, "E1385", {"start": v(-10.92, 46.59) * mm, "end": v(-10.93, 46.14) * mm});
            skLineSegment(sketch, "E1386", {"start": v(-10.93, 46.14) * mm, "end": v(-10.95, 45.7) * mm});
            skLineSegment(sketch, "E1387", {"start": v(-10.95, 45.7) * mm, "end": v(-10.97, 45.25) * mm});
            skLineSegment(sketch, "E1388", {"start": v(-10.97, 45.25) * mm, "end": v(-10.99, 44.8) * mm});
            skLineSegment(sketch, "E1389", {"start": v(-10.99, 44.8) * mm, "end": v(-11, 44.36) * mm});
            skLineSegment(sketch, "E1390", {"start": v(-11, 44.36) * mm, "end": v(-11.03, 43.92) * mm});
            skLineSegment(sketch, "E1391", {"start": v(-11.03, 43.92) * mm, "end": v(-11.05, 43.47) * mm});
            skLineSegment(sketch, "E1392", {"start": v(-11.05, 43.47) * mm, "end": v(-11.06, 43.03) * mm});
            skLineSegment(sketch, "E1393", {"start": v(-11.06, 43.03) * mm, "end": v(-11.08, 42.58) * mm});
            skLineSegment(sketch, "E1394", {"start": v(-11.08, 42.58) * mm, "end": v(-11.1, 42.14) * mm});
            skLineSegment(sketch, "E1395", {"start": v(-11.1, 42.14) * mm, "end": v(-11.12, 41.7) * mm});
            skLineSegment(sketch, "E1396", {"start": v(-11.12, 41.7) * mm, "end": v(-11.14, 41.26) * mm});
            skLineSegment(sketch, "E1397", {"start": v(-11.14, 41.26) * mm, "end": v(-11.56, 41.1) * mm});
            skLineSegment(sketch, "E1398", {"start": v(-11.56, 41.1) * mm, "end": v(-11.98, 40.96) * mm});
            skLineSegment(sketch, "E1399", {"start": v(-11.98, 40.96) * mm, "end": v(-12.4, 40.82) * mm});
            skLineSegment(sketch, "E1400", {"start": v(-12.4, 40.82) * mm, "end": v(-12.82, 40.67) * mm});
            skLineSegment(sketch, "E1401", {"start": v(-12.82, 40.67) * mm, "end": v(-13.24, 40.52) * mm});
            skLineSegment(sketch, "E1402", {"start": v(-13.24, 40.52) * mm, "end": v(-13.66, 40.38) * mm});
            skLineSegment(sketch, "E1403", {"start": v(-13.66, 40.38) * mm, "end": v(-14.08, 40.23) * mm});
            skLineSegment(sketch, "E1404", {"start": v(-14.08, 40.23) * mm, "end": v(-14.5, 40.08) * mm});
            skLineSegment(sketch, "E1405", {"start": v(-14.5, 40.08) * mm, "end": v(-14.93, 39.93) * mm});
            skLineSegment(sketch, "E1406", {"start": v(-14.93, 39.93) * mm, "end": v(-15.35, 39.79) * mm});
            skLineSegment(sketch, "E1407", {"start": v(-15.35, 39.79) * mm, "end": v(-15.77, 39.64) * mm});
            skLineSegment(sketch, "E1408", {"start": v(-15.77, 39.64) * mm, "end": v(-16.19, 39.5) * mm});
            skLineSegment(sketch, "E1409", {"start": v(-16.19, 39.5) * mm, "end": v(-16.6, 39.35) * mm});
            skLineSegment(sketch, "E1410", {"start": v(-16.6, 39.35) * mm, "end": v(-16.93, 39.24) * mm});
            skLineSegment(sketch, "E1411", {"start": v(-16.93, 39.24) * mm, "end": v(-17.09, 39.65) * mm});
            skLineSegment(sketch, "E1412", {"start": v(-17.09, 39.65) * mm, "end": v(-17.25, 40.07) * mm});
            skLineSegment(sketch, "E1413", {"start": v(-17.25, 40.07) * mm, "end": v(-17.4, 40.48) * mm});
            skLineSegment(sketch, "E1414", {"start": v(-17.4, 40.48) * mm, "end": v(-17.57, 40.9) * mm});
            skLineSegment(sketch, "E1415", {"start": v(-17.57, 40.9) * mm, "end": v(-17.73, 41.32) * mm});
            skLineSegment(sketch, "E1416", {"start": v(-17.73, 41.32) * mm, "end": v(-17.89, 41.73) * mm});
            skLineSegment(sketch, "E1417", {"start": v(-17.89, 41.73) * mm, "end": v(-18.05, 42.15) * mm});
            skLineSegment(sketch, "E1418", {"start": v(-18.05, 42.15) * mm, "end": v(-18.2, 42.56) * mm});
            skLineSegment(sketch, "E1419", {"start": v(-18.2, 42.56) * mm, "end": v(-18.37, 42.98) * mm});
            skLineSegment(sketch, "E1420", {"start": v(-18.37, 42.98) * mm, "end": v(-18.53, 43.4) * mm});
            skLineSegment(sketch, "E1421", {"start": v(-18.53, 43.4) * mm, "end": v(-18.69, 43.81) * mm});
            skLineSegment(sketch, "E1422", {"start": v(-18.69, 43.81) * mm, "end": v(-18.85, 44.23) * mm});
            skLineSegment(sketch, "E1423", {"start": v(-18.85, 44.23) * mm, "end": v(-19, 44.64) * mm});
            skLineSegment(sketch, "E1424", {"start": v(-19, 44.64) * mm, "end": v(-19.17, 45.06) * mm});
            skLineSegment(sketch, "E1425", {"start": v(-19.17, 45.06) * mm, "end": v(-19.33, 45.48) * mm});
            skLineSegment(sketch, "E1426", {"start": v(-19.33, 45.48) * mm, "end": v(-19.49, 45.9) * mm});
            skLineSegment(sketch, "E1427", {"start": v(-19.49, 45.9) * mm, "end": v(-19.54, 46.03) * mm});
            skLineSegment(sketch, "E1428", {"start": v(-19.54, 46.03) * mm, "end": v(-19.94, 45.85) * mm});
            skLineSegment(sketch, "E1429", {"start": v(-19.94, 45.85) * mm, "end": v(-20.35, 45.67) * mm});
            skLineSegment(sketch, "E1430", {"start": v(-20.35, 45.67) * mm, "end": v(-20.73, 45.5) * mm});
            skLineSegment(sketch, "E1431", {"start": v(-20.73, 45.5) * mm, "end": v(-20.66, 45.06) * mm});
            skLineSegment(sketch, "E1432", {"start": v(-20.66, 45.06) * mm, "end": v(-20.59, 44.62) * mm});
            skLineSegment(sketch, "E1433", {"start": v(-20.59, 44.62) * mm, "end": v(-20.51, 44.18) * mm});
            skLineSegment(sketch, "E1434", {"start": v(-20.51, 44.18) * mm, "end": v(-20.44, 43.74) * mm});
            skLineSegment(sketch, "E1435", {"start": v(-20.44, 43.74) * mm, "end": v(-20.36, 43.3) * mm});
            skLineSegment(sketch, "E1436", {"start": v(-20.36, 43.3) * mm, "end": v(-20.29, 42.86) * mm});
            skLineSegment(sketch, "E1437", {"start": v(-20.29, 42.86) * mm, "end": v(-20.21, 42.42) * mm});
            skLineSegment(sketch, "E1438", {"start": v(-20.21, 42.42) * mm, "end": v(-20.14, 41.98) * mm});
            skLineSegment(sketch, "E1439", {"start": v(-20.14, 41.98) * mm, "end": v(-20.07, 41.54) * mm});
            skLineSegment(sketch, "E1440", {"start": v(-20.07, 41.54) * mm, "end": v(-20, 41.1) * mm});
            skLineSegment(sketch, "E1441", {"start": v(-20, 41.1) * mm, "end": v(-19.92, 40.66) * mm});
            skLineSegment(sketch, "E1442", {"start": v(-19.92, 40.66) * mm, "end": v(-19.84, 40.23) * mm});
            skLineSegment(sketch, "E1443", {"start": v(-19.84, 40.23) * mm, "end": v(-19.77, 39.79) * mm});
            skLineSegment(sketch, "E1444", {"start": v(-19.77, 39.79) * mm, "end": v(-19.7, 39.35) * mm});
            skLineSegment(sketch, "E1445", {"start": v(-19.7, 39.35) * mm, "end": v(-19.62, 38.9) * mm});
            skLineSegment(sketch, "E1446", {"start": v(-19.62, 38.9) * mm, "end": v(-19.55, 38.47) * mm});
            skLineSegment(sketch, "E1447", {"start": v(-19.55, 38.47) * mm, "end": v(-19.47, 38.04) * mm});
            skLineSegment(sketch, "E1448", {"start": v(-19.47, 38.04) * mm, "end": v(-19.85, 37.8) * mm});
            skLineSegment(sketch, "E1449", {"start": v(-19.85, 37.8) * mm, "end": v(-20.23, 37.58) * mm});
            skLineSegment(sketch, "E1450", {"start": v(-20.23, 37.58) * mm, "end": v(-20.62, 37.35) * mm});
            skLineSegment(sketch, "E1451", {"start": v(-20.62, 37.35) * mm, "end": v(-21, 37.11) * mm});
            skLineSegment(sketch, "E1452", {"start": v(-21, 37.11) * mm, "end": v(-21.38, 36.88) * mm});
            skLineSegment(sketch, "E1453", {"start": v(-21.38, 36.88) * mm, "end": v(-21.76, 36.65) * mm});
            skLineSegment(sketch, "E1454", {"start": v(-21.76, 36.65) * mm, "end": v(-22.14, 36.42) * mm});
            skLineSegment(sketch, "E1455", {"start": v(-22.14, 36.42) * mm, "end": v(-22.52, 36.2) * mm});
            skLineSegment(sketch, "E1456", {"start": v(-22.52, 36.2) * mm, "end": v(-22.9, 35.96) * mm});
            skLineSegment(sketch, "E1457", {"start": v(-22.9, 35.96) * mm, "end": v(-23.28, 35.73) * mm});
            skLineSegment(sketch, "E1458", {"start": v(-23.28, 35.73) * mm, "end": v(-23.66, 35.5) * mm});
            skLineSegment(sketch, "E1459", {"start": v(-23.66, 35.5) * mm, "end": v(-24.05, 35.27) * mm});
            skLineSegment(sketch, "E1460", {"start": v(-24.05, 35.27) * mm, "end": v(-24.43, 35.03) * mm});
            skLineSegment(sketch, "E1461", {"start": v(-24.43, 35.03) * mm, "end": v(-24.72, 34.86) * mm});
            skLineSegment(sketch, "E1462", {"start": v(-24.72, 34.86) * mm, "end": v(-24.96, 35.23) * mm});
            skLineSegment(sketch, "E1463", {"start": v(-24.96, 35.23) * mm, "end": v(-25.2, 35.6) * mm});
            skLineSegment(sketch, "E1464", {"start": v(-25.2, 35.6) * mm, "end": v(-25.45, 35.98) * mm});
            skLineSegment(sketch, "E1465", {"start": v(-25.45, 35.98) * mm, "end": v(-25.69, 36.35) * mm});
            skLineSegment(sketch, "E1466", {"start": v(-25.69, 36.35) * mm, "end": v(-25.93, 36.73) * mm});
            skLineSegment(sketch, "E1467", {"start": v(-25.93, 36.73) * mm, "end": v(-26.17, 37.1) * mm});
            skLineSegment(sketch, "E1468", {"start": v(-26.17, 37.1) * mm, "end": v(-26.42, 37.47) * mm});
            skLineSegment(sketch, "E1469", {"start": v(-26.42, 37.47) * mm, "end": v(-26.66, 37.85) * mm});
            skLineSegment(sketch, "E1470", {"start": v(-26.66, 37.85) * mm, "end": v(-26.9, 38.22) * mm});
            skLineSegment(sketch, "E1471", {"start": v(-26.9, 38.22) * mm, "end": v(-27.14, 38.6) * mm});
            skLineSegment(sketch, "E1472", {"start": v(-27.14, 38.6) * mm, "end": v(-27.39, 38.97) * mm});
            skLineSegment(sketch, "E1473", {"start": v(-27.39, 38.97) * mm, "end": v(-27.63, 39.34) * mm});
            skLineSegment(sketch, "E1474", {"start": v(-27.63, 39.34) * mm, "end": v(-27.87, 39.72) * mm});
            skLineSegment(sketch, "E1475", {"start": v(-27.87, 39.72) * mm, "end": v(-28.12, 40.1) * mm});
            skLineSegment(sketch, "E1476", {"start": v(-28.12, 40.1) * mm, "end": v(-28.36, 40.46) * mm});
            skLineSegment(sketch, "E1477", {"start": v(-28.36, 40.46) * mm, "end": v(-28.6, 40.84) * mm});
            skLineSegment(sketch, "E1478", {"start": v(-28.6, 40.84) * mm, "end": v(-28.68, 40.96) * mm});
            skLineSegment(sketch, "E1479", {"start": v(-28.68, 40.96) * mm, "end": v(-29.04, 40.7) * mm});
            skLineSegment(sketch, "E1480", {"start": v(-29.04, 40.7) * mm, "end": v(-29.4, 40.44) * mm});
            skLineSegment(sketch, "E1481", {"start": v(-29.4, 40.44) * mm, "end": v(-29.74, 40.2) * mm});
            skLineSegment(sketch, "E1482", {"start": v(-29.74, 40.2) * mm, "end": v(-29.58, 39.78) * mm});
            skLineSegment(sketch, "E1483", {"start": v(-29.58, 39.78) * mm, "end": v(-29.41, 39.36) * mm});
            skLineSegment(sketch, "E1484", {"start": v(-29.41, 39.36) * mm, "end": v(-29.25, 38.95) * mm});
            skLineSegment(sketch, "E1485", {"start": v(-29.25, 38.95) * mm, "end": v(-29.08, 38.54) * mm});
            skLineSegment(sketch, "E1486", {"start": v(-29.08, 38.54) * mm, "end": v(-28.92, 38.12) * mm});
            skLineSegment(sketch, "E1487", {"start": v(-28.92, 38.12) * mm, "end": v(-28.76, 37.7) * mm});
            skLineSegment(sketch, "E1488", {"start": v(-28.76, 37.7) * mm, "end": v(-28.6, 37.3) * mm});
            skLineSegment(sketch, "E1489", {"start": v(-28.6, 37.3) * mm, "end": v(-28.43, 36.88) * mm});
            skLineSegment(sketch, "E1490", {"start": v(-28.43, 36.88) * mm, "end": v(-28.26, 36.46) * mm});
            skLineSegment(sketch, "E1491", {"start": v(-28.26, 36.46) * mm, "end": v(-28.1, 36.05) * mm});
            skLineSegment(sketch, "E1492", {"start": v(-28.1, 36.05) * mm, "end": v(-27.94, 35.64) * mm});
            skLineSegment(sketch, "E1493", {"start": v(-27.94, 35.64) * mm, "end": v(-27.77, 35.22) * mm});
            skLineSegment(sketch, "E1494", {"start": v(-27.77, 35.22) * mm, "end": v(-27.6, 34.8) * mm});
            skLineSegment(sketch, "E1495", {"start": v(-27.6, 34.8) * mm, "end": v(-27.44, 34.4) * mm});
            skLineSegment(sketch, "E1496", {"start": v(-27.44, 34.4) * mm, "end": v(-27.28, 33.98) * mm});
            skLineSegment(sketch, "E1497", {"start": v(-27.28, 33.98) * mm, "end": v(-27.12, 33.56) * mm});
            skLineSegment(sketch, "E1498", {"start": v(-27.12, 33.56) * mm, "end": v(-26.96, 33.16) * mm});
            skLineSegment(sketch, "E1499", {"start": v(-26.96, 33.16) * mm, "end": v(-27.28, 32.85) * mm});
            skLineSegment(sketch, "E1500", {"start": v(-27.28, 32.85) * mm, "end": v(-27.6, 32.55) * mm});
            skLineSegment(sketch, "E1501", {"start": v(-27.6, 32.55) * mm, "end": v(-27.93, 32.24) * mm});
            skLineSegment(sketch, "E1502", {"start": v(-27.93, 32.24) * mm, "end": v(-28.25, 31.94) * mm});
            skLineSegment(sketch, "E1503", {"start": v(-28.25, 31.94) * mm, "end": v(-28.58, 31.63) * mm});
            skLineSegment(sketch, "E1504", {"start": v(-28.58, 31.63) * mm, "end": v(-28.9, 31.33) * mm});
            skLineSegment(sketch, "E1505", {"start": v(-28.9, 31.33) * mm, "end": v(-29.23, 31.02) * mm});
            skLineSegment(sketch, "E1506", {"start": v(-29.23, 31.02) * mm, "end": v(-29.55, 30.72) * mm});
            skLineSegment(sketch, "E1507", {"start": v(-29.55, 30.72) * mm, "end": v(-29.88, 30.41) * mm});
            skLineSegment(sketch, "E1508", {"start": v(-29.88, 30.41) * mm, "end": v(-30.2, 30.1) * mm});
            skLineSegment(sketch, "E1509", {"start": v(-30.2, 30.1) * mm, "end": v(-30.53, 29.8) * mm});
            skLineSegment(sketch, "E1510", {"start": v(-30.53, 29.8) * mm, "end": v(-30.85, 29.5) * mm});
            skLineSegment(sketch, "E1511", {"start": v(-30.85, 29.5) * mm, "end": v(-31.18, 29.2) * mm});
            skLineSegment(sketch, "E1512", {"start": v(-31.18, 29.2) * mm, "end": v(-31.43, 28.96) * mm});
            skLineSegment(sketch, "E1513", {"start": v(-31.43, 28.96) * mm, "end": v(-31.74, 29.27) * mm});
            skLineSegment(sketch, "E1514", {"start": v(-31.74, 29.27) * mm, "end": v(-32.06, 29.59) * mm});
            skLineSegment(sketch, "E1515", {"start": v(-32.06, 29.59) * mm, "end": v(-32.37, 29.9) * mm});
            skLineSegment(sketch, "E1516", {"start": v(-32.37, 29.9) * mm, "end": v(-32.69, 30.22) * mm});
            skLineSegment(sketch, "E1517", {"start": v(-32.69, 30.22) * mm, "end": v(-33, 30.53) * mm});
            skLineSegment(sketch, "E1518", {"start": v(-33, 30.53) * mm, "end": v(-33.32, 30.85) * mm});
            skLineSegment(sketch, "E1519", {"start": v(-33.32, 30.85) * mm, "end": v(-33.63, 31.16) * mm});
            skLineSegment(sketch, "E1520", {"start": v(-33.63, 31.16) * mm, "end": v(-33.95, 31.48) * mm});
            skLineSegment(sketch, "E1521", {"start": v(-33.95, 31.48) * mm, "end": v(-34.26, 31.8) * mm});
            skLineSegment(sketch, "E1522", {"start": v(-34.26, 31.8) * mm, "end": v(-34.58, 32.1) * mm});
            skLineSegment(sketch, "E1523", {"start": v(-34.58, 32.1) * mm, "end": v(-34.9, 32.42) * mm});
            skLineSegment(sketch, "E1524", {"start": v(-34.9, 32.42) * mm, "end": v(-35.2, 32.74) * mm});
            skLineSegment(sketch, "E1525", {"start": v(-35.2, 32.74) * mm, "end": v(-35.52, 33.05) * mm});
            skLineSegment(sketch, "E1526", {"start": v(-35.52, 33.05) * mm, "end": v(-35.84, 33.37) * mm});
            skLineSegment(sketch, "E1527", {"start": v(-35.84, 33.37) * mm, "end": v(-36.15, 33.68) * mm});
            skLineSegment(sketch, "E1528", {"start": v(-36.15, 33.68) * mm, "end": v(-36.47, 34) * mm});
            skLineSegment(sketch, "E1529", {"start": v(-36.47, 34) * mm, "end": v(-36.57, 34.1) * mm});
            skLineSegment(sketch, "E1530", {"start": v(-5.65, 2.24) * mm, "end": v(-5.5, 2.59) * mm});
            skLineSegment(sketch, "E1531", {"start": v(-5.5, 2.59) * mm, "end": v(-5.32, 2.93) * mm});
            skLineSegment(sketch, "E1532", {"start": v(-5.32, 2.93) * mm, "end": v(-5.13, 3.25) * mm});
            skLineSegment(sketch, "E1533", {"start": v(-5.13, 3.25) * mm, "end": v(-4.91, 3.57) * mm});
            skLineSegment(sketch, "E1534", {"start": v(-4.91, 3.57) * mm, "end": v(-4.68, 3.87) * mm});
            skLineSegment(sketch, "E1535", {"start": v(-4.68, 3.87) * mm, "end": v(-4.43, 4.16) * mm});
            skLineSegment(sketch, "E1536", {"start": v(-4.43, 4.16) * mm, "end": v(-4.16, 4.43) * mm});
            skLineSegment(sketch, "E1537", {"start": v(-4.16, 4.43) * mm, "end": v(-3.87, 4.68) * mm});
            skLineSegment(sketch, "E1538", {"start": v(-3.87, 4.68) * mm, "end": v(-3.57, 4.91) * mm});
            skLineSegment(sketch, "E1539", {"start": v(-3.57, 4.91) * mm, "end": v(-3.25, 5.13) * mm});
            skLineSegment(sketch, "E1540", {"start": v(-3.25, 5.13) * mm, "end": v(-2.93, 5.32) * mm});
            skLineSegment(sketch, "E1541", {"start": v(-2.93, 5.32) * mm, "end": v(-2.59, 5.5) * mm});
            skLineSegment(sketch, "E1542", {"start": v(-2.59, 5.5) * mm, "end": v(-2.24, 5.65) * mm});
            skLineSegment(sketch, "E1543", {"start": v(-2.24, 5.65) * mm, "end": v(-2.15, 5.68) * mm});
            skLineSegment(sketch, "E1544", {"start": v(-2.15, 5.68) * mm, "end": v(-2.25, 38.39) * mm});
            skLineSegment(sketch, "E1545", {"start": v(-2.25, 38.39) * mm, "end": v(-2.41, 38.38) * mm});
            skLineSegment(sketch, "E1546", {"start": v(-2.41, 38.38) * mm, "end": v(-4.82, 38.15) * mm});
            skLineSegment(sketch, "E1547", {"start": v(-4.82, 38.15) * mm, "end": v(-7.2, 37.78) * mm});
            skLineSegment(sketch, "E1548", {"start": v(-7.2, 37.78) * mm, "end": v(-9.56, 37.25) * mm});
            skLineSegment(sketch, "E1549", {"start": v(-9.56, 37.25) * mm, "end": v(-11.88, 36.58) * mm});
            skLineSegment(sketch, "E1550", {"start": v(-11.88, 36.58) * mm, "end": v(-14.16, 35.76) * mm});
            skLineSegment(sketch, "E1551", {"start": v(-14.16, 35.76) * mm, "end": v(-16.37, 34.8) * mm});
            skLineSegment(sketch, "E1552", {"start": v(-16.37, 34.8) * mm, "end": v(-18.53, 33.7) * mm});
            skLineSegment(sketch, "E1553", {"start": v(-18.53, 33.7) * mm, "end": v(-20.6, 32.47) * mm});
            skLineSegment(sketch, "E1554", {"start": v(-20.6, 32.47) * mm, "end": v(-22.6, 31.11) * mm});
            skLineSegment(sketch, "E1555", {"start": v(-22.6, 31.11) * mm, "end": v(-24.51, 29.63) * mm});
            skLineSegment(sketch, "E1556", {"start": v(-24.51, 29.63) * mm, "end": v(-26.33, 28.03) * mm});
            skLineSegment(sketch, "E1557", {"start": v(-26.33, 28.03) * mm, "end": v(-28.03, 26.33) * mm});
            skLineSegment(sketch, "E1558", {"start": v(-28.03, 26.33) * mm, "end": v(-29.63, 24.51) * mm});
            skLineSegment(sketch, "E1559", {"start": v(-29.63, 24.51) * mm, "end": v(-31.11, 22.6) * mm});
            skLineSegment(sketch, "E1560", {"start": v(-31.11, 22.6) * mm, "end": v(-32.47, 20.6) * mm});
            skLineSegment(sketch, "E1561", {"start": v(-32.47, 20.6) * mm, "end": v(-33.7, 18.53) * mm});
            skLineSegment(sketch, "E1562", {"start": v(-33.7, 18.53) * mm, "end": v(-34.8, 16.37) * mm});
            skLineSegment(sketch, "E1563", {"start": v(-34.8, 16.37) * mm, "end": v(-35.76, 14.16) * mm});
            skLineSegment(sketch, "E1564", {"start": v(-35.76, 14.16) * mm, "end": v(-36.58, 11.88) * mm});
            skLineSegment(sketch, "E1565", {"start": v(-36.58, 11.88) * mm, "end": v(-37.25, 9.56) * mm});
            skLineSegment(sketch, "E1566", {"start": v(-37.25, 9.56) * mm, "end": v(-37.78, 7.2) * mm});
            skLineSegment(sketch, "E1567", {"start": v(-37.78, 7.2) * mm, "end": v(-38.15, 4.82) * mm});
            skLineSegment(sketch, "E1568", {"start": v(-38.15, 4.82) * mm, "end": v(-38.38, 2.41) * mm});
            skLineSegment(sketch, "E1569", {"start": v(-38.38, 2.41) * mm, "end": v(-38.39, 2.25) * mm});
            skLineSegment(sketch, "E1570", {"start": v(-38.39, 2.25) * mm, "end": v(-5.68, 2.15) * mm});
            skLineSegment(sketch, "E1571", {"start": v(-5.68, 2.15) * mm, "end": v(-5.65, 2.24) * mm});
            skLineSegment(sketch, "E1572", {"start": v(38.39, 2.25) * mm, "end": v(38.38, 2.41) * mm});
            skLineSegment(sketch, "E1573", {"start": v(38.38, 2.41) * mm, "end": v(38.15, 4.82) * mm});
            skLineSegment(sketch, "E1574", {"start": v(38.15, 4.82) * mm, "end": v(37.78, 7.2) * mm});
            skLineSegment(sketch, "E1575", {"start": v(37.78, 7.2) * mm, "end": v(37.25, 9.56) * mm});
            skLineSegment(sketch, "E1576", {"start": v(37.25, 9.56) * mm, "end": v(36.58, 11.88) * mm});
            skLineSegment(sketch, "E1577", {"start": v(36.58, 11.88) * mm, "end": v(35.76, 14.16) * mm});
            skLineSegment(sketch, "E1578", {"start": v(35.76, 14.16) * mm, "end": v(34.8, 16.37) * mm});
            skLineSegment(sketch, "E1579", {"start": v(34.8, 16.37) * mm, "end": v(33.7, 18.53) * mm});
            skLineSegment(sketch, "E1580", {"start": v(33.7, 18.53) * mm, "end": v(32.47, 20.6) * mm});
            skLineSegment(sketch, "E1581", {"start": v(32.47, 20.6) * mm, "end": v(31.11, 22.6) * mm});
            skLineSegment(sketch, "E1582", {"start": v(31.11, 22.6) * mm, "end": v(29.63, 24.51) * mm});
            skLineSegment(sketch, "E1583", {"start": v(29.63, 24.51) * mm, "end": v(28.03, 26.33) * mm});
            skLineSegment(sketch, "E1584", {"start": v(28.03, 26.33) * mm, "end": v(26.33, 28.03) * mm});
            skLineSegment(sketch, "E1585", {"start": v(26.33, 28.03) * mm, "end": v(24.51, 29.63) * mm});
            skLineSegment(sketch, "E1586", {"start": v(24.51, 29.63) * mm, "end": v(22.6, 31.11) * mm});
            skLineSegment(sketch, "E1587", {"start": v(22.6, 31.11) * mm, "end": v(20.6, 32.47) * mm});
            skLineSegment(sketch, "E1588", {"start": v(20.6, 32.47) * mm, "end": v(18.53, 33.7) * mm});
            skLineSegment(sketch, "E1589", {"start": v(18.53, 33.7) * mm, "end": v(16.37, 34.8) * mm});
            skLineSegment(sketch, "E1590", {"start": v(16.37, 34.8) * mm, "end": v(14.16, 35.76) * mm});
            skLineSegment(sketch, "E1591", {"start": v(14.16, 35.76) * mm, "end": v(11.88, 36.58) * mm});
            skLineSegment(sketch, "E1592", {"start": v(11.88, 36.58) * mm, "end": v(9.56, 37.25) * mm});
            skLineSegment(sketch, "E1593", {"start": v(9.56, 37.25) * mm, "end": v(7.2, 37.78) * mm});
            skLineSegment(sketch, "E1594", {"start": v(7.2, 37.78) * mm, "end": v(4.82, 38.15) * mm});
            skLineSegment(sketch, "E1595", {"start": v(4.82, 38.15) * mm, "end": v(2.41, 38.38) * mm});
            skLineSegment(sketch, "E1596", {"start": v(2.41, 38.38) * mm, "end": v(2.25, 38.39) * mm});
            skLineSegment(sketch, "E1597", {"start": v(2.25, 38.39) * mm, "end": v(2.15, 5.68) * mm});
            skLineSegment(sketch, "E1598", {"start": v(2.15, 5.68) * mm, "end": v(2.24, 5.65) * mm});
            skLineSegment(sketch, "E1599", {"start": v(2.24, 5.65) * mm, "end": v(2.59, 5.5) * mm});
            skLineSegment(sketch, "E1600", {"start": v(2.59, 5.5) * mm, "end": v(2.93, 5.32) * mm});
            skLineSegment(sketch, "E1601", {"start": v(2.93, 5.32) * mm, "end": v(3.25, 5.13) * mm});
            skLineSegment(sketch, "E1602", {"start": v(3.25, 5.13) * mm, "end": v(3.57, 4.91) * mm});
            skLineSegment(sketch, "E1603", {"start": v(3.57, 4.91) * mm, "end": v(3.87, 4.68) * mm});
            skLineSegment(sketch, "E1604", {"start": v(3.87, 4.68) * mm, "end": v(4.16, 4.43) * mm});
            skLineSegment(sketch, "E1605", {"start": v(4.16, 4.43) * mm, "end": v(4.43, 4.16) * mm});
            skLineSegment(sketch, "E1606", {"start": v(4.43, 4.16) * mm, "end": v(4.68, 3.87) * mm});
            skLineSegment(sketch, "E1607", {"start": v(4.68, 3.87) * mm, "end": v(4.91, 3.57) * mm});
            skLineSegment(sketch, "E1608", {"start": v(4.91, 3.57) * mm, "end": v(5.13, 3.25) * mm});
            skLineSegment(sketch, "E1609", {"start": v(5.13, 3.25) * mm, "end": v(5.32, 2.93) * mm});
            skLineSegment(sketch, "E1610", {"start": v(5.32, 2.93) * mm, "end": v(5.5, 2.59) * mm});
            skLineSegment(sketch, "E1611", {"start": v(5.5, 2.59) * mm, "end": v(5.65, 2.24) * mm});
            skLineSegment(sketch, "E1612", {"start": v(5.65, 2.24) * mm, "end": v(5.68, 2.15) * mm});
            skLineSegment(sketch, "E1613", {"start": v(5.68, 2.15) * mm, "end": v(38.39, 2.25) * mm});
            skLineSegment(sketch, "E1614", {"start": v(2.41, -38.38) * mm, "end": v(4.82, -38.15) * mm});
            skLineSegment(sketch, "E1615", {"start": v(4.82, -38.15) * mm, "end": v(7.2, -37.78) * mm});
            skLineSegment(sketch, "E1616", {"start": v(7.2, -37.78) * mm, "end": v(9.56, -37.25) * mm});
            skLineSegment(sketch, "E1617", {"start": v(9.56, -37.25) * mm, "end": v(11.88, -36.58) * mm});
            skLineSegment(sketch, "E1618", {"start": v(11.88, -36.58) * mm, "end": v(14.16, -35.76) * mm});
            skLineSegment(sketch, "E1619", {"start": v(14.16, -35.76) * mm, "end": v(16.37, -34.8) * mm});
            skLineSegment(sketch, "E1620", {"start": v(16.37, -34.8) * mm, "end": v(18.53, -33.7) * mm});
            skLineSegment(sketch, "E1621", {"start": v(18.53, -33.7) * mm, "end": v(20.6, -32.47) * mm});
            skLineSegment(sketch, "E1622", {"start": v(20.6, -32.47) * mm, "end": v(22.6, -31.11) * mm});
            skLineSegment(sketch, "E1623", {"start": v(22.6, -31.11) * mm, "end": v(24.51, -29.63) * mm});
            skLineSegment(sketch, "E1624", {"start": v(24.51, -29.63) * mm, "end": v(26.33, -28.03) * mm});
            skLineSegment(sketch, "E1625", {"start": v(26.33, -28.03) * mm, "end": v(28.03, -26.33) * mm});
            skLineSegment(sketch, "E1626", {"start": v(28.03, -26.33) * mm, "end": v(29.63, -24.51) * mm});
            skLineSegment(sketch, "E1627", {"start": v(29.63, -24.51) * mm, "end": v(31.11, -22.6) * mm});
            skLineSegment(sketch, "E1628", {"start": v(31.11, -22.6) * mm, "end": v(32.47, -20.6) * mm});
            skLineSegment(sketch, "E1629", {"start": v(32.47, -20.6) * mm, "end": v(33.7, -18.53) * mm});
            skLineSegment(sketch, "E1630", {"start": v(33.7, -18.53) * mm, "end": v(34.8, -16.37) * mm});
            skLineSegment(sketch, "E1631", {"start": v(34.8, -16.37) * mm, "end": v(35.76, -14.16) * mm});
            skLineSegment(sketch, "E1632", {"start": v(35.76, -14.16) * mm, "end": v(36.58, -11.88) * mm});
            skLineSegment(sketch, "E1633", {"start": v(36.58, -11.88) * mm, "end": v(37.25, -9.56) * mm});
            skLineSegment(sketch, "E1634", {"start": v(37.25, -9.56) * mm, "end": v(37.78, -7.2) * mm});
            skLineSegment(sketch, "E1635", {"start": v(37.78, -7.2) * mm, "end": v(38.15, -4.82) * mm});
            skLineSegment(sketch, "E1636", {"start": v(38.15, -4.82) * mm, "end": v(38.38, -2.41) * mm});
            skLineSegment(sketch, "E1637", {"start": v(38.38, -2.41) * mm, "end": v(38.39, -2.25) * mm});
            skLineSegment(sketch, "E1638", {"start": v(38.39, -2.25) * mm, "end": v(5.68, -2.15) * mm});
            skLineSegment(sketch, "E1639", {"start": v(5.68, -2.15) * mm, "end": v(5.65, -2.24) * mm});
            skLineSegment(sketch, "E1640", {"start": v(5.65, -2.24) * mm, "end": v(5.5, -2.59) * mm});
            skLineSegment(sketch, "E1641", {"start": v(5.5, -2.59) * mm, "end": v(5.32, -2.93) * mm});
            skLineSegment(sketch, "E1642", {"start": v(5.32, -2.93) * mm, "end": v(5.13, -3.25) * mm});
            skLineSegment(sketch, "E1643", {"start": v(5.13, -3.25) * mm, "end": v(4.91, -3.57) * mm});
            skLineSegment(sketch, "E1644", {"start": v(4.91, -3.57) * mm, "end": v(4.68, -3.87) * mm});
            skLineSegment(sketch, "E1645", {"start": v(4.68, -3.87) * mm, "end": v(4.43, -4.16) * mm});
            skLineSegment(sketch, "E1646", {"start": v(4.43, -4.16) * mm, "end": v(4.16, -4.43) * mm});
            skLineSegment(sketch, "E1647", {"start": v(4.16, -4.43) * mm, "end": v(3.87, -4.68) * mm});
            skLineSegment(sketch, "E1648", {"start": v(3.87, -4.68) * mm, "end": v(3.57, -4.91) * mm});
            skLineSegment(sketch, "E1649", {"start": v(3.57, -4.91) * mm, "end": v(3.25, -5.13) * mm});
            skLineSegment(sketch, "E1650", {"start": v(3.25, -5.13) * mm, "end": v(2.93, -5.32) * mm});
            skLineSegment(sketch, "E1651", {"start": v(2.93, -5.32) * mm, "end": v(2.59, -5.5) * mm});
            skLineSegment(sketch, "E1652", {"start": v(2.59, -5.5) * mm, "end": v(2.24, -5.65) * mm});
            skLineSegment(sketch, "E1653", {"start": v(2.24, -5.65) * mm, "end": v(2.15, -5.68) * mm});
            skLineSegment(sketch, "E1654", {"start": v(2.15, -5.68) * mm, "end": v(2.25, -38.39) * mm});
            skLineSegment(sketch, "E1655", {"start": v(2.25, -38.39) * mm, "end": v(2.41, -38.38) * mm});
            skLineSegment(sketch, "E1656", {"start": v(-2.15, -5.68) * mm, "end": v(-2.24, -5.65) * mm});
            skLineSegment(sketch, "E1657", {"start": v(-2.24, -5.65) * mm, "end": v(-2.59, -5.5) * mm});
            skLineSegment(sketch, "E1658", {"start": v(-2.59, -5.5) * mm, "end": v(-2.93, -5.32) * mm});
            skLineSegment(sketch, "E1659", {"start": v(-2.93, -5.32) * mm, "end": v(-3.25, -5.13) * mm});
            skLineSegment(sketch, "E1660", {"start": v(-3.25, -5.13) * mm, "end": v(-3.57, -4.91) * mm});
            skLineSegment(sketch, "E1661", {"start": v(-3.57, -4.91) * mm, "end": v(-3.87, -4.68) * mm});
            skLineSegment(sketch, "E1662", {"start": v(-3.87, -4.68) * mm, "end": v(-4.16, -4.43) * mm});
            skLineSegment(sketch, "E1663", {"start": v(-4.16, -4.43) * mm, "end": v(-4.43, -4.16) * mm});
            skLineSegment(sketch, "E1664", {"start": v(-4.43, -4.16) * mm, "end": v(-4.68, -3.87) * mm});
            skLineSegment(sketch, "E1665", {"start": v(-4.68, -3.87) * mm, "end": v(-4.91, -3.57) * mm});
            skLineSegment(sketch, "E1666", {"start": v(-4.91, -3.57) * mm, "end": v(-5.13, -3.25) * mm});
            skLineSegment(sketch, "E1667", {"start": v(-5.13, -3.25) * mm, "end": v(-5.32, -2.93) * mm});
            skLineSegment(sketch, "E1668", {"start": v(-5.32, -2.93) * mm, "end": v(-5.5, -2.59) * mm});
            skLineSegment(sketch, "E1669", {"start": v(-5.5, -2.59) * mm, "end": v(-5.65, -2.24) * mm});
            skLineSegment(sketch, "E1670", {"start": v(-5.65, -2.24) * mm, "end": v(-5.68, -2.15) * mm});
            skLineSegment(sketch, "E1671", {"start": v(-5.68, -2.15) * mm, "end": v(-38.39, -2.25) * mm});
            skLineSegment(sketch, "E1672", {"start": v(-38.39, -2.25) * mm, "end": v(-38.38, -2.41) * mm});
            skLineSegment(sketch, "E1673", {"start": v(-38.38, -2.41) * mm, "end": v(-38.15, -4.82) * mm});
            skLineSegment(sketch, "E1674", {"start": v(-38.15, -4.82) * mm, "end": v(-37.78, -7.2) * mm});
            skLineSegment(sketch, "E1675", {"start": v(-37.78, -7.2) * mm, "end": v(-37.25, -9.56) * mm});
            skLineSegment(sketch, "E1676", {"start": v(-37.25, -9.56) * mm, "end": v(-36.58, -11.88) * mm});
            skLineSegment(sketch, "E1677", {"start": v(-36.58, -11.88) * mm, "end": v(-35.76, -14.16) * mm});
            skLineSegment(sketch, "E1678", {"start": v(-35.76, -14.16) * mm, "end": v(-34.8, -16.37) * mm});
            skLineSegment(sketch, "E1679", {"start": v(-34.8, -16.37) * mm, "end": v(-33.7, -18.53) * mm});
            skLineSegment(sketch, "E1680", {"start": v(-33.7, -18.53) * mm, "end": v(-32.47, -20.6) * mm});
            skLineSegment(sketch, "E1681", {"start": v(-32.47, -20.6) * mm, "end": v(-31.11, -22.6) * mm});
            skLineSegment(sketch, "E1682", {"start": v(-31.11, -22.6) * mm, "end": v(-29.63, -24.51) * mm});
            skLineSegment(sketch, "E1683", {"start": v(-29.63, -24.51) * mm, "end": v(-28.03, -26.33) * mm});
            skLineSegment(sketch, "E1684", {"start": v(-28.03, -26.33) * mm, "end": v(-26.33, -28.03) * mm});
            skLineSegment(sketch, "E1685", {"start": v(-26.33, -28.03) * mm, "end": v(-24.51, -29.63) * mm});
            skLineSegment(sketch, "E1686", {"start": v(-24.51, -29.63) * mm, "end": v(-22.6, -31.11) * mm});
            skLineSegment(sketch, "E1687", {"start": v(-22.6, -31.11) * mm, "end": v(-20.6, -32.47) * mm});
            skLineSegment(sketch, "E1688", {"start": v(-20.6, -32.47) * mm, "end": v(-18.53, -33.7) * mm});
            skLineSegment(sketch, "E1689", {"start": v(-18.53, -33.7) * mm, "end": v(-16.37, -34.8) * mm});
            skLineSegment(sketch, "E1690", {"start": v(-16.37, -34.8) * mm, "end": v(-14.16, -35.76) * mm});
            skLineSegment(sketch, "E1691", {"start": v(-14.16, -35.76) * mm, "end": v(-11.88, -36.58) * mm});
            skLineSegment(sketch, "E1692", {"start": v(-11.88, -36.58) * mm, "end": v(-9.56, -37.25) * mm});
            skLineSegment(sketch, "E1693", {"start": v(-9.56, -37.25) * mm, "end": v(-7.2, -37.78) * mm});
            skLineSegment(sketch, "E1694", {"start": v(-7.2, -37.78) * mm, "end": v(-4.82, -38.15) * mm});
            skLineSegment(sketch, "E1695", {"start": v(-4.82, -38.15) * mm, "end": v(-2.41, -38.38) * mm});
            skLineSegment(sketch, "E1696", {"start": v(-2.41, -38.38) * mm, "end": v(-2.25, -38.39) * mm});
            skLineSegment(sketch, "E1697", {"start": v(-2.25, -38.39) * mm, "end": v(-2.15, -5.68) * mm});
            skCircle(sketch, "E1698", {"center": v(0, 0) * mm, "radius": 2.65 * mm});
            skCircle(sketch, "E1699", {"center": v(0, 0) * mm, "radius": 26.5 * mm});
            skCircle(sketch, "E1700", {"center": v(0, 0) * mm, "radius": 19.46 * mm});
            skSolve(sketch);
        }
        {
            var Q0;
            Q0=qSketchRegion(id+"F0",true);
            var Q1;
            Q1=makeQuery(id+"F0.imprint","IMPRINT",FACE,{"disambiguationData":[TD([[makeQuery(id+"F0.imprint","IMPRINT",EDGE,{"derivedFrom":sQuery(id+"F0.wireOp",EDGE,"E0")}),1.0]])]});
            var Q2;
            {var subQ0=sQuery(id+"F0.wireOp",EDGE,"E1700");var subQ1=sQuery(id+"F0.wireOp",EDGE,"E1544");var subQ2=makeQuery(id+"F0.imprint","INTERSECT",VERTEX,{"derivedFrom":[subQ1,subQ0]});Q2=makeQuery(id+"F0.imprint","IMPRINT",FACE,{"disambiguationData":[TD([[makeQuery(id+"F0.imprint","IMPRINT",EDGE,{"disambiguationData":[TD([[subQ2,-1.0]])],"derivedFrom":subQ1}),1.0]])]});}
            var Q3;
            {var subQ0=sQuery(id+"F0.wireOp",EDGE,"E1699");var subQ1=sQuery(id+"F0.wireOp",EDGE,"E1570");var subQ2=makeQuery(id+"F0.imprint","INTERSECT",VERTEX,{"derivedFrom":[subQ1,subQ0]});Q3=makeQuery(id+"F0.imprint","IMPRINT",FACE,{"disambiguationData":[TD([[makeQuery(id+"F0.imprint","IMPRINT",EDGE,{"disambiguationData":[TD([[subQ2,-1.0]])],"derivedFrom":subQ1}),-1.0]])]});}
            var Q4;
            {var subQ0=sQuery(id+"F0.wireOp",EDGE,"E1700");var subQ1=sQuery(id+"F0.wireOp",EDGE,"E1654");var subQ2=makeQuery(id+"F0.imprint","INTERSECT",VERTEX,{"derivedFrom":[subQ1,subQ0]});Q4=makeQuery(id+"F0.imprint","IMPRINT",FACE,{"disambiguationData":[TD([[makeQuery(id+"F0.imprint","IMPRINT",EDGE,{"disambiguationData":[TD([[subQ2,-1.0]])],"derivedFrom":subQ1}),-1.0]])]});}
            var Q5;
            {var subQ0=sQuery(id+"F0.wireOp",EDGE,"E1699");var subQ1=sQuery(id+"F0.wireOp",EDGE,"E1638");var subQ2=makeQuery(id+"F0.imprint","INTERSECT",VERTEX,{"derivedFrom":[subQ1,subQ0]});Q5=makeQuery(id+"F0.imprint","IMPRINT",FACE,{"disambiguationData":[TD([[makeQuery(id+"F0.imprint","IMPRINT",EDGE,{"disambiguationData":[TD([[subQ2,-1.0]])],"derivedFrom":subQ1}),1.0]])]});}
            var Q6;
            {var subQ0=sQuery(id+"F0.wireOp",EDGE,"E1700");var subQ1=sQuery(id+"F0.wireOp",EDGE,"E1613");var subQ2=makeQuery(id+"F0.imprint","INTERSECT",VERTEX,{"derivedFrom":[subQ1,subQ0]});Q6=makeQuery(id+"F0.imprint","IMPRINT",FACE,{"disambiguationData":[TD([[makeQuery(id+"F0.imprint","IMPRINT",EDGE,{"disambiguationData":[TD([[subQ2,-1.0]])],"derivedFrom":subQ1}),-1.0]])]});}
            var Q7;
            {var subQ0=sQuery(id+"F0.wireOp",EDGE,"E1699");var subQ1=sQuery(id+"F0.wireOp",EDGE,"E1597");var subQ2=makeQuery(id+"F0.imprint","INTERSECT",VERTEX,{"derivedFrom":[subQ1,subQ0]});Q7=makeQuery(id+"F0.imprint","IMPRINT",FACE,{"disambiguationData":[TD([[makeQuery(id+"F0.imprint","IMPRINT",EDGE,{"disambiguationData":[TD([[subQ2,-1.0]])],"derivedFrom":subQ1}),1.0]])]});}
            var Q8;
            Q8=makeQuery(id+"F0.imprint","IMPRINT",FACE,{"disambiguationData":[TD([[makeQuery(id+"F0.imprint","IMPRINT",EDGE,{"derivedFrom":sQuery(id+"F0.wireOp",EDGE,"E1530")}),-1.0]])]});
            var Q9;
            {var subQ0=sQuery(id+"F0.wireOp",EDGE,"E1700");var subQ1=sQuery(id+"F0.wireOp",EDGE,"E1544");var subQ2=makeQuery(id+"F0.imprint","INTERSECT",VERTEX,{"derivedFrom":[subQ1,subQ0]});Q9=makeQuery(id+"F0.imprint","IMPRINT",FACE,{"disambiguationData":[TD([[makeQuery(id+"F0.imprint","IMPRINT",EDGE,{"disambiguationData":[TD([[subQ2,-1.0]])],"derivedFrom":subQ1}),-1.0]])]});}
            var Q10;
            {var subQ0=sQuery(id+"F0.wireOp",EDGE,"E1700");var subQ1=sQuery(id+"F0.wireOp",EDGE,"E1671");var subQ2=makeQuery(id+"F0.imprint","INTERSECT",VERTEX,{"derivedFrom":[subQ1,subQ0]});Q10=makeQuery(id+"F0.imprint","IMPRINT",FACE,{"disambiguationData":[TD([[makeQuery(id+"F0.imprint","IMPRINT",EDGE,{"disambiguationData":[TD([[subQ2,-1.0]])],"derivedFrom":subQ1}),1.0]])]});}
            extrude(context, id + "F1", {"entities" : qUnion([Q0, Q1, Q2, Q3, Q4, Q5, Q6, Q7, Q8, Q9, Q10]), "depth" : 5 * mm});
        }
    });
